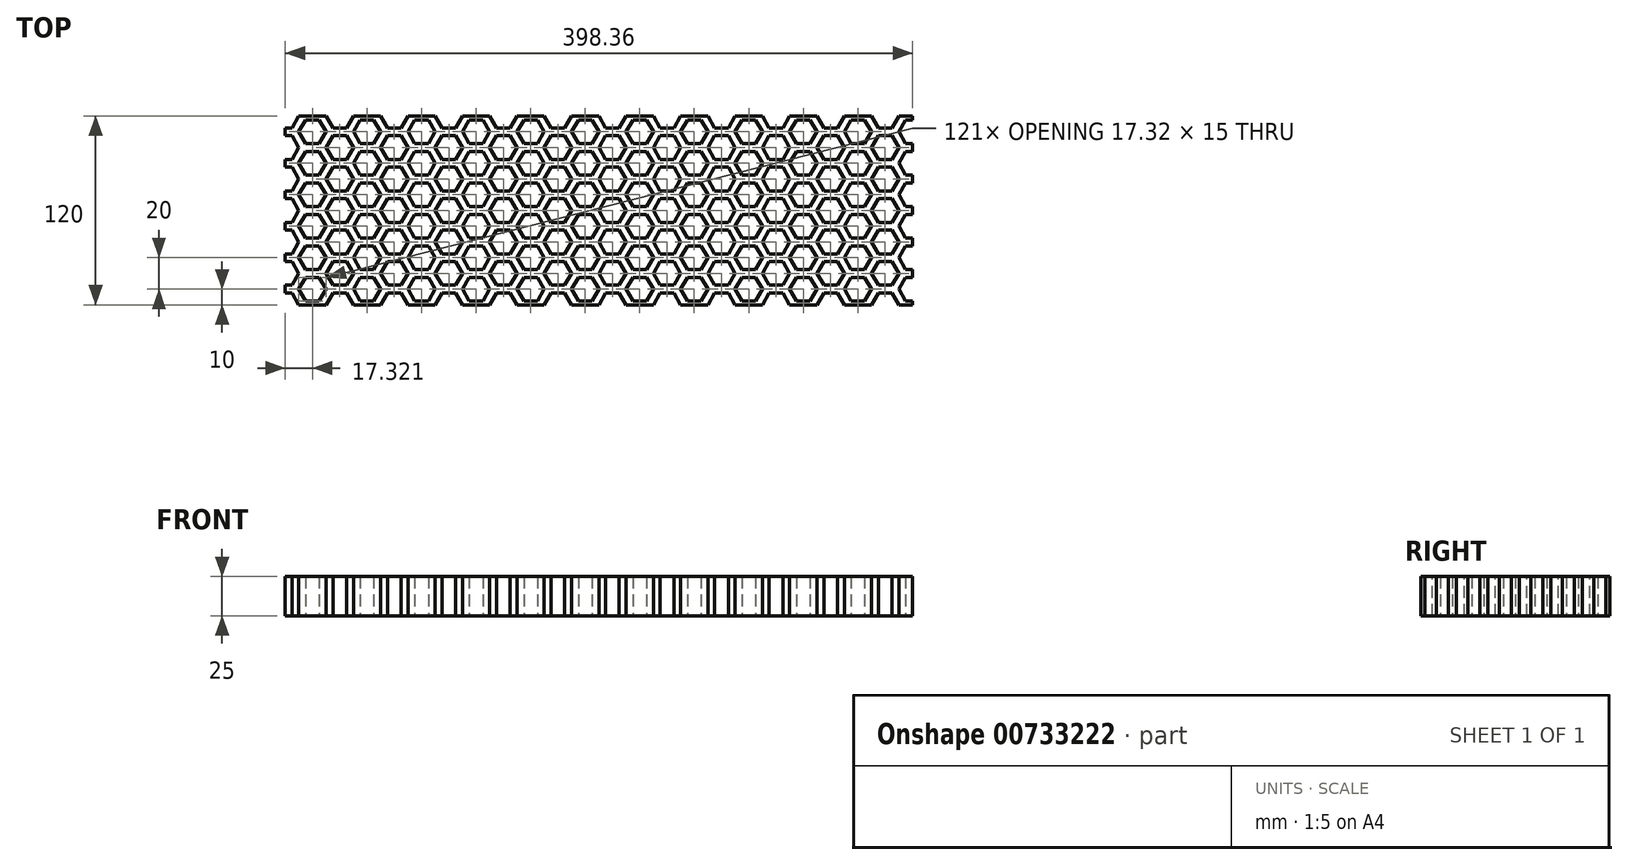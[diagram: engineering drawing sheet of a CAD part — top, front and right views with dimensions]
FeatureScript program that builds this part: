
annotation { "Feature Type Name" : "Feature", "Feature Type Description" : "" }
export const myFeature = defineFeature(function(context is Context, id is Id, definition is map)
    precondition{}
    {
        {
            var Q0;
            Q0=qCreatedBy(makeId("Top.planeOp"),FACE);
            var sketch = newSketch(context, id + "F0", { "sketchPlane" : qUnion([Q0])});
            skLineSegment(sketch, "E0.0", {"start": v(16.84, -2.5) * mm, "end": v(21.65, -2.5) * mm});
            skLineSegment(sketch, "E0.1", {"start": v(21.65, -2.5) * mm, "end": v(25.98, -10) * mm});
            skLineSegment(sketch, "E1.0", {"start": v(16.84, 17.5) * mm, "end": v(21.65, 17.5) * mm});
            skLineSegment(sketch, "E1.1", {"start": v(21.65, 17.5) * mm, "end": v(25.98, 10) * mm});
            skLineSegment(sketch, "E1.2", {"start": v(25.98, 10) * mm, "end": v(21.65, 2.5) * mm});
            skLineSegment(sketch, "E1.3", {"start": v(21.65, 2.5) * mm, "end": v(16.84, 2.5) * mm});
            skLineSegment(sketch, "E2.0.1.1", {"start": v(21.65, 57.5) * mm, "end": v(25.98, 50) * mm});
            skLineSegment(sketch, "E2.0.1.11", {"start": v(21.65, 22.5) * mm, "end": v(16.84, 22.5) * mm});
            skLineSegment(sketch, "E2.0.1.12", {"start": v(25.98, 30) * mm, "end": v(21.65, 22.5) * mm});
            skLineSegment(sketch, "E2.0.1.14", {"start": v(25.98, 50) * mm, "end": v(21.65, 42.5) * mm});
            skLineSegment(sketch, "E2.0.1.20", {"start": v(21.65, 37.5) * mm, "end": v(25.98, 30) * mm});
            skLineSegment(sketch, "E2.0.1.23", {"start": v(16.84, 57.5) * mm, "end": v(21.65, 57.5) * mm});
            skLineSegment(sketch, "E2.0.1.24", {"start": v(16.84, 37.5) * mm, "end": v(21.65, 37.5) * mm});
            skLineSegment(sketch, "E2.0.2.1", {"start": v(21.65, 97.5) * mm, "end": v(25.98, 90) * mm});
            skLineSegment(sketch, "E2.0.2.6", {"start": v(21.65, 82.5) * mm, "end": v(16.84, 82.5) * mm});
            skLineSegment(sketch, "E2.0.2.11", {"start": v(21.65, 62.5) * mm, "end": v(16.84, 62.5) * mm});
            skLineSegment(sketch, "E2.0.2.12", {"start": v(25.98, 70) * mm, "end": v(21.65, 62.5) * mm});
            skLineSegment(sketch, "E2.0.2.14", {"start": v(25.98, 90) * mm, "end": v(21.65, 82.5) * mm});
            skLineSegment(sketch, "E2.0.2.20", {"start": v(21.65, 77.5) * mm, "end": v(25.98, 70) * mm});
            skLineSegment(sketch, "E2.0.2.23", {"start": v(16.84, 97.5) * mm, "end": v(21.65, 97.5) * mm});
            skLineSegment(sketch, "E2.0.2.24", {"start": v(16.84, 77.5) * mm, "end": v(21.65, 77.5) * mm});
            skLineSegment(sketch, "E2.0.3.6", {"start": v(21.65, 122.5) * mm, "end": v(16.84, 122.5) * mm});
            skLineSegment(sketch, "E2.0.3.11", {"start": v(21.65, 102.5) * mm, "end": v(16.84, 102.5) * mm});
            skLineSegment(sketch, "E2.0.3.12", {"start": v(25.98, 110) * mm, "end": v(21.65, 102.5) * mm});
            skLineSegment(sketch, "E2.0.3.14", {"start": v(25.98, 130) * mm, "end": v(21.65, 122.5) * mm});
            skLineSegment(sketch, "E2.0.3.20", {"start": v(21.65, 117.5) * mm, "end": v(25.98, 110) * mm});
            skLineSegment(sketch, "E2.0.3.24", {"start": v(16.84, 117.5) * mm, "end": v(21.65, 117.5) * mm});
            skLineSegment(sketch, "E2.1.0.0", {"start": v(43.3, -10) * mm, "end": v(47.63, -2.5) * mm});
            skLineSegment(sketch, "E2.1.0.1", {"start": v(56.3, 17.5) * mm, "end": v(60.62, 10) * mm});
            skLineSegment(sketch, "E2.1.0.2", {"start": v(25.98, 0) * mm, "end": v(30.3, 7.5) * mm});
            skPoint(sketch, "E2.1.0.3", {"position": v(51.96, 17.5) * mm});
            skLineSegment(sketch, "E2.1.0.4", {"start": v(30.3, -7.5) * mm, "end": v(25.98, 0) * mm});
            skLineSegment(sketch, "E2.1.0.5", {"start": v(38.97, -7.5) * mm, "end": v(30.3, -7.5) * mm});
            skLineSegment(sketch, "E2.1.0.6", {"start": v(56.3, 2.5) * mm, "end": v(47.63, 2.5) * mm});
            skLineSegment(sketch, "E2.1.0.7", {"start": v(43.3, 0) * mm, "end": v(38.97, -7.5) * mm});
            skLineSegment(sketch, "E2.1.0.8", {"start": v(47.63, 2.5) * mm, "end": v(43.3, 10) * mm});
            skLineSegment(sketch, "E2.1.0.13", {"start": v(25.98, 0) * mm, "end": v(43.3, 0) * mm, "construction": true});
            skLineSegment(sketch, "E2.1.0.14", {"start": v(60.62, 10) * mm, "end": v(56.3, 2.5) * mm});
            skPoint(sketch, "E2.1.0.15", {"position": v(51.96, -2.5) * mm});
            skCircle(sketch, "E2.1.0.16", {"center": v(51.96, 10) * mm, "radius": 7.5 * mm, "construction": true});
            skCircle(sketch, "E2.1.0.17", {"center": v(34.64, 0) * mm, "radius": 7.5 * mm, "construction": true});
            skLineSegment(sketch, "E2.1.0.18", {"start": v(38.97, 7.5) * mm, "end": v(43.3, 0) * mm});
            skPoint(sketch, "E2.1.0.19", {"position": v(34.64, 7.5) * mm});
            skLineSegment(sketch, "E2.1.0.20", {"start": v(56.3, -2.5) * mm, "end": v(60.62, -10) * mm});
            skLineSegment(sketch, "E2.1.0.21", {"start": v(43.3, 10) * mm, "end": v(47.63, 17.5) * mm});
            skLineSegment(sketch, "E2.1.0.22", {"start": v(30.3, 7.5) * mm, "end": v(38.97, 7.5) * mm});
            skLineSegment(sketch, "E2.1.0.23", {"start": v(47.63, 17.5) * mm, "end": v(56.3, 17.5) * mm});
            skLineSegment(sketch, "E2.1.0.24", {"start": v(47.63, -2.5) * mm, "end": v(56.3, -2.5) * mm});
            skLineSegment(sketch, "E2.1.1.0", {"start": v(43.3, 30) * mm, "end": v(47.63, 37.5) * mm});
            skLineSegment(sketch, "E2.1.1.1", {"start": v(56.3, 57.5) * mm, "end": v(60.62, 50) * mm});
            skLineSegment(sketch, "E2.1.1.2", {"start": v(25.98, 40) * mm, "end": v(30.3, 47.5) * mm});
            skPoint(sketch, "E2.1.1.3", {"position": v(51.96, 57.5) * mm});
            skLineSegment(sketch, "E2.1.1.4", {"start": v(30.3, 32.5) * mm, "end": v(25.98, 40) * mm});
            skLineSegment(sketch, "E2.1.1.5", {"start": v(38.97, 32.5) * mm, "end": v(30.3, 32.5) * mm});
            skLineSegment(sketch, "E2.1.1.6", {"start": v(56.3, 42.5) * mm, "end": v(47.63, 42.5) * mm});
            skLineSegment(sketch, "E2.1.1.7", {"start": v(43.3, 40) * mm, "end": v(38.97, 32.5) * mm});
            skLineSegment(sketch, "E2.1.1.8", {"start": v(47.63, 42.5) * mm, "end": v(43.3, 50) * mm});
            skCircle(sketch, "E2.1.1.9", {"center": v(51.96, 30) * mm, "radius": 7.5 * mm, "construction": true});
            skLineSegment(sketch, "E2.1.1.10", {"start": v(47.63, 22.5) * mm, "end": v(43.3, 30) * mm});
            skLineSegment(sketch, "E2.1.1.11", {"start": v(56.3, 22.5) * mm, "end": v(47.63, 22.5) * mm});
            skLineSegment(sketch, "E2.1.1.12", {"start": v(60.62, 30) * mm, "end": v(56.3, 22.5) * mm});
            skLineSegment(sketch, "E2.1.1.13", {"start": v(25.98, 40) * mm, "end": v(43.3, 40) * mm, "construction": true});
            skLineSegment(sketch, "E2.1.1.14", {"start": v(60.62, 50) * mm, "end": v(56.3, 42.5) * mm});
            skPoint(sketch, "E2.1.1.15", {"position": v(51.96, 37.5) * mm});
            skCircle(sketch, "E2.1.1.16", {"center": v(51.96, 50) * mm, "radius": 7.5 * mm, "construction": true});
            skCircle(sketch, "E2.1.1.17", {"center": v(34.64, 40) * mm, "radius": 7.5 * mm, "construction": true});
            skLineSegment(sketch, "E2.1.1.18", {"start": v(38.97, 47.5) * mm, "end": v(43.3, 40) * mm});
            skPoint(sketch, "E2.1.1.19", {"position": v(34.64, 47.5) * mm});
            skLineSegment(sketch, "E2.1.1.20", {"start": v(56.3, 37.5) * mm, "end": v(60.62, 30) * mm});
            skLineSegment(sketch, "E2.1.1.21", {"start": v(43.3, 50) * mm, "end": v(47.63, 57.5) * mm});
            skLineSegment(sketch, "E2.1.1.22", {"start": v(30.3, 47.5) * mm, "end": v(38.97, 47.5) * mm});
            skLineSegment(sketch, "E2.1.1.23", {"start": v(47.63, 57.5) * mm, "end": v(56.3, 57.5) * mm});
            skLineSegment(sketch, "E2.1.1.24", {"start": v(47.63, 37.5) * mm, "end": v(56.3, 37.5) * mm});
            skLineSegment(sketch, "E2.1.2.0", {"start": v(43.3, 70) * mm, "end": v(47.63, 77.5) * mm});
            skLineSegment(sketch, "E2.1.2.1", {"start": v(56.3, 97.5) * mm, "end": v(60.62, 90) * mm});
            skLineSegment(sketch, "E2.1.2.2", {"start": v(25.98, 80) * mm, "end": v(30.3, 87.5) * mm});
            skPoint(sketch, "E2.1.2.3", {"position": v(51.96, 97.5) * mm});
            skLineSegment(sketch, "E2.1.2.4", {"start": v(30.3, 72.5) * mm, "end": v(25.98, 80) * mm});
            skLineSegment(sketch, "E2.1.2.5", {"start": v(38.97, 72.5) * mm, "end": v(30.3, 72.5) * mm});
            skLineSegment(sketch, "E2.1.2.6", {"start": v(56.3, 82.5) * mm, "end": v(47.63, 82.5) * mm});
            skLineSegment(sketch, "E2.1.2.7", {"start": v(43.3, 80) * mm, "end": v(38.97, 72.5) * mm});
            skLineSegment(sketch, "E2.1.2.8", {"start": v(47.63, 82.5) * mm, "end": v(43.3, 90) * mm});
            skCircle(sketch, "E2.1.2.9", {"center": v(51.96, 70) * mm, "radius": 7.5 * mm, "construction": true});
            skLineSegment(sketch, "E2.1.2.10", {"start": v(47.63, 62.5) * mm, "end": v(43.3, 70) * mm});
            skLineSegment(sketch, "E2.1.2.11", {"start": v(56.3, 62.5) * mm, "end": v(47.63, 62.5) * mm});
            skLineSegment(sketch, "E2.1.2.12", {"start": v(60.62, 70) * mm, "end": v(56.3, 62.5) * mm});
            skLineSegment(sketch, "E2.1.2.13", {"start": v(25.98, 80) * mm, "end": v(43.3, 80) * mm, "construction": true});
            skLineSegment(sketch, "E2.1.2.14", {"start": v(60.62, 90) * mm, "end": v(56.3, 82.5) * mm});
            skPoint(sketch, "E2.1.2.15", {"position": v(51.96, 77.5) * mm});
            skCircle(sketch, "E2.1.2.16", {"center": v(51.96, 90) * mm, "radius": 7.5 * mm, "construction": true});
            skCircle(sketch, "E2.1.2.17", {"center": v(34.64, 80) * mm, "radius": 7.5 * mm, "construction": true});
            skLineSegment(sketch, "E2.1.2.18", {"start": v(38.97, 87.5) * mm, "end": v(43.3, 80) * mm});
            skPoint(sketch, "E2.1.2.19", {"position": v(34.64, 87.5) * mm});
            skLineSegment(sketch, "E2.1.2.20", {"start": v(56.3, 77.5) * mm, "end": v(60.62, 70) * mm});
            skLineSegment(sketch, "E2.1.2.21", {"start": v(43.3, 90) * mm, "end": v(47.63, 97.5) * mm});
            skLineSegment(sketch, "E2.1.2.22", {"start": v(30.3, 87.5) * mm, "end": v(38.97, 87.5) * mm});
            skLineSegment(sketch, "E2.1.2.23", {"start": v(47.63, 97.5) * mm, "end": v(56.3, 97.5) * mm});
            skLineSegment(sketch, "E2.1.2.24", {"start": v(47.63, 77.5) * mm, "end": v(56.3, 77.5) * mm});
            skLineSegment(sketch, "E2.1.3.0", {"start": v(43.3, 110) * mm, "end": v(47.63, 117.5) * mm});
            skLineSegment(sketch, "E2.1.3.2", {"start": v(25.98, 120) * mm, "end": v(30.3, 127.5) * mm});
            skLineSegment(sketch, "E2.1.3.4", {"start": v(30.3, 112.5) * mm, "end": v(25.98, 120) * mm});
            skLineSegment(sketch, "E2.1.3.5", {"start": v(38.97, 112.5) * mm, "end": v(30.3, 112.5) * mm});
            skLineSegment(sketch, "E2.1.3.6", {"start": v(56.3, 122.5) * mm, "end": v(47.63, 122.5) * mm});
            skLineSegment(sketch, "E2.1.3.7", {"start": v(43.3, 120) * mm, "end": v(38.97, 112.5) * mm});
            skLineSegment(sketch, "E2.1.3.8", {"start": v(47.63, 122.5) * mm, "end": v(43.3, 130) * mm});
            skCircle(sketch, "E2.1.3.9", {"center": v(51.96, 110) * mm, "radius": 7.5 * mm, "construction": true});
            skLineSegment(sketch, "E2.1.3.10", {"start": v(47.63, 102.5) * mm, "end": v(43.3, 110) * mm});
            skLineSegment(sketch, "E2.1.3.11", {"start": v(56.3, 102.5) * mm, "end": v(47.63, 102.5) * mm});
            skLineSegment(sketch, "E2.1.3.12", {"start": v(60.62, 110) * mm, "end": v(56.3, 102.5) * mm});
            skLineSegment(sketch, "E2.1.3.13", {"start": v(25.98, 120) * mm, "end": v(43.3, 120) * mm, "construction": true});
            skLineSegment(sketch, "E2.1.3.14", {"start": v(60.62, 130) * mm, "end": v(56.3, 122.5) * mm});
            skPoint(sketch, "E2.1.3.15", {"position": v(51.96, 117.5) * mm});
            skCircle(sketch, "E2.1.3.17", {"center": v(34.64, 120) * mm, "radius": 7.5 * mm, "construction": true});
            skLineSegment(sketch, "E2.1.3.18", {"start": v(38.97, 127.5) * mm, "end": v(43.3, 120) * mm});
            skLineSegment(sketch, "E2.1.3.20", {"start": v(56.3, 117.5) * mm, "end": v(60.62, 110) * mm});
            skLineSegment(sketch, "E2.1.3.22", {"start": v(30.3, 127.5) * mm, "end": v(38.97, 127.5) * mm});
            skLineSegment(sketch, "E2.1.3.24", {"start": v(47.63, 117.5) * mm, "end": v(56.3, 117.5) * mm});
            skLineSegment(sketch, "E2.2.0.0", {"start": v(77.94, -10) * mm, "end": v(82.27, -2.5) * mm});
            skLineSegment(sketch, "E2.2.0.1", {"start": v(90.93, 17.5) * mm, "end": v(95.26, 10) * mm});
            skLineSegment(sketch, "E2.2.0.2", {"start": v(60.62, 0) * mm, "end": v(64.95, 7.5) * mm});
            skPoint(sketch, "E2.2.0.3", {"position": v(86.6, 17.5) * mm});
            skLineSegment(sketch, "E2.2.0.4", {"start": v(64.95, -7.5) * mm, "end": v(60.62, 0) * mm});
            skLineSegment(sketch, "E2.2.0.5", {"start": v(73.61, -7.5) * mm, "end": v(64.95, -7.5) * mm});
            skLineSegment(sketch, "E2.2.0.6", {"start": v(90.93, 2.5) * mm, "end": v(82.27, 2.5) * mm});
            skLineSegment(sketch, "E2.2.0.7", {"start": v(77.94, 0) * mm, "end": v(73.61, -7.5) * mm});
            skLineSegment(sketch, "E2.2.0.8", {"start": v(82.27, 2.5) * mm, "end": v(77.94, 10) * mm});
            skLineSegment(sketch, "E2.2.0.13", {"start": v(60.62, 0) * mm, "end": v(77.94, 0) * mm, "construction": true});
            skLineSegment(sketch, "E2.2.0.14", {"start": v(95.26, 10) * mm, "end": v(90.93, 2.5) * mm});
            skPoint(sketch, "E2.2.0.15", {"position": v(86.6, -2.5) * mm});
            skCircle(sketch, "E2.2.0.16", {"center": v(86.6, 10) * mm, "radius": 7.5 * mm, "construction": true});
            skCircle(sketch, "E2.2.0.17", {"center": v(69.28, 0) * mm, "radius": 7.5 * mm, "construction": true});
            skLineSegment(sketch, "E2.2.0.18", {"start": v(73.61, 7.5) * mm, "end": v(77.94, 0) * mm});
            skPoint(sketch, "E2.2.0.19", {"position": v(69.28, 7.5) * mm});
            skLineSegment(sketch, "E2.2.0.20", {"start": v(90.93, -2.5) * mm, "end": v(95.26, -10) * mm});
            skLineSegment(sketch, "E2.2.0.21", {"start": v(77.94, 10) * mm, "end": v(82.27, 17.5) * mm});
            skLineSegment(sketch, "E2.2.0.22", {"start": v(64.95, 7.5) * mm, "end": v(73.61, 7.5) * mm});
            skLineSegment(sketch, "E2.2.0.23", {"start": v(82.27, 17.5) * mm, "end": v(90.93, 17.5) * mm});
            skLineSegment(sketch, "E2.2.0.24", {"start": v(82.27, -2.5) * mm, "end": v(90.93, -2.5) * mm});
            skLineSegment(sketch, "E2.2.1.0", {"start": v(77.94, 30) * mm, "end": v(82.27, 37.5) * mm});
            skLineSegment(sketch, "E2.2.1.1", {"start": v(90.93, 57.5) * mm, "end": v(95.26, 50) * mm});
            skLineSegment(sketch, "E2.2.1.2", {"start": v(60.62, 40) * mm, "end": v(64.95, 47.5) * mm});
            skPoint(sketch, "E2.2.1.3", {"position": v(86.6, 57.5) * mm});
            skLineSegment(sketch, "E2.2.1.4", {"start": v(64.95, 32.5) * mm, "end": v(60.62, 40) * mm});
            skLineSegment(sketch, "E2.2.1.5", {"start": v(73.61, 32.5) * mm, "end": v(64.95, 32.5) * mm});
            skLineSegment(sketch, "E2.2.1.6", {"start": v(90.93, 42.5) * mm, "end": v(82.27, 42.5) * mm});
            skLineSegment(sketch, "E2.2.1.7", {"start": v(77.94, 40) * mm, "end": v(73.61, 32.5) * mm});
            skLineSegment(sketch, "E2.2.1.8", {"start": v(82.27, 42.5) * mm, "end": v(77.94, 50) * mm});
            skCircle(sketch, "E2.2.1.9", {"center": v(86.6, 30) * mm, "radius": 7.5 * mm, "construction": true});
            skLineSegment(sketch, "E2.2.1.10", {"start": v(82.27, 22.5) * mm, "end": v(77.94, 30) * mm});
            skLineSegment(sketch, "E2.2.1.11", {"start": v(90.93, 22.5) * mm, "end": v(82.27, 22.5) * mm});
            skLineSegment(sketch, "E2.2.1.12", {"start": v(95.26, 30) * mm, "end": v(90.93, 22.5) * mm});
            skLineSegment(sketch, "E2.2.1.13", {"start": v(60.62, 40) * mm, "end": v(77.94, 40) * mm, "construction": true});
            skLineSegment(sketch, "E2.2.1.14", {"start": v(95.26, 50) * mm, "end": v(90.93, 42.5) * mm});
            skPoint(sketch, "E2.2.1.15", {"position": v(86.6, 37.5) * mm});
            skCircle(sketch, "E2.2.1.16", {"center": v(86.6, 50) * mm, "radius": 7.5 * mm, "construction": true});
            skCircle(sketch, "E2.2.1.17", {"center": v(69.28, 40) * mm, "radius": 7.5 * mm, "construction": true});
            skLineSegment(sketch, "E2.2.1.18", {"start": v(73.61, 47.5) * mm, "end": v(77.94, 40) * mm});
            skPoint(sketch, "E2.2.1.19", {"position": v(69.28, 47.5) * mm});
            skLineSegment(sketch, "E2.2.1.20", {"start": v(90.93, 37.5) * mm, "end": v(95.26, 30) * mm});
            skLineSegment(sketch, "E2.2.1.21", {"start": v(77.94, 50) * mm, "end": v(82.27, 57.5) * mm});
            skLineSegment(sketch, "E2.2.1.22", {"start": v(64.95, 47.5) * mm, "end": v(73.61, 47.5) * mm});
            skLineSegment(sketch, "E2.2.1.23", {"start": v(82.27, 57.5) * mm, "end": v(90.93, 57.5) * mm});
            skLineSegment(sketch, "E2.2.1.24", {"start": v(82.27, 37.5) * mm, "end": v(90.93, 37.5) * mm});
            skLineSegment(sketch, "E2.2.2.0", {"start": v(77.94, 70) * mm, "end": v(82.27, 77.5) * mm});
            skLineSegment(sketch, "E2.2.2.1", {"start": v(90.93, 97.5) * mm, "end": v(95.26, 90) * mm});
            skLineSegment(sketch, "E2.2.2.2", {"start": v(60.62, 80) * mm, "end": v(64.95, 87.5) * mm});
            skPoint(sketch, "E2.2.2.3", {"position": v(86.6, 97.5) * mm});
            skLineSegment(sketch, "E2.2.2.4", {"start": v(64.95, 72.5) * mm, "end": v(60.62, 80) * mm});
            skLineSegment(sketch, "E2.2.2.5", {"start": v(73.61, 72.5) * mm, "end": v(64.95, 72.5) * mm});
            skLineSegment(sketch, "E2.2.2.6", {"start": v(90.93, 82.5) * mm, "end": v(82.27, 82.5) * mm});
            skLineSegment(sketch, "E2.2.2.7", {"start": v(77.94, 80) * mm, "end": v(73.61, 72.5) * mm});
            skLineSegment(sketch, "E2.2.2.8", {"start": v(82.27, 82.5) * mm, "end": v(77.94, 90) * mm});
            skCircle(sketch, "E2.2.2.9", {"center": v(86.6, 70) * mm, "radius": 7.5 * mm, "construction": true});
            skLineSegment(sketch, "E2.2.2.10", {"start": v(82.27, 62.5) * mm, "end": v(77.94, 70) * mm});
            skLineSegment(sketch, "E2.2.2.11", {"start": v(90.93, 62.5) * mm, "end": v(82.27, 62.5) * mm});
            skLineSegment(sketch, "E2.2.2.12", {"start": v(95.26, 70) * mm, "end": v(90.93, 62.5) * mm});
            skLineSegment(sketch, "E2.2.2.13", {"start": v(60.62, 80) * mm, "end": v(77.94, 80) * mm, "construction": true});
            skLineSegment(sketch, "E2.2.2.14", {"start": v(95.26, 90) * mm, "end": v(90.93, 82.5) * mm});
            skPoint(sketch, "E2.2.2.15", {"position": v(86.6, 77.5) * mm});
            skCircle(sketch, "E2.2.2.16", {"center": v(86.6, 90) * mm, "radius": 7.5 * mm, "construction": true});
            skCircle(sketch, "E2.2.2.17", {"center": v(69.28, 80) * mm, "radius": 7.5 * mm, "construction": true});
            skLineSegment(sketch, "E2.2.2.18", {"start": v(73.61, 87.5) * mm, "end": v(77.94, 80) * mm});
            skPoint(sketch, "E2.2.2.19", {"position": v(69.28, 87.5) * mm});
            skLineSegment(sketch, "E2.2.2.20", {"start": v(90.93, 77.5) * mm, "end": v(95.26, 70) * mm});
            skLineSegment(sketch, "E2.2.2.21", {"start": v(77.94, 90) * mm, "end": v(82.27, 97.5) * mm});
            skLineSegment(sketch, "E2.2.2.22", {"start": v(64.95, 87.5) * mm, "end": v(73.61, 87.5) * mm});
            skLineSegment(sketch, "E2.2.2.23", {"start": v(82.27, 97.5) * mm, "end": v(90.93, 97.5) * mm});
            skLineSegment(sketch, "E2.2.2.24", {"start": v(82.27, 77.5) * mm, "end": v(90.93, 77.5) * mm});
            skLineSegment(sketch, "E2.2.3.0", {"start": v(77.94, 110) * mm, "end": v(82.27, 117.5) * mm});
            skLineSegment(sketch, "E2.2.3.2", {"start": v(60.62, 120) * mm, "end": v(64.95, 127.5) * mm});
            skLineSegment(sketch, "E2.2.3.4", {"start": v(64.95, 112.5) * mm, "end": v(60.62, 120) * mm});
            skLineSegment(sketch, "E2.2.3.5", {"start": v(73.61, 112.5) * mm, "end": v(64.95, 112.5) * mm});
            skLineSegment(sketch, "E2.2.3.6", {"start": v(90.93, 122.5) * mm, "end": v(82.27, 122.5) * mm});
            skLineSegment(sketch, "E2.2.3.7", {"start": v(77.94, 120) * mm, "end": v(73.61, 112.5) * mm});
            skLineSegment(sketch, "E2.2.3.8", {"start": v(82.27, 122.5) * mm, "end": v(77.94, 130) * mm});
            skCircle(sketch, "E2.2.3.9", {"center": v(86.6, 110) * mm, "radius": 7.5 * mm, "construction": true});
            skLineSegment(sketch, "E2.2.3.10", {"start": v(82.27, 102.5) * mm, "end": v(77.94, 110) * mm});
            skLineSegment(sketch, "E2.2.3.11", {"start": v(90.93, 102.5) * mm, "end": v(82.27, 102.5) * mm});
            skLineSegment(sketch, "E2.2.3.12", {"start": v(95.26, 110) * mm, "end": v(90.93, 102.5) * mm});
            skLineSegment(sketch, "E2.2.3.13", {"start": v(60.62, 120) * mm, "end": v(77.94, 120) * mm, "construction": true});
            skLineSegment(sketch, "E2.2.3.14", {"start": v(95.26, 130) * mm, "end": v(90.93, 122.5) * mm});
            skPoint(sketch, "E2.2.3.15", {"position": v(86.6, 117.5) * mm});
            skCircle(sketch, "E2.2.3.17", {"center": v(69.28, 120) * mm, "radius": 7.5 * mm, "construction": true});
            skLineSegment(sketch, "E2.2.3.18", {"start": v(73.61, 127.5) * mm, "end": v(77.94, 120) * mm});
            skLineSegment(sketch, "E2.2.3.20", {"start": v(90.93, 117.5) * mm, "end": v(95.26, 110) * mm});
            skLineSegment(sketch, "E2.2.3.22", {"start": v(64.95, 127.5) * mm, "end": v(73.61, 127.5) * mm});
            skLineSegment(sketch, "E2.2.3.24", {"start": v(82.27, 117.5) * mm, "end": v(90.93, 117.5) * mm});
            skLineSegment(sketch, "E2.3.0.0", {"start": v(112.58, -10) * mm, "end": v(116.91, -2.5) * mm});
            skLineSegment(sketch, "E2.3.0.1", {"start": v(125.57, 17.5) * mm, "end": v(129.9, 10) * mm});
            skLineSegment(sketch, "E2.3.0.2", {"start": v(95.26, 0) * mm, "end": v(99.59, 7.5) * mm});
            skPoint(sketch, "E2.3.0.3", {"position": v(121.24, 17.5) * mm});
            skLineSegment(sketch, "E2.3.0.4", {"start": v(99.59, -7.5) * mm, "end": v(95.26, 0) * mm});
            skLineSegment(sketch, "E2.3.0.5", {"start": v(108.25, -7.5) * mm, "end": v(99.59, -7.5) * mm});
            skLineSegment(sketch, "E2.3.0.6", {"start": v(125.57, 2.5) * mm, "end": v(116.91, 2.5) * mm});
            skLineSegment(sketch, "E2.3.0.7", {"start": v(112.58, 0) * mm, "end": v(108.25, -7.5) * mm});
            skLineSegment(sketch, "E2.3.0.8", {"start": v(116.91, 2.5) * mm, "end": v(112.58, 10) * mm});
            skLineSegment(sketch, "E2.3.0.13", {"start": v(95.26, 0) * mm, "end": v(112.58, 0) * mm, "construction": true});
            skLineSegment(sketch, "E2.3.0.14", {"start": v(129.9, 10) * mm, "end": v(125.57, 2.5) * mm});
            skPoint(sketch, "E2.3.0.15", {"position": v(121.24, -2.5) * mm});
            skCircle(sketch, "E2.3.0.16", {"center": v(121.24, 10) * mm, "radius": 7.5 * mm, "construction": true});
            skCircle(sketch, "E2.3.0.17", {"center": v(103.92, 0) * mm, "radius": 7.5 * mm, "construction": true});
            skLineSegment(sketch, "E2.3.0.18", {"start": v(108.25, 7.5) * mm, "end": v(112.58, 0) * mm});
            skPoint(sketch, "E2.3.0.19", {"position": v(103.92, 7.5) * mm});
            skLineSegment(sketch, "E2.3.0.20", {"start": v(125.57, -2.5) * mm, "end": v(129.9, -10) * mm});
            skLineSegment(sketch, "E2.3.0.21", {"start": v(112.58, 10) * mm, "end": v(116.91, 17.5) * mm});
            skLineSegment(sketch, "E2.3.0.22", {"start": v(99.59, 7.5) * mm, "end": v(108.25, 7.5) * mm});
            skLineSegment(sketch, "E2.3.0.23", {"start": v(116.91, 17.5) * mm, "end": v(125.57, 17.5) * mm});
            skLineSegment(sketch, "E2.3.0.24", {"start": v(116.91, -2.5) * mm, "end": v(125.57, -2.5) * mm});
            skLineSegment(sketch, "E2.3.1.0", {"start": v(112.58, 30) * mm, "end": v(116.91, 37.5) * mm});
            skLineSegment(sketch, "E2.3.1.1", {"start": v(125.57, 57.5) * mm, "end": v(129.9, 50) * mm});
            skLineSegment(sketch, "E2.3.1.2", {"start": v(95.26, 40) * mm, "end": v(99.59, 47.5) * mm});
            skPoint(sketch, "E2.3.1.3", {"position": v(121.24, 57.5) * mm});
            skLineSegment(sketch, "E2.3.1.4", {"start": v(99.59, 32.5) * mm, "end": v(95.26, 40) * mm});
            skLineSegment(sketch, "E2.3.1.5", {"start": v(108.25, 32.5) * mm, "end": v(99.59, 32.5) * mm});
            skLineSegment(sketch, "E2.3.1.6", {"start": v(125.57, 42.5) * mm, "end": v(116.91, 42.5) * mm});
            skLineSegment(sketch, "E2.3.1.7", {"start": v(112.58, 40) * mm, "end": v(108.25, 32.5) * mm});
            skLineSegment(sketch, "E2.3.1.8", {"start": v(116.91, 42.5) * mm, "end": v(112.58, 50) * mm});
            skCircle(sketch, "E2.3.1.9", {"center": v(121.24, 30) * mm, "radius": 7.5 * mm, "construction": true});
            skLineSegment(sketch, "E2.3.1.10", {"start": v(116.91, 22.5) * mm, "end": v(112.58, 30) * mm});
            skLineSegment(sketch, "E2.3.1.11", {"start": v(125.57, 22.5) * mm, "end": v(116.91, 22.5) * mm});
            skLineSegment(sketch, "E2.3.1.12", {"start": v(129.9, 30) * mm, "end": v(125.57, 22.5) * mm});
            skLineSegment(sketch, "E2.3.1.13", {"start": v(95.26, 40) * mm, "end": v(112.58, 40) * mm, "construction": true});
            skLineSegment(sketch, "E2.3.1.14", {"start": v(129.9, 50) * mm, "end": v(125.57, 42.5) * mm});
            skPoint(sketch, "E2.3.1.15", {"position": v(121.24, 37.5) * mm});
            skCircle(sketch, "E2.3.1.16", {"center": v(121.24, 50) * mm, "radius": 7.5 * mm, "construction": true});
            skCircle(sketch, "E2.3.1.17", {"center": v(103.92, 40) * mm, "radius": 7.5 * mm, "construction": true});
            skLineSegment(sketch, "E2.3.1.18", {"start": v(108.25, 47.5) * mm, "end": v(112.58, 40) * mm});
            skPoint(sketch, "E2.3.1.19", {"position": v(103.92, 47.5) * mm});
            skLineSegment(sketch, "E2.3.1.20", {"start": v(125.57, 37.5) * mm, "end": v(129.9, 30) * mm});
            skLineSegment(sketch, "E2.3.1.21", {"start": v(112.58, 50) * mm, "end": v(116.91, 57.5) * mm});
            skLineSegment(sketch, "E2.3.1.22", {"start": v(99.59, 47.5) * mm, "end": v(108.25, 47.5) * mm});
            skLineSegment(sketch, "E2.3.1.23", {"start": v(116.91, 57.5) * mm, "end": v(125.57, 57.5) * mm});
            skLineSegment(sketch, "E2.3.1.24", {"start": v(116.91, 37.5) * mm, "end": v(125.57, 37.5) * mm});
            skLineSegment(sketch, "E2.3.2.0", {"start": v(112.58, 70) * mm, "end": v(116.91, 77.5) * mm});
            skLineSegment(sketch, "E2.3.2.1", {"start": v(125.57, 97.5) * mm, "end": v(129.9, 90) * mm});
            skLineSegment(sketch, "E2.3.2.2", {"start": v(95.26, 80) * mm, "end": v(99.59, 87.5) * mm});
            skPoint(sketch, "E2.3.2.3", {"position": v(121.24, 97.5) * mm});
            skLineSegment(sketch, "E2.3.2.4", {"start": v(99.59, 72.5) * mm, "end": v(95.26, 80) * mm});
            skLineSegment(sketch, "E2.3.2.5", {"start": v(108.25, 72.5) * mm, "end": v(99.59, 72.5) * mm});
            skLineSegment(sketch, "E2.3.2.6", {"start": v(125.57, 82.5) * mm, "end": v(116.91, 82.5) * mm});
            skLineSegment(sketch, "E2.3.2.7", {"start": v(112.58, 80) * mm, "end": v(108.25, 72.5) * mm});
            skLineSegment(sketch, "E2.3.2.8", {"start": v(116.91, 82.5) * mm, "end": v(112.58, 90) * mm});
            skCircle(sketch, "E2.3.2.9", {"center": v(121.24, 70) * mm, "radius": 7.5 * mm, "construction": true});
            skLineSegment(sketch, "E2.3.2.10", {"start": v(116.91, 62.5) * mm, "end": v(112.58, 70) * mm});
            skLineSegment(sketch, "E2.3.2.11", {"start": v(125.57, 62.5) * mm, "end": v(116.91, 62.5) * mm});
            skLineSegment(sketch, "E2.3.2.12", {"start": v(129.9, 70) * mm, "end": v(125.57, 62.5) * mm});
            skLineSegment(sketch, "E2.3.2.13", {"start": v(95.26, 80) * mm, "end": v(112.58, 80) * mm, "construction": true});
            skLineSegment(sketch, "E2.3.2.14", {"start": v(129.9, 90) * mm, "end": v(125.57, 82.5) * mm});
            skPoint(sketch, "E2.3.2.15", {"position": v(121.24, 77.5) * mm});
            skCircle(sketch, "E2.3.2.16", {"center": v(121.24, 90) * mm, "radius": 7.5 * mm, "construction": true});
            skCircle(sketch, "E2.3.2.17", {"center": v(103.92, 80) * mm, "radius": 7.5 * mm, "construction": true});
            skLineSegment(sketch, "E2.3.2.18", {"start": v(108.25, 87.5) * mm, "end": v(112.58, 80) * mm});
            skPoint(sketch, "E2.3.2.19", {"position": v(103.92, 87.5) * mm});
            skLineSegment(sketch, "E2.3.2.20", {"start": v(125.57, 77.5) * mm, "end": v(129.9, 70) * mm});
            skLineSegment(sketch, "E2.3.2.21", {"start": v(112.58, 90) * mm, "end": v(116.91, 97.5) * mm});
            skLineSegment(sketch, "E2.3.2.22", {"start": v(99.59, 87.5) * mm, "end": v(108.25, 87.5) * mm});
            skLineSegment(sketch, "E2.3.2.23", {"start": v(116.91, 97.5) * mm, "end": v(125.57, 97.5) * mm});
            skLineSegment(sketch, "E2.3.2.24", {"start": v(116.91, 77.5) * mm, "end": v(125.57, 77.5) * mm});
            skLineSegment(sketch, "E2.3.3.0", {"start": v(112.58, 110) * mm, "end": v(116.91, 117.5) * mm});
            skLineSegment(sketch, "E2.3.3.2", {"start": v(95.26, 120) * mm, "end": v(99.59, 127.5) * mm});
            skLineSegment(sketch, "E2.3.3.4", {"start": v(99.59, 112.5) * mm, "end": v(95.26, 120) * mm});
            skLineSegment(sketch, "E2.3.3.5", {"start": v(108.25, 112.5) * mm, "end": v(99.59, 112.5) * mm});
            skLineSegment(sketch, "E2.3.3.6", {"start": v(125.57, 122.5) * mm, "end": v(116.91, 122.5) * mm});
            skLineSegment(sketch, "E2.3.3.7", {"start": v(112.58, 120) * mm, "end": v(108.25, 112.5) * mm});
            skLineSegment(sketch, "E2.3.3.8", {"start": v(116.91, 122.5) * mm, "end": v(112.58, 130) * mm});
            skCircle(sketch, "E2.3.3.9", {"center": v(121.24, 110) * mm, "radius": 7.5 * mm, "construction": true});
            skLineSegment(sketch, "E2.3.3.10", {"start": v(116.91, 102.5) * mm, "end": v(112.58, 110) * mm});
            skLineSegment(sketch, "E2.3.3.11", {"start": v(125.57, 102.5) * mm, "end": v(116.91, 102.5) * mm});
            skLineSegment(sketch, "E2.3.3.12", {"start": v(129.9, 110) * mm, "end": v(125.57, 102.5) * mm});
            skLineSegment(sketch, "E2.3.3.13", {"start": v(95.26, 120) * mm, "end": v(112.58, 120) * mm, "construction": true});
            skLineSegment(sketch, "E2.3.3.14", {"start": v(129.9, 130) * mm, "end": v(125.57, 122.5) * mm});
            skPoint(sketch, "E2.3.3.15", {"position": v(121.24, 117.5) * mm});
            skCircle(sketch, "E2.3.3.17", {"center": v(103.92, 120) * mm, "radius": 7.5 * mm, "construction": true});
            skLineSegment(sketch, "E2.3.3.18", {"start": v(108.25, 127.5) * mm, "end": v(112.58, 120) * mm});
            skLineSegment(sketch, "E2.3.3.20", {"start": v(125.57, 117.5) * mm, "end": v(129.9, 110) * mm});
            skLineSegment(sketch, "E2.3.3.22", {"start": v(99.59, 127.5) * mm, "end": v(108.25, 127.5) * mm});
            skLineSegment(sketch, "E2.3.3.24", {"start": v(116.91, 117.5) * mm, "end": v(125.57, 117.5) * mm});
            skLineSegment(sketch, "E2.4.0.0", {"start": v(147.22, -10) * mm, "end": v(151.55, -2.5) * mm});
            skLineSegment(sketch, "E2.4.0.1", {"start": v(160.21, 17.5) * mm, "end": v(164.54, 10) * mm});
            skLineSegment(sketch, "E2.4.0.2", {"start": v(129.9, 0) * mm, "end": v(134.23, 7.5) * mm});
            skPoint(sketch, "E2.4.0.3", {"position": v(155.88, 17.5) * mm});
            skLineSegment(sketch, "E2.4.0.4", {"start": v(134.23, -7.5) * mm, "end": v(129.9, 0) * mm});
            skLineSegment(sketch, "E2.4.0.5", {"start": v(142.9, -7.5) * mm, "end": v(134.23, -7.5) * mm});
            skLineSegment(sketch, "E2.4.0.6", {"start": v(160.21, 2.5) * mm, "end": v(151.55, 2.5) * mm});
            skLineSegment(sketch, "E2.4.0.7", {"start": v(147.22, 0) * mm, "end": v(142.9, -7.5) * mm});
            skLineSegment(sketch, "E2.4.0.8", {"start": v(151.55, 2.5) * mm, "end": v(147.22, 10) * mm});
            skLineSegment(sketch, "E2.4.0.13", {"start": v(129.9, 0) * mm, "end": v(147.22, 0) * mm, "construction": true});
            skLineSegment(sketch, "E2.4.0.14", {"start": v(164.54, 10) * mm, "end": v(160.21, 2.5) * mm});
            skPoint(sketch, "E2.4.0.15", {"position": v(155.88, -2.5) * mm});
            skCircle(sketch, "E2.4.0.16", {"center": v(155.88, 10) * mm, "radius": 7.5 * mm, "construction": true});
            skCircle(sketch, "E2.4.0.17", {"center": v(138.56, 0) * mm, "radius": 7.5 * mm, "construction": true});
            skLineSegment(sketch, "E2.4.0.18", {"start": v(142.9, 7.5) * mm, "end": v(147.22, 0) * mm});
            skPoint(sketch, "E2.4.0.19", {"position": v(138.56, 7.5) * mm});
            skLineSegment(sketch, "E2.4.0.20", {"start": v(160.21, -2.5) * mm, "end": v(164.54, -10) * mm});
            skLineSegment(sketch, "E2.4.0.21", {"start": v(147.22, 10) * mm, "end": v(151.55, 17.5) * mm});
            skLineSegment(sketch, "E2.4.0.22", {"start": v(134.23, 7.5) * mm, "end": v(142.9, 7.5) * mm});
            skLineSegment(sketch, "E2.4.0.23", {"start": v(151.55, 17.5) * mm, "end": v(160.21, 17.5) * mm});
            skLineSegment(sketch, "E2.4.0.24", {"start": v(151.55, -2.5) * mm, "end": v(160.21, -2.5) * mm});
            skLineSegment(sketch, "E2.4.1.0", {"start": v(147.22, 30) * mm, "end": v(151.55, 37.5) * mm});
            skLineSegment(sketch, "E2.4.1.1", {"start": v(160.21, 57.5) * mm, "end": v(164.54, 50) * mm});
            skLineSegment(sketch, "E2.4.1.2", {"start": v(129.9, 40) * mm, "end": v(134.23, 47.5) * mm});
            skPoint(sketch, "E2.4.1.3", {"position": v(155.88, 57.5) * mm});
            skLineSegment(sketch, "E2.4.1.4", {"start": v(134.23, 32.5) * mm, "end": v(129.9, 40) * mm});
            skLineSegment(sketch, "E2.4.1.5", {"start": v(142.9, 32.5) * mm, "end": v(134.23, 32.5) * mm});
            skLineSegment(sketch, "E2.4.1.6", {"start": v(160.21, 42.5) * mm, "end": v(151.55, 42.5) * mm});
            skLineSegment(sketch, "E2.4.1.7", {"start": v(147.22, 40) * mm, "end": v(142.9, 32.5) * mm});
            skLineSegment(sketch, "E2.4.1.8", {"start": v(151.55, 42.5) * mm, "end": v(147.22, 50) * mm});
            skCircle(sketch, "E2.4.1.9", {"center": v(155.88, 30) * mm, "radius": 7.5 * mm, "construction": true});
            skLineSegment(sketch, "E2.4.1.10", {"start": v(151.55, 22.5) * mm, "end": v(147.22, 30) * mm});
            skLineSegment(sketch, "E2.4.1.11", {"start": v(160.21, 22.5) * mm, "end": v(151.55, 22.5) * mm});
            skLineSegment(sketch, "E2.4.1.12", {"start": v(164.54, 30) * mm, "end": v(160.21, 22.5) * mm});
            skLineSegment(sketch, "E2.4.1.13", {"start": v(129.9, 40) * mm, "end": v(147.22, 40) * mm, "construction": true});
            skLineSegment(sketch, "E2.4.1.14", {"start": v(164.54, 50) * mm, "end": v(160.21, 42.5) * mm});
            skPoint(sketch, "E2.4.1.15", {"position": v(155.88, 37.5) * mm});
            skCircle(sketch, "E2.4.1.16", {"center": v(155.88, 50) * mm, "radius": 7.5 * mm, "construction": true});
            skCircle(sketch, "E2.4.1.17", {"center": v(138.56, 40) * mm, "radius": 7.5 * mm, "construction": true});
            skLineSegment(sketch, "E2.4.1.18", {"start": v(142.9, 47.5) * mm, "end": v(147.22, 40) * mm});
            skPoint(sketch, "E2.4.1.19", {"position": v(138.56, 47.5) * mm});
            skLineSegment(sketch, "E2.4.1.20", {"start": v(160.21, 37.5) * mm, "end": v(164.54, 30) * mm});
            skLineSegment(sketch, "E2.4.1.21", {"start": v(147.22, 50) * mm, "end": v(151.55, 57.5) * mm});
            skLineSegment(sketch, "E2.4.1.22", {"start": v(134.23, 47.5) * mm, "end": v(142.9, 47.5) * mm});
            skLineSegment(sketch, "E2.4.1.23", {"start": v(151.55, 57.5) * mm, "end": v(160.21, 57.5) * mm});
            skLineSegment(sketch, "E2.4.1.24", {"start": v(151.55, 37.5) * mm, "end": v(160.21, 37.5) * mm});
            skLineSegment(sketch, "E2.4.2.0", {"start": v(147.22, 70) * mm, "end": v(151.55, 77.5) * mm});
            skLineSegment(sketch, "E2.4.2.1", {"start": v(160.21, 97.5) * mm, "end": v(164.54, 90) * mm});
            skLineSegment(sketch, "E2.4.2.2", {"start": v(129.9, 80) * mm, "end": v(134.23, 87.5) * mm});
            skPoint(sketch, "E2.4.2.3", {"position": v(155.88, 97.5) * mm});
            skLineSegment(sketch, "E2.4.2.4", {"start": v(134.23, 72.5) * mm, "end": v(129.9, 80) * mm});
            skLineSegment(sketch, "E2.4.2.5", {"start": v(142.9, 72.5) * mm, "end": v(134.23, 72.5) * mm});
            skLineSegment(sketch, "E2.4.2.6", {"start": v(160.21, 82.5) * mm, "end": v(151.55, 82.5) * mm});
            skLineSegment(sketch, "E2.4.2.7", {"start": v(147.22, 80) * mm, "end": v(142.9, 72.5) * mm});
            skLineSegment(sketch, "E2.4.2.8", {"start": v(151.55, 82.5) * mm, "end": v(147.22, 90) * mm});
            skCircle(sketch, "E2.4.2.9", {"center": v(155.88, 70) * mm, "radius": 7.5 * mm, "construction": true});
            skLineSegment(sketch, "E2.4.2.10", {"start": v(151.55, 62.5) * mm, "end": v(147.22, 70) * mm});
            skLineSegment(sketch, "E2.4.2.11", {"start": v(160.21, 62.5) * mm, "end": v(151.55, 62.5) * mm});
            skLineSegment(sketch, "E2.4.2.12", {"start": v(164.54, 70) * mm, "end": v(160.21, 62.5) * mm});
            skLineSegment(sketch, "E2.4.2.13", {"start": v(129.9, 80) * mm, "end": v(147.22, 80) * mm, "construction": true});
            skLineSegment(sketch, "E2.4.2.14", {"start": v(164.54, 90) * mm, "end": v(160.21, 82.5) * mm});
            skPoint(sketch, "E2.4.2.15", {"position": v(155.88, 77.5) * mm});
            skCircle(sketch, "E2.4.2.16", {"center": v(155.88, 90) * mm, "radius": 7.5 * mm, "construction": true});
            skCircle(sketch, "E2.4.2.17", {"center": v(138.56, 80) * mm, "radius": 7.5 * mm, "construction": true});
            skLineSegment(sketch, "E2.4.2.18", {"start": v(142.9, 87.5) * mm, "end": v(147.22, 80) * mm});
            skPoint(sketch, "E2.4.2.19", {"position": v(138.56, 87.5) * mm});
            skLineSegment(sketch, "E2.4.2.20", {"start": v(160.21, 77.5) * mm, "end": v(164.54, 70) * mm});
            skLineSegment(sketch, "E2.4.2.21", {"start": v(147.22, 90) * mm, "end": v(151.55, 97.5) * mm});
            skLineSegment(sketch, "E2.4.2.22", {"start": v(134.23, 87.5) * mm, "end": v(142.9, 87.5) * mm});
            skLineSegment(sketch, "E2.4.2.23", {"start": v(151.55, 97.5) * mm, "end": v(160.21, 97.5) * mm});
            skLineSegment(sketch, "E2.4.2.24", {"start": v(151.55, 77.5) * mm, "end": v(160.21, 77.5) * mm});
            skLineSegment(sketch, "E2.4.3.0", {"start": v(147.22, 110) * mm, "end": v(151.55, 117.5) * mm});
            skLineSegment(sketch, "E2.4.3.2", {"start": v(129.9, 120) * mm, "end": v(134.23, 127.5) * mm});
            skLineSegment(sketch, "E2.4.3.4", {"start": v(134.23, 112.5) * mm, "end": v(129.9, 120) * mm});
            skLineSegment(sketch, "E2.4.3.5", {"start": v(142.9, 112.5) * mm, "end": v(134.23, 112.5) * mm});
            skLineSegment(sketch, "E2.4.3.6", {"start": v(160.21, 122.5) * mm, "end": v(151.55, 122.5) * mm});
            skLineSegment(sketch, "E2.4.3.7", {"start": v(147.22, 120) * mm, "end": v(142.9, 112.5) * mm});
            skLineSegment(sketch, "E2.4.3.8", {"start": v(151.55, 122.5) * mm, "end": v(147.22, 130) * mm});
            skCircle(sketch, "E2.4.3.9", {"center": v(155.88, 110) * mm, "radius": 7.5 * mm, "construction": true});
            skLineSegment(sketch, "E2.4.3.10", {"start": v(151.55, 102.5) * mm, "end": v(147.22, 110) * mm});
            skLineSegment(sketch, "E2.4.3.11", {"start": v(160.21, 102.5) * mm, "end": v(151.55, 102.5) * mm});
            skLineSegment(sketch, "E2.4.3.12", {"start": v(164.54, 110) * mm, "end": v(160.21, 102.5) * mm});
            skLineSegment(sketch, "E2.4.3.13", {"start": v(129.9, 120) * mm, "end": v(147.22, 120) * mm, "construction": true});
            skPoint(sketch, "E2.4.3.15", {"position": v(155.88, 117.5) * mm});
            skCircle(sketch, "E2.4.3.17", {"center": v(138.56, 120) * mm, "radius": 7.5 * mm, "construction": true});
            skLineSegment(sketch, "E2.4.3.18", {"start": v(142.9, 127.5) * mm, "end": v(147.22, 120) * mm});
            skLineSegment(sketch, "E2.4.3.20", {"start": v(160.21, 117.5) * mm, "end": v(164.54, 110) * mm});
            skLineSegment(sketch, "E2.4.3.22", {"start": v(134.23, 127.5) * mm, "end": v(142.9, 127.5) * mm});
            skLineSegment(sketch, "E2.4.3.24", {"start": v(151.55, 117.5) * mm, "end": v(160.21, 117.5) * mm});
            skLineSegment(sketch, "E2.5.0.0", {"start": v(181.86, -10) * mm, "end": v(186.2, -2.5) * mm});
            skLineSegment(sketch, "E2.5.0.1", {"start": v(194.85, 17.5) * mm, "end": v(199.18, 10) * mm});
            skLineSegment(sketch, "E2.5.0.2", {"start": v(164.54, 0) * mm, "end": v(168.87, 7.5) * mm});
            skPoint(sketch, "E2.5.0.3", {"position": v(190.52, 17.5) * mm});
            skLineSegment(sketch, "E2.5.0.4", {"start": v(168.87, -7.5) * mm, "end": v(164.54, 0) * mm});
            skLineSegment(sketch, "E2.5.0.5", {"start": v(177.53, -7.5) * mm, "end": v(168.87, -7.5) * mm});
            skLineSegment(sketch, "E2.5.0.6", {"start": v(194.85, 2.5) * mm, "end": v(186.2, 2.5) * mm});
            skLineSegment(sketch, "E2.5.0.7", {"start": v(181.86, 0) * mm, "end": v(177.53, -7.5) * mm});
            skLineSegment(sketch, "E2.5.0.8", {"start": v(186.2, 2.5) * mm, "end": v(181.86, 10) * mm});
            skLineSegment(sketch, "E2.5.0.13", {"start": v(164.54, 0) * mm, "end": v(181.86, 0) * mm, "construction": true});
            skLineSegment(sketch, "E2.5.0.14", {"start": v(199.18, 10) * mm, "end": v(194.85, 2.5) * mm});
            skPoint(sketch, "E2.5.0.15", {"position": v(190.52, -2.5) * mm});
            skCircle(sketch, "E2.5.0.16", {"center": v(190.52, 10) * mm, "radius": 7.5 * mm, "construction": true});
            skCircle(sketch, "E2.5.0.17", {"center": v(173.2, 0) * mm, "radius": 7.5 * mm, "construction": true});
            skLineSegment(sketch, "E2.5.0.18", {"start": v(177.53, 7.5) * mm, "end": v(181.86, 0) * mm});
            skPoint(sketch, "E2.5.0.19", {"position": v(173.2, 7.5) * mm});
            skLineSegment(sketch, "E2.5.0.20", {"start": v(194.85, -2.5) * mm, "end": v(199.18, -10) * mm});
            skLineSegment(sketch, "E2.5.0.21", {"start": v(181.86, 10) * mm, "end": v(186.2, 17.5) * mm});
            skLineSegment(sketch, "E2.5.0.22", {"start": v(168.87, 7.5) * mm, "end": v(177.53, 7.5) * mm});
            skLineSegment(sketch, "E2.5.0.23", {"start": v(186.2, 17.5) * mm, "end": v(194.85, 17.5) * mm});
            skLineSegment(sketch, "E2.5.0.24", {"start": v(186.2, -2.5) * mm, "end": v(194.85, -2.5) * mm});
            skLineSegment(sketch, "E2.5.1.0", {"start": v(181.86, 30) * mm, "end": v(186.2, 37.5) * mm});
            skLineSegment(sketch, "E2.5.1.1", {"start": v(194.85, 57.5) * mm, "end": v(199.18, 50) * mm});
            skLineSegment(sketch, "E2.5.1.2", {"start": v(164.54, 40) * mm, "end": v(168.87, 47.5) * mm});
            skPoint(sketch, "E2.5.1.3", {"position": v(190.52, 57.5) * mm});
            skLineSegment(sketch, "E2.5.1.4", {"start": v(168.87, 32.5) * mm, "end": v(164.54, 40) * mm});
            skLineSegment(sketch, "E2.5.1.5", {"start": v(177.53, 32.5) * mm, "end": v(168.87, 32.5) * mm});
            skLineSegment(sketch, "E2.5.1.6", {"start": v(194.85, 42.5) * mm, "end": v(186.2, 42.5) * mm});
            skLineSegment(sketch, "E2.5.1.7", {"start": v(181.86, 40) * mm, "end": v(177.53, 32.5) * mm});
            skLineSegment(sketch, "E2.5.1.8", {"start": v(186.2, 42.5) * mm, "end": v(181.86, 50) * mm});
            skCircle(sketch, "E2.5.1.9", {"center": v(190.52, 30) * mm, "radius": 7.5 * mm, "construction": true});
            skLineSegment(sketch, "E2.5.1.10", {"start": v(186.2, 22.5) * mm, "end": v(181.86, 30) * mm});
            skLineSegment(sketch, "E2.5.1.11", {"start": v(194.85, 22.5) * mm, "end": v(186.2, 22.5) * mm});
            skLineSegment(sketch, "E2.5.1.12", {"start": v(199.18, 30) * mm, "end": v(194.85, 22.5) * mm});
            skLineSegment(sketch, "E2.5.1.13", {"start": v(164.54, 40) * mm, "end": v(181.86, 40) * mm, "construction": true});
            skLineSegment(sketch, "E2.5.1.14", {"start": v(199.18, 50) * mm, "end": v(194.85, 42.5) * mm});
            skPoint(sketch, "E2.5.1.15", {"position": v(190.52, 37.5) * mm});
            skCircle(sketch, "E2.5.1.16", {"center": v(190.52, 50) * mm, "radius": 7.5 * mm, "construction": true});
            skCircle(sketch, "E2.5.1.17", {"center": v(173.2, 40) * mm, "radius": 7.5 * mm, "construction": true});
            skLineSegment(sketch, "E2.5.1.18", {"start": v(177.53, 47.5) * mm, "end": v(181.86, 40) * mm});
            skPoint(sketch, "E2.5.1.19", {"position": v(173.2, 47.5) * mm});
            skLineSegment(sketch, "E2.5.1.20", {"start": v(194.85, 37.5) * mm, "end": v(199.18, 30) * mm});
            skLineSegment(sketch, "E2.5.1.21", {"start": v(181.86, 50) * mm, "end": v(186.2, 57.5) * mm});
            skLineSegment(sketch, "E2.5.1.22", {"start": v(168.87, 47.5) * mm, "end": v(177.53, 47.5) * mm});
            skLineSegment(sketch, "E2.5.1.23", {"start": v(186.2, 57.5) * mm, "end": v(194.85, 57.5) * mm});
            skLineSegment(sketch, "E2.5.1.24", {"start": v(186.2, 37.5) * mm, "end": v(194.85, 37.5) * mm});
            skLineSegment(sketch, "E2.5.2.0", {"start": v(181.86, 70) * mm, "end": v(186.2, 77.5) * mm});
            skLineSegment(sketch, "E2.5.2.1", {"start": v(194.85, 97.5) * mm, "end": v(199.18, 90) * mm});
            skLineSegment(sketch, "E2.5.2.2", {"start": v(164.54, 80) * mm, "end": v(168.87, 87.5) * mm});
            skPoint(sketch, "E2.5.2.3", {"position": v(190.52, 97.5) * mm});
            skLineSegment(sketch, "E2.5.2.4", {"start": v(168.87, 72.5) * mm, "end": v(164.54, 80) * mm});
            skLineSegment(sketch, "E2.5.2.5", {"start": v(177.53, 72.5) * mm, "end": v(168.87, 72.5) * mm});
            skLineSegment(sketch, "E2.5.2.6", {"start": v(194.85, 82.5) * mm, "end": v(186.2, 82.5) * mm});
            skLineSegment(sketch, "E2.5.2.7", {"start": v(181.86, 80) * mm, "end": v(177.53, 72.5) * mm});
            skLineSegment(sketch, "E2.5.2.8", {"start": v(186.2, 82.5) * mm, "end": v(181.86, 90) * mm});
            skCircle(sketch, "E2.5.2.9", {"center": v(190.52, 70) * mm, "radius": 7.5 * mm, "construction": true});
            skLineSegment(sketch, "E2.5.2.10", {"start": v(186.2, 62.5) * mm, "end": v(181.86, 70) * mm});
            skLineSegment(sketch, "E2.5.2.11", {"start": v(194.85, 62.5) * mm, "end": v(186.2, 62.5) * mm});
            skLineSegment(sketch, "E2.5.2.12", {"start": v(199.18, 70) * mm, "end": v(194.85, 62.5) * mm});
            skLineSegment(sketch, "E2.5.2.13", {"start": v(164.54, 80) * mm, "end": v(181.86, 80) * mm, "construction": true});
            skLineSegment(sketch, "E2.5.2.14", {"start": v(199.18, 90) * mm, "end": v(194.85, 82.5) * mm});
            skPoint(sketch, "E2.5.2.15", {"position": v(190.52, 77.5) * mm});
            skCircle(sketch, "E2.5.2.16", {"center": v(190.52, 90) * mm, "radius": 7.5 * mm, "construction": true});
            skCircle(sketch, "E2.5.2.17", {"center": v(173.2, 80) * mm, "radius": 7.5 * mm, "construction": true});
            skLineSegment(sketch, "E2.5.2.18", {"start": v(177.53, 87.5) * mm, "end": v(181.86, 80) * mm});
            skPoint(sketch, "E2.5.2.19", {"position": v(173.2, 87.5) * mm});
            skLineSegment(sketch, "E2.5.2.20", {"start": v(194.85, 77.5) * mm, "end": v(199.18, 70) * mm});
            skLineSegment(sketch, "E2.5.2.21", {"start": v(181.86, 90) * mm, "end": v(186.2, 97.5) * mm});
            skLineSegment(sketch, "E2.5.2.22", {"start": v(168.87, 87.5) * mm, "end": v(177.53, 87.5) * mm});
            skLineSegment(sketch, "E2.5.2.23", {"start": v(186.2, 97.5) * mm, "end": v(194.85, 97.5) * mm});
            skLineSegment(sketch, "E2.5.2.24", {"start": v(186.2, 77.5) * mm, "end": v(194.85, 77.5) * mm});
            skLineSegment(sketch, "E2.5.3.0", {"start": v(181.86, 110) * mm, "end": v(186.2, 117.5) * mm});
            skLineSegment(sketch, "E2.5.3.2", {"start": v(164.54, 120) * mm, "end": v(168.87, 127.5) * mm});
            skLineSegment(sketch, "E2.5.3.4", {"start": v(168.87, 112.5) * mm, "end": v(164.54, 120) * mm});
            skLineSegment(sketch, "E2.5.3.5", {"start": v(177.53, 112.5) * mm, "end": v(168.87, 112.5) * mm});
            skLineSegment(sketch, "E2.5.3.6", {"start": v(194.85, 122.5) * mm, "end": v(186.2, 122.5) * mm});
            skLineSegment(sketch, "E2.5.3.7", {"start": v(181.86, 120) * mm, "end": v(177.53, 112.5) * mm});
            skLineSegment(sketch, "E2.5.3.8", {"start": v(186.2, 122.5) * mm, "end": v(181.86, 130) * mm});
            skCircle(sketch, "E2.5.3.9", {"center": v(190.52, 110) * mm, "radius": 7.5 * mm, "construction": true});
            skLineSegment(sketch, "E2.5.3.10", {"start": v(186.2, 102.5) * mm, "end": v(181.86, 110) * mm});
            skLineSegment(sketch, "E2.5.3.11", {"start": v(194.85, 102.5) * mm, "end": v(186.2, 102.5) * mm});
            skLineSegment(sketch, "E2.5.3.12", {"start": v(199.18, 110) * mm, "end": v(194.85, 102.5) * mm});
            skLineSegment(sketch, "E2.5.3.13", {"start": v(164.54, 120) * mm, "end": v(181.86, 120) * mm, "construction": true});
            skLineSegment(sketch, "E2.5.3.14", {"start": v(199.18, 130) * mm, "end": v(194.85, 122.5) * mm});
            skPoint(sketch, "E2.5.3.15", {"position": v(190.52, 117.5) * mm});
            skCircle(sketch, "E2.5.3.17", {"center": v(173.2, 120) * mm, "radius": 7.5 * mm, "construction": true});
            skLineSegment(sketch, "E2.5.3.18", {"start": v(177.53, 127.5) * mm, "end": v(181.86, 120) * mm});
            skLineSegment(sketch, "E2.5.3.20", {"start": v(194.85, 117.5) * mm, "end": v(199.18, 110) * mm});
            skLineSegment(sketch, "E2.5.3.22", {"start": v(168.87, 127.5) * mm, "end": v(177.53, 127.5) * mm});
            skLineSegment(sketch, "E2.5.3.24", {"start": v(186.2, 117.5) * mm, "end": v(194.85, 117.5) * mm});
            skLineSegment(sketch, "E2.6.0.0", {"start": v(216.5, -10) * mm, "end": v(220.83, -2.5) * mm});
            skLineSegment(sketch, "E2.6.0.1", {"start": v(229.5, 17.5) * mm, "end": v(233.82, 10) * mm});
            skLineSegment(sketch, "E2.6.0.2", {"start": v(199.18, 0) * mm, "end": v(203.5, 7.5) * mm});
            skPoint(sketch, "E2.6.0.3", {"position": v(225.16, 17.5) * mm});
            skLineSegment(sketch, "E2.6.0.4", {"start": v(203.5, -7.5) * mm, "end": v(199.18, 0) * mm});
            skLineSegment(sketch, "E2.6.0.5", {"start": v(212.17, -7.5) * mm, "end": v(203.5, -7.5) * mm});
            skLineSegment(sketch, "E2.6.0.6", {"start": v(229.5, 2.5) * mm, "end": v(220.83, 2.5) * mm});
            skLineSegment(sketch, "E2.6.0.7", {"start": v(216.5, 0) * mm, "end": v(212.17, -7.5) * mm});
            skLineSegment(sketch, "E2.6.0.8", {"start": v(220.83, 2.5) * mm, "end": v(216.5, 10) * mm});
            skLineSegment(sketch, "E2.6.0.13", {"start": v(199.18, 0) * mm, "end": v(216.5, 0) * mm, "construction": true});
            skLineSegment(sketch, "E2.6.0.14", {"start": v(233.82, 10) * mm, "end": v(229.5, 2.5) * mm});
            skPoint(sketch, "E2.6.0.15", {"position": v(225.16, -2.5) * mm});
            skCircle(sketch, "E2.6.0.16", {"center": v(225.16, 10) * mm, "radius": 7.5 * mm, "construction": true});
            skCircle(sketch, "E2.6.0.17", {"center": v(207.84, 0) * mm, "radius": 7.5 * mm, "construction": true});
            skLineSegment(sketch, "E2.6.0.18", {"start": v(212.17, 7.5) * mm, "end": v(216.5, 0) * mm});
            skPoint(sketch, "E2.6.0.19", {"position": v(207.84, 7.5) * mm});
            skLineSegment(sketch, "E2.6.0.20", {"start": v(229.5, -2.5) * mm, "end": v(233.82, -10) * mm});
            skLineSegment(sketch, "E2.6.0.21", {"start": v(216.5, 10) * mm, "end": v(220.83, 17.5) * mm});
            skLineSegment(sketch, "E2.6.0.22", {"start": v(203.5, 7.5) * mm, "end": v(212.17, 7.5) * mm});
            skLineSegment(sketch, "E2.6.0.23", {"start": v(220.83, 17.5) * mm, "end": v(229.5, 17.5) * mm});
            skLineSegment(sketch, "E2.6.0.24", {"start": v(220.83, -2.5) * mm, "end": v(229.5, -2.5) * mm});
            skLineSegment(sketch, "E2.6.1.0", {"start": v(216.5, 30) * mm, "end": v(220.83, 37.5) * mm});
            skLineSegment(sketch, "E2.6.1.1", {"start": v(229.5, 57.5) * mm, "end": v(233.82, 50) * mm});
            skLineSegment(sketch, "E2.6.1.2", {"start": v(199.18, 40) * mm, "end": v(203.5, 47.5) * mm});
            skPoint(sketch, "E2.6.1.3", {"position": v(225.16, 57.5) * mm});
            skLineSegment(sketch, "E2.6.1.4", {"start": v(203.5, 32.5) * mm, "end": v(199.18, 40) * mm});
            skLineSegment(sketch, "E2.6.1.5", {"start": v(212.17, 32.5) * mm, "end": v(203.5, 32.5) * mm});
            skLineSegment(sketch, "E2.6.1.6", {"start": v(229.5, 42.5) * mm, "end": v(220.83, 42.5) * mm});
            skLineSegment(sketch, "E2.6.1.7", {"start": v(216.5, 40) * mm, "end": v(212.17, 32.5) * mm});
            skLineSegment(sketch, "E2.6.1.8", {"start": v(220.83, 42.5) * mm, "end": v(216.5, 50) * mm});
            skCircle(sketch, "E2.6.1.9", {"center": v(225.16, 30) * mm, "radius": 7.5 * mm, "construction": true});
            skLineSegment(sketch, "E2.6.1.10", {"start": v(220.83, 22.5) * mm, "end": v(216.5, 30) * mm});
            skLineSegment(sketch, "E2.6.1.11", {"start": v(229.5, 22.5) * mm, "end": v(220.83, 22.5) * mm});
            skLineSegment(sketch, "E2.6.1.12", {"start": v(233.82, 30) * mm, "end": v(229.5, 22.5) * mm});
            skLineSegment(sketch, "E2.6.1.13", {"start": v(199.18, 40) * mm, "end": v(216.5, 40) * mm, "construction": true});
            skLineSegment(sketch, "E2.6.1.14", {"start": v(233.82, 50) * mm, "end": v(229.5, 42.5) * mm});
            skPoint(sketch, "E2.6.1.15", {"position": v(225.16, 37.5) * mm});
            skCircle(sketch, "E2.6.1.16", {"center": v(225.16, 50) * mm, "radius": 7.5 * mm, "construction": true});
            skCircle(sketch, "E2.6.1.17", {"center": v(207.84, 40) * mm, "radius": 7.5 * mm, "construction": true});
            skLineSegment(sketch, "E2.6.1.18", {"start": v(212.17, 47.5) * mm, "end": v(216.5, 40) * mm});
            skPoint(sketch, "E2.6.1.19", {"position": v(207.84, 47.5) * mm});
            skLineSegment(sketch, "E2.6.1.20", {"start": v(229.5, 37.5) * mm, "end": v(233.82, 30) * mm});
            skLineSegment(sketch, "E2.6.1.21", {"start": v(216.5, 50) * mm, "end": v(220.83, 57.5) * mm});
            skLineSegment(sketch, "E2.6.1.22", {"start": v(203.5, 47.5) * mm, "end": v(212.17, 47.5) * mm});
            skLineSegment(sketch, "E2.6.1.23", {"start": v(220.83, 57.5) * mm, "end": v(229.5, 57.5) * mm});
            skLineSegment(sketch, "E2.6.1.24", {"start": v(220.83, 37.5) * mm, "end": v(229.5, 37.5) * mm});
            skLineSegment(sketch, "E2.6.2.0", {"start": v(216.5, 70) * mm, "end": v(220.83, 77.5) * mm});
            skLineSegment(sketch, "E2.6.2.1", {"start": v(229.5, 97.5) * mm, "end": v(233.82, 90) * mm});
            skLineSegment(sketch, "E2.6.2.2", {"start": v(199.18, 80) * mm, "end": v(203.5, 87.5) * mm});
            skPoint(sketch, "E2.6.2.3", {"position": v(225.16, 97.5) * mm});
            skLineSegment(sketch, "E2.6.2.4", {"start": v(203.5, 72.5) * mm, "end": v(199.18, 80) * mm});
            skLineSegment(sketch, "E2.6.2.5", {"start": v(212.17, 72.5) * mm, "end": v(203.5, 72.5) * mm});
            skLineSegment(sketch, "E2.6.2.6", {"start": v(229.5, 82.5) * mm, "end": v(220.83, 82.5) * mm});
            skLineSegment(sketch, "E2.6.2.7", {"start": v(216.5, 80) * mm, "end": v(212.17, 72.5) * mm});
            skLineSegment(sketch, "E2.6.2.8", {"start": v(220.83, 82.5) * mm, "end": v(216.5, 90) * mm});
            skCircle(sketch, "E2.6.2.9", {"center": v(225.16, 70) * mm, "radius": 7.5 * mm, "construction": true});
            skLineSegment(sketch, "E2.6.2.10", {"start": v(220.83, 62.5) * mm, "end": v(216.5, 70) * mm});
            skLineSegment(sketch, "E2.6.2.11", {"start": v(229.5, 62.5) * mm, "end": v(220.83, 62.5) * mm});
            skLineSegment(sketch, "E2.6.2.12", {"start": v(233.82, 70) * mm, "end": v(229.5, 62.5) * mm});
            skLineSegment(sketch, "E2.6.2.13", {"start": v(199.18, 80) * mm, "end": v(216.5, 80) * mm, "construction": true});
            skLineSegment(sketch, "E2.6.2.14", {"start": v(233.82, 90) * mm, "end": v(229.5, 82.5) * mm});
            skPoint(sketch, "E2.6.2.15", {"position": v(225.16, 77.5) * mm});
            skCircle(sketch, "E2.6.2.16", {"center": v(225.16, 90) * mm, "radius": 7.5 * mm, "construction": true});
            skCircle(sketch, "E2.6.2.17", {"center": v(207.84, 80) * mm, "radius": 7.5 * mm, "construction": true});
            skLineSegment(sketch, "E2.6.2.18", {"start": v(212.17, 87.5) * mm, "end": v(216.5, 80) * mm});
            skPoint(sketch, "E2.6.2.19", {"position": v(207.84, 87.5) * mm});
            skLineSegment(sketch, "E2.6.2.20", {"start": v(229.5, 77.5) * mm, "end": v(233.82, 70) * mm});
            skLineSegment(sketch, "E2.6.2.21", {"start": v(216.5, 90) * mm, "end": v(220.83, 97.5) * mm});
            skLineSegment(sketch, "E2.6.2.22", {"start": v(203.5, 87.5) * mm, "end": v(212.17, 87.5) * mm});
            skLineSegment(sketch, "E2.6.2.23", {"start": v(220.83, 97.5) * mm, "end": v(229.5, 97.5) * mm});
            skLineSegment(sketch, "E2.6.2.24", {"start": v(220.83, 77.5) * mm, "end": v(229.5, 77.5) * mm});
            skLineSegment(sketch, "E2.6.3.0", {"start": v(216.5, 110) * mm, "end": v(220.83, 117.5) * mm});
            skLineSegment(sketch, "E2.6.3.2", {"start": v(199.18, 120) * mm, "end": v(203.5, 127.5) * mm});
            skLineSegment(sketch, "E2.6.3.4", {"start": v(203.5, 112.5) * mm, "end": v(199.18, 120) * mm});
            skLineSegment(sketch, "E2.6.3.5", {"start": v(212.17, 112.5) * mm, "end": v(203.5, 112.5) * mm});
            skLineSegment(sketch, "E2.6.3.6", {"start": v(229.5, 122.5) * mm, "end": v(220.83, 122.5) * mm});
            skLineSegment(sketch, "E2.6.3.7", {"start": v(216.5, 120) * mm, "end": v(212.17, 112.5) * mm});
            skLineSegment(sketch, "E2.6.3.8", {"start": v(220.83, 122.5) * mm, "end": v(216.5, 130) * mm});
            skCircle(sketch, "E2.6.3.9", {"center": v(225.16, 110) * mm, "radius": 7.5 * mm, "construction": true});
            skLineSegment(sketch, "E2.6.3.10", {"start": v(220.83, 102.5) * mm, "end": v(216.5, 110) * mm});
            skLineSegment(sketch, "E2.6.3.11", {"start": v(229.5, 102.5) * mm, "end": v(220.83, 102.5) * mm});
            skLineSegment(sketch, "E2.6.3.12", {"start": v(233.82, 110) * mm, "end": v(229.5, 102.5) * mm});
            skLineSegment(sketch, "E2.6.3.13", {"start": v(199.18, 120) * mm, "end": v(216.5, 120) * mm, "construction": true});
            skLineSegment(sketch, "E2.6.3.14", {"start": v(233.82, 130) * mm, "end": v(229.5, 122.5) * mm});
            skPoint(sketch, "E2.6.3.15", {"position": v(225.16, 117.5) * mm});
            skCircle(sketch, "E2.6.3.17", {"center": v(207.84, 120) * mm, "radius": 7.5 * mm, "construction": true});
            skLineSegment(sketch, "E2.6.3.18", {"start": v(212.17, 127.5) * mm, "end": v(216.5, 120) * mm});
            skLineSegment(sketch, "E2.6.3.20", {"start": v(229.5, 117.5) * mm, "end": v(233.82, 110) * mm});
            skLineSegment(sketch, "E2.6.3.22", {"start": v(203.5, 127.5) * mm, "end": v(212.17, 127.5) * mm});
            skLineSegment(sketch, "E2.6.3.24", {"start": v(220.83, 117.5) * mm, "end": v(229.5, 117.5) * mm});
            skLineSegment(sketch, "E2.7.0.0", {"start": v(251.14, -10) * mm, "end": v(255.47, -2.5) * mm});
            skLineSegment(sketch, "E2.7.0.1", {"start": v(264.13, 17.5) * mm, "end": v(268.46, 10) * mm});
            skLineSegment(sketch, "E2.7.0.2", {"start": v(233.82, 0) * mm, "end": v(238.15, 7.5) * mm});
            skPoint(sketch, "E2.7.0.3", {"position": v(259.8, 17.5) * mm});
            skLineSegment(sketch, "E2.7.0.4", {"start": v(238.15, -7.5) * mm, "end": v(233.82, 0) * mm});
            skLineSegment(sketch, "E2.7.0.5", {"start": v(246.81, -7.5) * mm, "end": v(238.15, -7.5) * mm});
            skLineSegment(sketch, "E2.7.0.6", {"start": v(264.13, 2.5) * mm, "end": v(255.47, 2.5) * mm});
            skLineSegment(sketch, "E2.7.0.7", {"start": v(251.14, 0) * mm, "end": v(246.81, -7.5) * mm});
            skLineSegment(sketch, "E2.7.0.8", {"start": v(255.47, 2.5) * mm, "end": v(251.14, 10) * mm});
            skLineSegment(sketch, "E2.7.0.13", {"start": v(233.82, 0) * mm, "end": v(251.14, 0) * mm, "construction": true});
            skLineSegment(sketch, "E2.7.0.14", {"start": v(268.46, 10) * mm, "end": v(264.13, 2.5) * mm});
            skPoint(sketch, "E2.7.0.15", {"position": v(259.8, -2.5) * mm});
            skCircle(sketch, "E2.7.0.16", {"center": v(259.8, 10) * mm, "radius": 7.5 * mm, "construction": true});
            skCircle(sketch, "E2.7.0.17", {"center": v(242.48, 0) * mm, "radius": 7.5 * mm, "construction": true});
            skLineSegment(sketch, "E2.7.0.18", {"start": v(246.81, 7.5) * mm, "end": v(251.14, 0) * mm});
            skPoint(sketch, "E2.7.0.19", {"position": v(242.48, 7.5) * mm});
            skLineSegment(sketch, "E2.7.0.20", {"start": v(264.13, -2.5) * mm, "end": v(268.46, -10) * mm});
            skLineSegment(sketch, "E2.7.0.21", {"start": v(251.14, 10) * mm, "end": v(255.47, 17.5) * mm});
            skLineSegment(sketch, "E2.7.0.22", {"start": v(238.15, 7.5) * mm, "end": v(246.81, 7.5) * mm});
            skLineSegment(sketch, "E2.7.0.23", {"start": v(255.47, 17.5) * mm, "end": v(264.13, 17.5) * mm});
            skLineSegment(sketch, "E2.7.0.24", {"start": v(255.47, -2.5) * mm, "end": v(264.13, -2.5) * mm});
            skLineSegment(sketch, "E2.7.1.0", {"start": v(251.14, 30) * mm, "end": v(255.47, 37.5) * mm});
            skLineSegment(sketch, "E2.7.1.1", {"start": v(264.13, 57.5) * mm, "end": v(268.46, 50) * mm});
            skLineSegment(sketch, "E2.7.1.2", {"start": v(233.82, 40) * mm, "end": v(238.15, 47.5) * mm});
            skPoint(sketch, "E2.7.1.3", {"position": v(259.8, 57.5) * mm});
            skLineSegment(sketch, "E2.7.1.4", {"start": v(238.15, 32.5) * mm, "end": v(233.82, 40) * mm});
            skLineSegment(sketch, "E2.7.1.5", {"start": v(246.81, 32.5) * mm, "end": v(238.15, 32.5) * mm});
            skLineSegment(sketch, "E2.7.1.6", {"start": v(264.13, 42.5) * mm, "end": v(255.47, 42.5) * mm});
            skLineSegment(sketch, "E2.7.1.7", {"start": v(251.14, 40) * mm, "end": v(246.81, 32.5) * mm});
            skLineSegment(sketch, "E2.7.1.8", {"start": v(255.47, 42.5) * mm, "end": v(251.14, 50) * mm});
            skCircle(sketch, "E2.7.1.9", {"center": v(259.8, 30) * mm, "radius": 7.5 * mm, "construction": true});
            skLineSegment(sketch, "E2.7.1.10", {"start": v(255.47, 22.5) * mm, "end": v(251.14, 30) * mm});
            skLineSegment(sketch, "E2.7.1.11", {"start": v(264.13, 22.5) * mm, "end": v(255.47, 22.5) * mm});
            skLineSegment(sketch, "E2.7.1.12", {"start": v(268.46, 30) * mm, "end": v(264.13, 22.5) * mm});
            skLineSegment(sketch, "E2.7.1.13", {"start": v(233.82, 40) * mm, "end": v(251.14, 40) * mm, "construction": true});
            skLineSegment(sketch, "E2.7.1.14", {"start": v(268.46, 50) * mm, "end": v(264.13, 42.5) * mm});
            skPoint(sketch, "E2.7.1.15", {"position": v(259.8, 37.5) * mm});
            skCircle(sketch, "E2.7.1.16", {"center": v(259.8, 50) * mm, "radius": 7.5 * mm, "construction": true});
            skCircle(sketch, "E2.7.1.17", {"center": v(242.48, 40) * mm, "radius": 7.5 * mm, "construction": true});
            skLineSegment(sketch, "E2.7.1.18", {"start": v(246.81, 47.5) * mm, "end": v(251.14, 40) * mm});
            skPoint(sketch, "E2.7.1.19", {"position": v(242.48, 47.5) * mm});
            skLineSegment(sketch, "E2.7.1.20", {"start": v(264.13, 37.5) * mm, "end": v(268.46, 30) * mm});
            skLineSegment(sketch, "E2.7.1.21", {"start": v(251.14, 50) * mm, "end": v(255.47, 57.5) * mm});
            skLineSegment(sketch, "E2.7.1.22", {"start": v(238.15, 47.5) * mm, "end": v(246.81, 47.5) * mm});
            skLineSegment(sketch, "E2.7.1.23", {"start": v(255.47, 57.5) * mm, "end": v(264.13, 57.5) * mm});
            skLineSegment(sketch, "E2.7.1.24", {"start": v(255.47, 37.5) * mm, "end": v(264.13, 37.5) * mm});
            skLineSegment(sketch, "E2.7.2.0", {"start": v(251.14, 70) * mm, "end": v(255.47, 77.5) * mm});
            skLineSegment(sketch, "E2.7.2.1", {"start": v(264.13, 97.5) * mm, "end": v(268.46, 90) * mm});
            skLineSegment(sketch, "E2.7.2.2", {"start": v(233.82, 80) * mm, "end": v(238.15, 87.5) * mm});
            skPoint(sketch, "E2.7.2.3", {"position": v(259.8, 97.5) * mm});
            skLineSegment(sketch, "E2.7.2.4", {"start": v(238.15, 72.5) * mm, "end": v(233.82, 80) * mm});
            skLineSegment(sketch, "E2.7.2.5", {"start": v(246.81, 72.5) * mm, "end": v(238.15, 72.5) * mm});
            skLineSegment(sketch, "E2.7.2.6", {"start": v(264.13, 82.5) * mm, "end": v(255.47, 82.5) * mm});
            skLineSegment(sketch, "E2.7.2.7", {"start": v(251.14, 80) * mm, "end": v(246.81, 72.5) * mm});
            skLineSegment(sketch, "E2.7.2.8", {"start": v(255.47, 82.5) * mm, "end": v(251.14, 90) * mm});
            skCircle(sketch, "E2.7.2.9", {"center": v(259.8, 70) * mm, "radius": 7.5 * mm, "construction": true});
            skLineSegment(sketch, "E2.7.2.10", {"start": v(255.47, 62.5) * mm, "end": v(251.14, 70) * mm});
            skLineSegment(sketch, "E2.7.2.11", {"start": v(264.13, 62.5) * mm, "end": v(255.47, 62.5) * mm});
            skLineSegment(sketch, "E2.7.2.12", {"start": v(268.46, 70) * mm, "end": v(264.13, 62.5) * mm});
            skLineSegment(sketch, "E2.7.2.13", {"start": v(233.82, 80) * mm, "end": v(251.14, 80) * mm, "construction": true});
            skLineSegment(sketch, "E2.7.2.14", {"start": v(268.46, 90) * mm, "end": v(264.13, 82.5) * mm});
            skPoint(sketch, "E2.7.2.15", {"position": v(259.8, 77.5) * mm});
            skCircle(sketch, "E2.7.2.16", {"center": v(259.8, 90) * mm, "radius": 7.5 * mm, "construction": true});
            skCircle(sketch, "E2.7.2.17", {"center": v(242.48, 80) * mm, "radius": 7.5 * mm, "construction": true});
            skLineSegment(sketch, "E2.7.2.18", {"start": v(246.81, 87.5) * mm, "end": v(251.14, 80) * mm});
            skPoint(sketch, "E2.7.2.19", {"position": v(242.48, 87.5) * mm});
            skLineSegment(sketch, "E2.7.2.20", {"start": v(264.13, 77.5) * mm, "end": v(268.46, 70) * mm});
            skLineSegment(sketch, "E2.7.2.21", {"start": v(251.14, 90) * mm, "end": v(255.47, 97.5) * mm});
            skLineSegment(sketch, "E2.7.2.22", {"start": v(238.15, 87.5) * mm, "end": v(246.81, 87.5) * mm});
            skLineSegment(sketch, "E2.7.2.23", {"start": v(255.47, 97.5) * mm, "end": v(264.13, 97.5) * mm});
            skLineSegment(sketch, "E2.7.2.24", {"start": v(255.47, 77.5) * mm, "end": v(264.13, 77.5) * mm});
            skLineSegment(sketch, "E2.7.3.0", {"start": v(251.14, 110) * mm, "end": v(255.47, 117.5) * mm});
            skLineSegment(sketch, "E2.7.3.2", {"start": v(233.82, 120) * mm, "end": v(238.15, 127.5) * mm});
            skLineSegment(sketch, "E2.7.3.4", {"start": v(238.15, 112.5) * mm, "end": v(233.82, 120) * mm});
            skLineSegment(sketch, "E2.7.3.5", {"start": v(246.81, 112.5) * mm, "end": v(238.15, 112.5) * mm});
            skLineSegment(sketch, "E2.7.3.6", {"start": v(264.13, 122.5) * mm, "end": v(255.47, 122.5) * mm});
            skLineSegment(sketch, "E2.7.3.7", {"start": v(251.14, 120) * mm, "end": v(246.81, 112.5) * mm});
            skLineSegment(sketch, "E2.7.3.8", {"start": v(255.47, 122.5) * mm, "end": v(251.14, 130) * mm});
            skCircle(sketch, "E2.7.3.9", {"center": v(259.8, 110) * mm, "radius": 7.5 * mm, "construction": true});
            skLineSegment(sketch, "E2.7.3.10", {"start": v(255.47, 102.5) * mm, "end": v(251.14, 110) * mm});
            skLineSegment(sketch, "E2.7.3.11", {"start": v(264.13, 102.5) * mm, "end": v(255.47, 102.5) * mm});
            skLineSegment(sketch, "E2.7.3.12", {"start": v(268.46, 110) * mm, "end": v(264.13, 102.5) * mm});
            skLineSegment(sketch, "E2.7.3.13", {"start": v(233.82, 120) * mm, "end": v(251.14, 120) * mm, "construction": true});
            skLineSegment(sketch, "E2.7.3.14", {"start": v(268.46, 130) * mm, "end": v(264.13, 122.5) * mm});
            skPoint(sketch, "E2.7.3.15", {"position": v(259.8, 117.5) * mm});
            skCircle(sketch, "E2.7.3.17", {"center": v(242.48, 120) * mm, "radius": 7.5 * mm, "construction": true});
            skLineSegment(sketch, "E2.7.3.18", {"start": v(246.81, 127.5) * mm, "end": v(251.14, 120) * mm});
            skLineSegment(sketch, "E2.7.3.20", {"start": v(264.13, 117.5) * mm, "end": v(268.46, 110) * mm});
            skLineSegment(sketch, "E2.7.3.22", {"start": v(238.15, 127.5) * mm, "end": v(246.81, 127.5) * mm});
            skLineSegment(sketch, "E2.7.3.24", {"start": v(255.47, 117.5) * mm, "end": v(264.13, 117.5) * mm});
            skLineSegment(sketch, "E2.8.0.0", {"start": v(285.78, -10) * mm, "end": v(290.11, -2.5) * mm});
            skLineSegment(sketch, "E2.8.0.1", {"start": v(298.77, 17.5) * mm, "end": v(303.1, 10) * mm});
            skLineSegment(sketch, "E2.8.0.2", {"start": v(268.46, 0) * mm, "end": v(272.79, 7.5) * mm});
            skPoint(sketch, "E2.8.0.3", {"position": v(294.44, 17.5) * mm});
            skLineSegment(sketch, "E2.8.0.4", {"start": v(272.79, -7.5) * mm, "end": v(268.46, 0) * mm});
            skLineSegment(sketch, "E2.8.0.5", {"start": v(281.45, -7.5) * mm, "end": v(272.79, -7.5) * mm});
            skLineSegment(sketch, "E2.8.0.6", {"start": v(298.77, 2.5) * mm, "end": v(290.11, 2.5) * mm});
            skLineSegment(sketch, "E2.8.0.7", {"start": v(285.78, 0) * mm, "end": v(281.45, -7.5) * mm});
            skLineSegment(sketch, "E2.8.0.8", {"start": v(290.11, 2.5) * mm, "end": v(285.78, 10) * mm});
            skLineSegment(sketch, "E2.8.0.13", {"start": v(268.46, 0) * mm, "end": v(285.78, 0) * mm, "construction": true});
            skLineSegment(sketch, "E2.8.0.14", {"start": v(303.1, 10) * mm, "end": v(298.77, 2.5) * mm});
            skPoint(sketch, "E2.8.0.15", {"position": v(294.44, -2.5) * mm});
            skCircle(sketch, "E2.8.0.16", {"center": v(294.44, 10) * mm, "radius": 7.5 * mm, "construction": true});
            skCircle(sketch, "E2.8.0.17", {"center": v(277.12, 0) * mm, "radius": 7.5 * mm, "construction": true});
            skLineSegment(sketch, "E2.8.0.18", {"start": v(281.45, 7.5) * mm, "end": v(285.78, 0) * mm});
            skPoint(sketch, "E2.8.0.19", {"position": v(277.12, 7.5) * mm});
            skLineSegment(sketch, "E2.8.0.20", {"start": v(298.77, -2.5) * mm, "end": v(303.1, -10) * mm});
            skLineSegment(sketch, "E2.8.0.21", {"start": v(285.78, 10) * mm, "end": v(290.11, 17.5) * mm});
            skLineSegment(sketch, "E2.8.0.22", {"start": v(272.79, 7.5) * mm, "end": v(281.45, 7.5) * mm});
            skLineSegment(sketch, "E2.8.0.23", {"start": v(290.11, 17.5) * mm, "end": v(298.77, 17.5) * mm});
            skLineSegment(sketch, "E2.8.0.24", {"start": v(290.11, -2.5) * mm, "end": v(298.77, -2.5) * mm});
            skLineSegment(sketch, "E2.8.1.0", {"start": v(285.78, 30) * mm, "end": v(290.11, 37.5) * mm});
            skLineSegment(sketch, "E2.8.1.1", {"start": v(298.77, 57.5) * mm, "end": v(303.1, 50) * mm});
            skLineSegment(sketch, "E2.8.1.2", {"start": v(268.46, 40) * mm, "end": v(272.79, 47.5) * mm});
            skPoint(sketch, "E2.8.1.3", {"position": v(294.44, 57.5) * mm});
            skLineSegment(sketch, "E2.8.1.4", {"start": v(272.79, 32.5) * mm, "end": v(268.46, 40) * mm});
            skLineSegment(sketch, "E2.8.1.5", {"start": v(281.45, 32.5) * mm, "end": v(272.79, 32.5) * mm});
            skLineSegment(sketch, "E2.8.1.6", {"start": v(298.77, 42.5) * mm, "end": v(290.11, 42.5) * mm});
            skLineSegment(sketch, "E2.8.1.7", {"start": v(285.78, 40) * mm, "end": v(281.45, 32.5) * mm});
            skLineSegment(sketch, "E2.8.1.8", {"start": v(290.11, 42.5) * mm, "end": v(285.78, 50) * mm});
            skCircle(sketch, "E2.8.1.9", {"center": v(294.44, 30) * mm, "radius": 7.5 * mm, "construction": true});
            skLineSegment(sketch, "E2.8.1.10", {"start": v(290.11, 22.5) * mm, "end": v(285.78, 30) * mm});
            skLineSegment(sketch, "E2.8.1.11", {"start": v(298.77, 22.5) * mm, "end": v(290.11, 22.5) * mm});
            skLineSegment(sketch, "E2.8.1.12", {"start": v(303.1, 30) * mm, "end": v(298.77, 22.5) * mm});
            skLineSegment(sketch, "E2.8.1.13", {"start": v(268.46, 40) * mm, "end": v(285.78, 40) * mm, "construction": true});
            skLineSegment(sketch, "E2.8.1.14", {"start": v(303.1, 50) * mm, "end": v(298.77, 42.5) * mm});
            skPoint(sketch, "E2.8.1.15", {"position": v(294.44, 37.5) * mm});
            skCircle(sketch, "E2.8.1.16", {"center": v(294.44, 50) * mm, "radius": 7.5 * mm, "construction": true});
            skCircle(sketch, "E2.8.1.17", {"center": v(277.12, 40) * mm, "radius": 7.5 * mm, "construction": true});
            skLineSegment(sketch, "E2.8.1.18", {"start": v(281.45, 47.5) * mm, "end": v(285.78, 40) * mm});
            skPoint(sketch, "E2.8.1.19", {"position": v(277.12, 47.5) * mm});
            skLineSegment(sketch, "E2.8.1.20", {"start": v(298.77, 37.5) * mm, "end": v(303.1, 30) * mm});
            skLineSegment(sketch, "E2.8.1.21", {"start": v(285.78, 50) * mm, "end": v(290.11, 57.5) * mm});
            skLineSegment(sketch, "E2.8.1.22", {"start": v(272.79, 47.5) * mm, "end": v(281.45, 47.5) * mm});
            skLineSegment(sketch, "E2.8.1.23", {"start": v(290.11, 57.5) * mm, "end": v(298.77, 57.5) * mm});
            skLineSegment(sketch, "E2.8.1.24", {"start": v(290.11, 37.5) * mm, "end": v(298.77, 37.5) * mm});
            skLineSegment(sketch, "E2.8.2.0", {"start": v(285.78, 70) * mm, "end": v(290.11, 77.5) * mm});
            skLineSegment(sketch, "E2.8.2.1", {"start": v(298.77, 97.5) * mm, "end": v(303.1, 90) * mm});
            skLineSegment(sketch, "E2.8.2.2", {"start": v(268.46, 80) * mm, "end": v(272.79, 87.5) * mm});
            skPoint(sketch, "E2.8.2.3", {"position": v(294.44, 97.5) * mm});
            skLineSegment(sketch, "E2.8.2.4", {"start": v(272.79, 72.5) * mm, "end": v(268.46, 80) * mm});
            skLineSegment(sketch, "E2.8.2.5", {"start": v(281.45, 72.5) * mm, "end": v(272.79, 72.5) * mm});
            skLineSegment(sketch, "E2.8.2.6", {"start": v(298.77, 82.5) * mm, "end": v(290.11, 82.5) * mm});
            skLineSegment(sketch, "E2.8.2.7", {"start": v(285.78, 80) * mm, "end": v(281.45, 72.5) * mm});
            skLineSegment(sketch, "E2.8.2.8", {"start": v(290.11, 82.5) * mm, "end": v(285.78, 90) * mm});
            skCircle(sketch, "E2.8.2.9", {"center": v(294.44, 70) * mm, "radius": 7.5 * mm, "construction": true});
            skLineSegment(sketch, "E2.8.2.10", {"start": v(290.11, 62.5) * mm, "end": v(285.78, 70) * mm});
            skLineSegment(sketch, "E2.8.2.11", {"start": v(298.77, 62.5) * mm, "end": v(290.11, 62.5) * mm});
            skLineSegment(sketch, "E2.8.2.12", {"start": v(303.1, 70) * mm, "end": v(298.77, 62.5) * mm});
            skLineSegment(sketch, "E2.8.2.13", {"start": v(268.46, 80) * mm, "end": v(285.78, 80) * mm, "construction": true});
            skLineSegment(sketch, "E2.8.2.14", {"start": v(303.1, 90) * mm, "end": v(298.77, 82.5) * mm});
            skPoint(sketch, "E2.8.2.15", {"position": v(294.44, 77.5) * mm});
            skCircle(sketch, "E2.8.2.16", {"center": v(294.44, 90) * mm, "radius": 7.5 * mm, "construction": true});
            skCircle(sketch, "E2.8.2.17", {"center": v(277.12, 80) * mm, "radius": 7.5 * mm, "construction": true});
            skLineSegment(sketch, "E2.8.2.18", {"start": v(281.45, 87.5) * mm, "end": v(285.78, 80) * mm});
            skPoint(sketch, "E2.8.2.19", {"position": v(277.12, 87.5) * mm});
            skLineSegment(sketch, "E2.8.2.20", {"start": v(298.77, 77.5) * mm, "end": v(303.1, 70) * mm});
            skLineSegment(sketch, "E2.8.2.21", {"start": v(285.78, 90) * mm, "end": v(290.11, 97.5) * mm});
            skLineSegment(sketch, "E2.8.2.22", {"start": v(272.79, 87.5) * mm, "end": v(281.45, 87.5) * mm});
            skLineSegment(sketch, "E2.8.2.23", {"start": v(290.11, 97.5) * mm, "end": v(298.77, 97.5) * mm});
            skLineSegment(sketch, "E2.8.2.24", {"start": v(290.11, 77.5) * mm, "end": v(298.77, 77.5) * mm});
            skLineSegment(sketch, "E2.8.3.0", {"start": v(285.78, 110) * mm, "end": v(290.11, 117.5) * mm});
            skLineSegment(sketch, "E2.8.3.2", {"start": v(268.46, 120) * mm, "end": v(272.79, 127.5) * mm});
            skLineSegment(sketch, "E2.8.3.4", {"start": v(272.79, 112.5) * mm, "end": v(268.46, 120) * mm});
            skLineSegment(sketch, "E2.8.3.5", {"start": v(281.45, 112.5) * mm, "end": v(272.79, 112.5) * mm});
            skLineSegment(sketch, "E2.8.3.6", {"start": v(298.77, 122.5) * mm, "end": v(290.11, 122.5) * mm});
            skLineSegment(sketch, "E2.8.3.7", {"start": v(285.78, 120) * mm, "end": v(281.45, 112.5) * mm});
            skLineSegment(sketch, "E2.8.3.8", {"start": v(290.11, 122.5) * mm, "end": v(285.78, 130) * mm});
            skCircle(sketch, "E2.8.3.9", {"center": v(294.44, 110) * mm, "radius": 7.5 * mm, "construction": true});
            skLineSegment(sketch, "E2.8.3.10", {"start": v(290.11, 102.5) * mm, "end": v(285.78, 110) * mm});
            skLineSegment(sketch, "E2.8.3.11", {"start": v(298.77, 102.5) * mm, "end": v(290.11, 102.5) * mm});
            skLineSegment(sketch, "E2.8.3.12", {"start": v(303.1, 110) * mm, "end": v(298.77, 102.5) * mm});
            skLineSegment(sketch, "E2.8.3.13", {"start": v(268.46, 120) * mm, "end": v(285.78, 120) * mm, "construction": true});
            skLineSegment(sketch, "E2.8.3.14", {"start": v(303.1, 130) * mm, "end": v(298.77, 122.5) * mm});
            skPoint(sketch, "E2.8.3.15", {"position": v(294.44, 117.5) * mm});
            skCircle(sketch, "E2.8.3.17", {"center": v(277.12, 120) * mm, "radius": 7.5 * mm, "construction": true});
            skLineSegment(sketch, "E2.8.3.18", {"start": v(281.45, 127.5) * mm, "end": v(285.78, 120) * mm});
            skLineSegment(sketch, "E2.8.3.20", {"start": v(298.77, 117.5) * mm, "end": v(303.1, 110) * mm});
            skLineSegment(sketch, "E2.8.3.22", {"start": v(272.79, 127.5) * mm, "end": v(281.45, 127.5) * mm});
            skLineSegment(sketch, "E2.8.3.24", {"start": v(290.11, 117.5) * mm, "end": v(298.77, 117.5) * mm});
            skLineSegment(sketch, "E2.9.0.0", {"start": v(320.42, -10) * mm, "end": v(324.75, -2.5) * mm});
            skLineSegment(sketch, "E2.9.0.1", {"start": v(333.41, 17.5) * mm, "end": v(337.74, 10) * mm});
            skLineSegment(sketch, "E2.9.0.2", {"start": v(303.1, 0) * mm, "end": v(307.43, 7.5) * mm});
            skPoint(sketch, "E2.9.0.3", {"position": v(329.08, 17.5) * mm});
            skLineSegment(sketch, "E2.9.0.4", {"start": v(307.43, -7.5) * mm, "end": v(303.1, 0) * mm});
            skLineSegment(sketch, "E2.9.0.5", {"start": v(316.1, -7.5) * mm, "end": v(307.43, -7.5) * mm});
            skLineSegment(sketch, "E2.9.0.6", {"start": v(333.41, 2.5) * mm, "end": v(324.75, 2.5) * mm});
            skLineSegment(sketch, "E2.9.0.7", {"start": v(320.42, 0) * mm, "end": v(316.1, -7.5) * mm});
            skLineSegment(sketch, "E2.9.0.8", {"start": v(324.75, 2.5) * mm, "end": v(320.42, 10) * mm});
            skLineSegment(sketch, "E2.9.0.13", {"start": v(303.1, 0) * mm, "end": v(320.42, 0) * mm, "construction": true});
            skLineSegment(sketch, "E2.9.0.14", {"start": v(337.74, 10) * mm, "end": v(333.41, 2.5) * mm});
            skPoint(sketch, "E2.9.0.15", {"position": v(329.08, -2.5) * mm});
            skCircle(sketch, "E2.9.0.16", {"center": v(329.08, 10) * mm, "radius": 7.5 * mm, "construction": true});
            skCircle(sketch, "E2.9.0.17", {"center": v(311.76, 0) * mm, "radius": 7.5 * mm, "construction": true});
            skLineSegment(sketch, "E2.9.0.18", {"start": v(316.1, 7.5) * mm, "end": v(320.42, 0) * mm});
            skPoint(sketch, "E2.9.0.19", {"position": v(311.76, 7.5) * mm});
            skLineSegment(sketch, "E2.9.0.20", {"start": v(333.41, -2.5) * mm, "end": v(337.74, -10) * mm});
            skLineSegment(sketch, "E2.9.0.21", {"start": v(320.42, 10) * mm, "end": v(324.75, 17.5) * mm});
            skLineSegment(sketch, "E2.9.0.22", {"start": v(307.43, 7.5) * mm, "end": v(316.1, 7.5) * mm});
            skLineSegment(sketch, "E2.9.0.23", {"start": v(324.75, 17.5) * mm, "end": v(333.41, 17.5) * mm});
            skLineSegment(sketch, "E2.9.0.24", {"start": v(324.75, -2.5) * mm, "end": v(333.41, -2.5) * mm});
            skLineSegment(sketch, "E2.9.1.0", {"start": v(320.42, 30) * mm, "end": v(324.75, 37.5) * mm});
            skLineSegment(sketch, "E2.9.1.1", {"start": v(333.41, 57.5) * mm, "end": v(337.74, 50) * mm});
            skLineSegment(sketch, "E2.9.1.2", {"start": v(303.1, 40) * mm, "end": v(307.43, 47.5) * mm});
            skPoint(sketch, "E2.9.1.3", {"position": v(329.08, 57.5) * mm});
            skLineSegment(sketch, "E2.9.1.4", {"start": v(307.43, 32.5) * mm, "end": v(303.1, 40) * mm});
            skLineSegment(sketch, "E2.9.1.5", {"start": v(316.1, 32.5) * mm, "end": v(307.43, 32.5) * mm});
            skLineSegment(sketch, "E2.9.1.6", {"start": v(333.41, 42.5) * mm, "end": v(324.75, 42.5) * mm});
            skLineSegment(sketch, "E2.9.1.7", {"start": v(320.42, 40) * mm, "end": v(316.1, 32.5) * mm});
            skLineSegment(sketch, "E2.9.1.8", {"start": v(324.75, 42.5) * mm, "end": v(320.42, 50) * mm});
            skCircle(sketch, "E2.9.1.9", {"center": v(329.08, 30) * mm, "radius": 7.5 * mm, "construction": true});
            skLineSegment(sketch, "E2.9.1.10", {"start": v(324.75, 22.5) * mm, "end": v(320.42, 30) * mm});
            skLineSegment(sketch, "E2.9.1.11", {"start": v(333.41, 22.5) * mm, "end": v(324.75, 22.5) * mm});
            skLineSegment(sketch, "E2.9.1.12", {"start": v(337.74, 30) * mm, "end": v(333.41, 22.5) * mm});
            skLineSegment(sketch, "E2.9.1.13", {"start": v(303.1, 40) * mm, "end": v(320.42, 40) * mm, "construction": true});
            skLineSegment(sketch, "E2.9.1.14", {"start": v(337.74, 50) * mm, "end": v(333.41, 42.5) * mm});
            skPoint(sketch, "E2.9.1.15", {"position": v(329.08, 37.5) * mm});
            skCircle(sketch, "E2.9.1.16", {"center": v(329.08, 50) * mm, "radius": 7.5 * mm, "construction": true});
            skCircle(sketch, "E2.9.1.17", {"center": v(311.76, 40) * mm, "radius": 7.5 * mm, "construction": true});
            skLineSegment(sketch, "E2.9.1.18", {"start": v(316.1, 47.5) * mm, "end": v(320.42, 40) * mm});
            skPoint(sketch, "E2.9.1.19", {"position": v(311.76, 47.5) * mm});
            skLineSegment(sketch, "E2.9.1.20", {"start": v(333.41, 37.5) * mm, "end": v(337.74, 30) * mm});
            skLineSegment(sketch, "E2.9.1.21", {"start": v(320.42, 50) * mm, "end": v(324.75, 57.5) * mm});
            skLineSegment(sketch, "E2.9.1.22", {"start": v(307.43, 47.5) * mm, "end": v(316.1, 47.5) * mm});
            skLineSegment(sketch, "E2.9.1.23", {"start": v(324.75, 57.5) * mm, "end": v(333.41, 57.5) * mm});
            skLineSegment(sketch, "E2.9.1.24", {"start": v(324.75, 37.5) * mm, "end": v(333.41, 37.5) * mm});
            skLineSegment(sketch, "E2.9.2.0", {"start": v(320.42, 70) * mm, "end": v(324.75, 77.5) * mm});
            skLineSegment(sketch, "E2.9.2.1", {"start": v(333.41, 97.5) * mm, "end": v(337.74, 90) * mm});
            skLineSegment(sketch, "E2.9.2.2", {"start": v(303.1, 80) * mm, "end": v(307.43, 87.5) * mm});
            skPoint(sketch, "E2.9.2.3", {"position": v(329.08, 97.5) * mm});
            skLineSegment(sketch, "E2.9.2.4", {"start": v(307.43, 72.5) * mm, "end": v(303.1, 80) * mm});
            skLineSegment(sketch, "E2.9.2.5", {"start": v(316.1, 72.5) * mm, "end": v(307.43, 72.5) * mm});
            skLineSegment(sketch, "E2.9.2.6", {"start": v(333.41, 82.5) * mm, "end": v(324.75, 82.5) * mm});
            skLineSegment(sketch, "E2.9.2.7", {"start": v(320.42, 80) * mm, "end": v(316.1, 72.5) * mm});
            skLineSegment(sketch, "E2.9.2.8", {"start": v(324.75, 82.5) * mm, "end": v(320.42, 90) * mm});
            skCircle(sketch, "E2.9.2.9", {"center": v(329.08, 70) * mm, "radius": 7.5 * mm, "construction": true});
            skLineSegment(sketch, "E2.9.2.10", {"start": v(324.75, 62.5) * mm, "end": v(320.42, 70) * mm});
            skLineSegment(sketch, "E2.9.2.11", {"start": v(333.41, 62.5) * mm, "end": v(324.75, 62.5) * mm});
            skLineSegment(sketch, "E2.9.2.12", {"start": v(337.74, 70) * mm, "end": v(333.41, 62.5) * mm});
            skLineSegment(sketch, "E2.9.2.13", {"start": v(303.1, 80) * mm, "end": v(320.42, 80) * mm, "construction": true});
            skLineSegment(sketch, "E2.9.2.14", {"start": v(337.74, 90) * mm, "end": v(333.41, 82.5) * mm});
            skPoint(sketch, "E2.9.2.15", {"position": v(329.08, 77.5) * mm});
            skCircle(sketch, "E2.9.2.16", {"center": v(329.08, 90) * mm, "radius": 7.5 * mm, "construction": true});
            skCircle(sketch, "E2.9.2.17", {"center": v(311.76, 80) * mm, "radius": 7.5 * mm, "construction": true});
            skLineSegment(sketch, "E2.9.2.18", {"start": v(316.1, 87.5) * mm, "end": v(320.42, 80) * mm});
            skPoint(sketch, "E2.9.2.19", {"position": v(311.76, 87.5) * mm});
            skLineSegment(sketch, "E2.9.2.20", {"start": v(333.41, 77.5) * mm, "end": v(337.74, 70) * mm});
            skLineSegment(sketch, "E2.9.2.21", {"start": v(320.42, 90) * mm, "end": v(324.75, 97.5) * mm});
            skLineSegment(sketch, "E2.9.2.22", {"start": v(307.43, 87.5) * mm, "end": v(316.1, 87.5) * mm});
            skLineSegment(sketch, "E2.9.2.23", {"start": v(324.75, 97.5) * mm, "end": v(333.41, 97.5) * mm});
            skLineSegment(sketch, "E2.9.2.24", {"start": v(324.75, 77.5) * mm, "end": v(333.41, 77.5) * mm});
            skLineSegment(sketch, "E2.9.3.0", {"start": v(320.42, 110) * mm, "end": v(324.75, 117.5) * mm});
            skLineSegment(sketch, "E2.9.3.2", {"start": v(303.1, 120) * mm, "end": v(307.43, 127.5) * mm});
            skLineSegment(sketch, "E2.9.3.4", {"start": v(307.43, 112.5) * mm, "end": v(303.1, 120) * mm});
            skLineSegment(sketch, "E2.9.3.5", {"start": v(316.1, 112.5) * mm, "end": v(307.43, 112.5) * mm});
            skLineSegment(sketch, "E2.9.3.6", {"start": v(333.41, 122.5) * mm, "end": v(324.75, 122.5) * mm});
            skLineSegment(sketch, "E2.9.3.7", {"start": v(320.42, 120) * mm, "end": v(316.1, 112.5) * mm});
            skLineSegment(sketch, "E2.9.3.8", {"start": v(324.75, 122.5) * mm, "end": v(320.42, 130) * mm});
            skCircle(sketch, "E2.9.3.9", {"center": v(329.08, 110) * mm, "radius": 7.5 * mm, "construction": true});
            skLineSegment(sketch, "E2.9.3.10", {"start": v(324.75, 102.5) * mm, "end": v(320.42, 110) * mm});
            skLineSegment(sketch, "E2.9.3.11", {"start": v(333.41, 102.5) * mm, "end": v(324.75, 102.5) * mm});
            skLineSegment(sketch, "E2.9.3.12", {"start": v(337.74, 110) * mm, "end": v(333.41, 102.5) * mm});
            skLineSegment(sketch, "E2.9.3.13", {"start": v(303.1, 120) * mm, "end": v(320.42, 120) * mm, "construction": true});
            skLineSegment(sketch, "E2.9.3.14", {"start": v(337.74, 130) * mm, "end": v(333.41, 122.5) * mm});
            skPoint(sketch, "E2.9.3.15", {"position": v(329.08, 117.5) * mm});
            skCircle(sketch, "E2.9.3.17", {"center": v(311.76, 120) * mm, "radius": 7.5 * mm, "construction": true});
            skLineSegment(sketch, "E2.9.3.18", {"start": v(316.1, 127.5) * mm, "end": v(320.42, 120) * mm});
            skLineSegment(sketch, "E2.9.3.20", {"start": v(333.41, 117.5) * mm, "end": v(337.74, 110) * mm});
            skLineSegment(sketch, "E2.9.3.22", {"start": v(307.43, 127.5) * mm, "end": v(316.1, 127.5) * mm});
            skLineSegment(sketch, "E2.9.3.24", {"start": v(324.75, 117.5) * mm, "end": v(333.41, 117.5) * mm});
            skLineSegment(sketch, "E2.10.0.0", {"start": v(355.06, -10) * mm, "end": v(359.4, -2.5) * mm});
            skLineSegment(sketch, "E2.10.0.1", {"start": v(368.05, 17.5) * mm, "end": v(372.38, 10) * mm});
            skLineSegment(sketch, "E2.10.0.2", {"start": v(337.74, 0) * mm, "end": v(342.07, 7.5) * mm});
            skPoint(sketch, "E2.10.0.3", {"position": v(363.72, 17.5) * mm});
            skLineSegment(sketch, "E2.10.0.4", {"start": v(342.07, -7.5) * mm, "end": v(337.74, 0) * mm});
            skLineSegment(sketch, "E2.10.0.5", {"start": v(350.73, -7.5) * mm, "end": v(342.07, -7.5) * mm});
            skLineSegment(sketch, "E2.10.0.6", {"start": v(368.05, 2.5) * mm, "end": v(359.4, 2.5) * mm});
            skLineSegment(sketch, "E2.10.0.7", {"start": v(355.06, 0) * mm, "end": v(350.73, -7.5) * mm});
            skLineSegment(sketch, "E2.10.0.8", {"start": v(359.4, 2.5) * mm, "end": v(355.06, 10) * mm});
            skLineSegment(sketch, "E2.10.0.13", {"start": v(337.74, 0) * mm, "end": v(355.06, 0) * mm, "construction": true});
            skLineSegment(sketch, "E2.10.0.14", {"start": v(372.38, 10) * mm, "end": v(368.05, 2.5) * mm});
            skPoint(sketch, "E2.10.0.15", {"position": v(363.72, -2.5) * mm});
            skCircle(sketch, "E2.10.0.16", {"center": v(363.72, 10) * mm, "radius": 7.5 * mm, "construction": true});
            skCircle(sketch, "E2.10.0.17", {"center": v(346.4, 0) * mm, "radius": 7.5 * mm, "construction": true});
            skLineSegment(sketch, "E2.10.0.18", {"start": v(350.73, 7.5) * mm, "end": v(355.06, 0) * mm});
            skPoint(sketch, "E2.10.0.19", {"position": v(346.4, 7.5) * mm});
            skLineSegment(sketch, "E2.10.0.20", {"start": v(368.05, -2.5) * mm, "end": v(372.38, -10) * mm});
            skLineSegment(sketch, "E2.10.0.21", {"start": v(355.06, 10) * mm, "end": v(359.4, 17.5) * mm});
            skLineSegment(sketch, "E2.10.0.22", {"start": v(342.07, 7.5) * mm, "end": v(350.73, 7.5) * mm});
            skLineSegment(sketch, "E2.10.0.23", {"start": v(359.4, 17.5) * mm, "end": v(368.05, 17.5) * mm});
            skLineSegment(sketch, "E2.10.0.24", {"start": v(359.4, -2.5) * mm, "end": v(368.05, -2.5) * mm});
            skLineSegment(sketch, "E2.10.1.0", {"start": v(355.06, 30) * mm, "end": v(359.4, 37.5) * mm});
            skLineSegment(sketch, "E2.10.1.1", {"start": v(368.05, 57.5) * mm, "end": v(372.38, 50) * mm});
            skLineSegment(sketch, "E2.10.1.2", {"start": v(337.74, 40) * mm, "end": v(342.07, 47.5) * mm});
            skPoint(sketch, "E2.10.1.3", {"position": v(363.72, 57.5) * mm});
            skLineSegment(sketch, "E2.10.1.4", {"start": v(342.07, 32.5) * mm, "end": v(337.74, 40) * mm});
            skLineSegment(sketch, "E2.10.1.5", {"start": v(350.73, 32.5) * mm, "end": v(342.07, 32.5) * mm});
            skLineSegment(sketch, "E2.10.1.6", {"start": v(368.05, 42.5) * mm, "end": v(359.4, 42.5) * mm});
            skLineSegment(sketch, "E2.10.1.7", {"start": v(355.06, 40) * mm, "end": v(350.73, 32.5) * mm});
            skLineSegment(sketch, "E2.10.1.8", {"start": v(359.4, 42.5) * mm, "end": v(355.06, 50) * mm});
            skCircle(sketch, "E2.10.1.9", {"center": v(363.72, 30) * mm, "radius": 7.5 * mm, "construction": true});
            skLineSegment(sketch, "E2.10.1.10", {"start": v(359.4, 22.5) * mm, "end": v(355.06, 30) * mm});
            skLineSegment(sketch, "E2.10.1.11", {"start": v(368.05, 22.5) * mm, "end": v(359.4, 22.5) * mm});
            skLineSegment(sketch, "E2.10.1.12", {"start": v(372.38, 30) * mm, "end": v(368.05, 22.5) * mm});
            skLineSegment(sketch, "E2.10.1.13", {"start": v(337.74, 40) * mm, "end": v(355.06, 40) * mm, "construction": true});
            skLineSegment(sketch, "E2.10.1.14", {"start": v(372.38, 50) * mm, "end": v(368.05, 42.5) * mm});
            skPoint(sketch, "E2.10.1.15", {"position": v(363.72, 37.5) * mm});
            skCircle(sketch, "E2.10.1.16", {"center": v(363.72, 50) * mm, "radius": 7.5 * mm, "construction": true});
            skCircle(sketch, "E2.10.1.17", {"center": v(346.4, 40) * mm, "radius": 7.5 * mm, "construction": true});
            skLineSegment(sketch, "E2.10.1.18", {"start": v(350.73, 47.5) * mm, "end": v(355.06, 40) * mm});
            skPoint(sketch, "E2.10.1.19", {"position": v(346.4, 47.5) * mm});
            skLineSegment(sketch, "E2.10.1.20", {"start": v(368.05, 37.5) * mm, "end": v(372.38, 30) * mm});
            skLineSegment(sketch, "E2.10.1.21", {"start": v(355.06, 50) * mm, "end": v(359.4, 57.5) * mm});
            skLineSegment(sketch, "E2.10.1.22", {"start": v(342.07, 47.5) * mm, "end": v(350.73, 47.5) * mm});
            skLineSegment(sketch, "E2.10.1.23", {"start": v(359.4, 57.5) * mm, "end": v(368.05, 57.5) * mm});
            skLineSegment(sketch, "E2.10.1.24", {"start": v(359.4, 37.5) * mm, "end": v(368.05, 37.5) * mm});
            skLineSegment(sketch, "E2.10.2.0", {"start": v(355.06, 70) * mm, "end": v(359.4, 77.5) * mm});
            skLineSegment(sketch, "E2.10.2.1", {"start": v(368.05, 97.5) * mm, "end": v(372.38, 90) * mm});
            skLineSegment(sketch, "E2.10.2.2", {"start": v(337.74, 80) * mm, "end": v(342.07, 87.5) * mm});
            skPoint(sketch, "E2.10.2.3", {"position": v(363.72, 97.5) * mm});
            skLineSegment(sketch, "E2.10.2.4", {"start": v(342.07, 72.5) * mm, "end": v(337.74, 80) * mm});
            skLineSegment(sketch, "E2.10.2.5", {"start": v(350.73, 72.5) * mm, "end": v(342.07, 72.5) * mm});
            skLineSegment(sketch, "E2.10.2.6", {"start": v(368.05, 82.5) * mm, "end": v(359.4, 82.5) * mm});
            skLineSegment(sketch, "E2.10.2.7", {"start": v(355.06, 80) * mm, "end": v(350.73, 72.5) * mm});
            skLineSegment(sketch, "E2.10.2.8", {"start": v(359.4, 82.5) * mm, "end": v(355.06, 90) * mm});
            skCircle(sketch, "E2.10.2.9", {"center": v(363.72, 70) * mm, "radius": 7.5 * mm, "construction": true});
            skLineSegment(sketch, "E2.10.2.10", {"start": v(359.4, 62.5) * mm, "end": v(355.06, 70) * mm});
            skLineSegment(sketch, "E2.10.2.11", {"start": v(368.05, 62.5) * mm, "end": v(359.4, 62.5) * mm});
            skLineSegment(sketch, "E2.10.2.12", {"start": v(372.38, 70) * mm, "end": v(368.05, 62.5) * mm});
            skLineSegment(sketch, "E2.10.2.13", {"start": v(337.74, 80) * mm, "end": v(355.06, 80) * mm, "construction": true});
            skLineSegment(sketch, "E2.10.2.14", {"start": v(372.38, 90) * mm, "end": v(368.05, 82.5) * mm});
            skPoint(sketch, "E2.10.2.15", {"position": v(363.72, 77.5) * mm});
            skCircle(sketch, "E2.10.2.16", {"center": v(363.72, 90) * mm, "radius": 7.5 * mm, "construction": true});
            skCircle(sketch, "E2.10.2.17", {"center": v(346.4, 80) * mm, "radius": 7.5 * mm, "construction": true});
            skLineSegment(sketch, "E2.10.2.18", {"start": v(350.73, 87.5) * mm, "end": v(355.06, 80) * mm});
            skPoint(sketch, "E2.10.2.19", {"position": v(346.4, 87.5) * mm});
            skLineSegment(sketch, "E2.10.2.20", {"start": v(368.05, 77.5) * mm, "end": v(372.38, 70) * mm});
            skLineSegment(sketch, "E2.10.2.21", {"start": v(355.06, 90) * mm, "end": v(359.4, 97.5) * mm});
            skLineSegment(sketch, "E2.10.2.22", {"start": v(342.07, 87.5) * mm, "end": v(350.73, 87.5) * mm});
            skLineSegment(sketch, "E2.10.2.23", {"start": v(359.4, 97.5) * mm, "end": v(368.05, 97.5) * mm});
            skLineSegment(sketch, "E2.10.2.24", {"start": v(359.4, 77.5) * mm, "end": v(368.05, 77.5) * mm});
            skLineSegment(sketch, "E2.10.3.0", {"start": v(355.06, 110) * mm, "end": v(359.4, 117.5) * mm});
            skLineSegment(sketch, "E2.10.3.2", {"start": v(337.74, 120) * mm, "end": v(342.07, 127.5) * mm});
            skLineSegment(sketch, "E2.10.3.4", {"start": v(342.07, 112.5) * mm, "end": v(337.74, 120) * mm});
            skLineSegment(sketch, "E2.10.3.5", {"start": v(350.73, 112.5) * mm, "end": v(342.07, 112.5) * mm});
            skLineSegment(sketch, "E2.10.3.6", {"start": v(368.05, 122.5) * mm, "end": v(359.4, 122.5) * mm});
            skLineSegment(sketch, "E2.10.3.7", {"start": v(355.06, 120) * mm, "end": v(350.73, 112.5) * mm});
            skLineSegment(sketch, "E2.10.3.8", {"start": v(359.4, 122.5) * mm, "end": v(355.06, 130) * mm});
            skCircle(sketch, "E2.10.3.9", {"center": v(363.72, 110) * mm, "radius": 7.5 * mm, "construction": true});
            skLineSegment(sketch, "E2.10.3.10", {"start": v(359.4, 102.5) * mm, "end": v(355.06, 110) * mm});
            skLineSegment(sketch, "E2.10.3.11", {"start": v(368.05, 102.5) * mm, "end": v(359.4, 102.5) * mm});
            skLineSegment(sketch, "E2.10.3.12", {"start": v(372.38, 110) * mm, "end": v(368.05, 102.5) * mm});
            skLineSegment(sketch, "E2.10.3.13", {"start": v(337.74, 120) * mm, "end": v(355.06, 120) * mm, "construction": true});
            skLineSegment(sketch, "E2.10.3.14", {"start": v(372.38, 130) * mm, "end": v(368.05, 122.5) * mm});
            skPoint(sketch, "E2.10.3.15", {"position": v(363.72, 117.5) * mm});
            skCircle(sketch, "E2.10.3.17", {"center": v(346.4, 120) * mm, "radius": 7.5 * mm, "construction": true});
            skLineSegment(sketch, "E2.10.3.18", {"start": v(350.73, 127.5) * mm, "end": v(355.06, 120) * mm});
            skLineSegment(sketch, "E2.10.3.20", {"start": v(368.05, 117.5) * mm, "end": v(372.38, 110) * mm});
            skLineSegment(sketch, "E2.10.3.22", {"start": v(342.07, 127.5) * mm, "end": v(350.73, 127.5) * mm});
            skLineSegment(sketch, "E2.10.3.24", {"start": v(359.4, 117.5) * mm, "end": v(368.05, 117.5) * mm});
            skLineSegment(sketch, "E2.11.0.0", {"start": v(389.7, -10) * mm, "end": v(394.03, -2.5) * mm});
            skLineSegment(sketch, "E2.11.0.1", {"start": v(402.7, 17.5) * mm, "end": v(407.02, 10) * mm});
            skLineSegment(sketch, "E2.11.0.2", {"start": v(372.38, 0) * mm, "end": v(376.7, 7.5) * mm});
            skPoint(sketch, "E2.11.0.3", {"position": v(398.36, 17.5) * mm});
            skLineSegment(sketch, "E2.11.0.4", {"start": v(376.7, -7.5) * mm, "end": v(372.38, 0) * mm});
            skLineSegment(sketch, "E2.11.0.5", {"start": v(385.37, -7.5) * mm, "end": v(376.7, -7.5) * mm});
            skLineSegment(sketch, "E2.11.0.6", {"start": v(402.7, 2.5) * mm, "end": v(394.03, 2.5) * mm});
            skLineSegment(sketch, "E2.11.0.7", {"start": v(389.7, 0) * mm, "end": v(385.37, -7.5) * mm});
            skLineSegment(sketch, "E2.11.0.8", {"start": v(394.03, 2.5) * mm, "end": v(389.7, 10) * mm});
            skLineSegment(sketch, "E2.11.0.13", {"start": v(372.38, 0) * mm, "end": v(389.7, 0) * mm, "construction": true});
            skLineSegment(sketch, "E2.11.0.14", {"start": v(407.02, 10) * mm, "end": v(402.7, 2.5) * mm});
            skPoint(sketch, "E2.11.0.15", {"position": v(398.36, -2.5) * mm});
            skCircle(sketch, "E2.11.0.16", {"center": v(398.36, 10) * mm, "radius": 7.5 * mm, "construction": true});
            skCircle(sketch, "E2.11.0.17", {"center": v(381.04, 0) * mm, "radius": 7.5 * mm, "construction": true});
            skLineSegment(sketch, "E2.11.0.18", {"start": v(385.37, 7.5) * mm, "end": v(389.7, 0) * mm});
            skPoint(sketch, "E2.11.0.19", {"position": v(381.04, 7.5) * mm});
            skLineSegment(sketch, "E2.11.0.20", {"start": v(402.7, -2.5) * mm, "end": v(407.02, -10) * mm});
            skLineSegment(sketch, "E2.11.0.21", {"start": v(389.7, 10) * mm, "end": v(394.03, 17.5) * mm});
            skLineSegment(sketch, "E2.11.0.22", {"start": v(376.7, 7.5) * mm, "end": v(385.37, 7.5) * mm});
            skLineSegment(sketch, "E2.11.0.23", {"start": v(394.03, 17.5) * mm, "end": v(402.7, 17.5) * mm});
            skLineSegment(sketch, "E2.11.0.24", {"start": v(394.03, -2.5) * mm, "end": v(402.7, -2.5) * mm});
            skLineSegment(sketch, "E2.11.1.0", {"start": v(389.7, 30) * mm, "end": v(394.03, 37.5) * mm});
            skLineSegment(sketch, "E2.11.1.1", {"start": v(402.7, 57.5) * mm, "end": v(407.02, 50) * mm});
            skLineSegment(sketch, "E2.11.1.2", {"start": v(372.38, 40) * mm, "end": v(376.7, 47.5) * mm});
            skPoint(sketch, "E2.11.1.3", {"position": v(398.36, 57.5) * mm});
            skLineSegment(sketch, "E2.11.1.4", {"start": v(376.7, 32.5) * mm, "end": v(372.38, 40) * mm});
            skLineSegment(sketch, "E2.11.1.5", {"start": v(385.37, 32.5) * mm, "end": v(376.7, 32.5) * mm});
            skLineSegment(sketch, "E2.11.1.6", {"start": v(402.7, 42.5) * mm, "end": v(394.03, 42.5) * mm});
            skLineSegment(sketch, "E2.11.1.7", {"start": v(389.7, 40) * mm, "end": v(385.37, 32.5) * mm});
            skLineSegment(sketch, "E2.11.1.8", {"start": v(394.03, 42.5) * mm, "end": v(389.7, 50) * mm});
            skCircle(sketch, "E2.11.1.9", {"center": v(398.36, 30) * mm, "radius": 7.5 * mm, "construction": true});
            skLineSegment(sketch, "E2.11.1.10", {"start": v(394.03, 22.5) * mm, "end": v(389.7, 30) * mm});
            skLineSegment(sketch, "E2.11.1.11", {"start": v(402.7, 22.5) * mm, "end": v(394.03, 22.5) * mm});
            skLineSegment(sketch, "E2.11.1.12", {"start": v(407.02, 30) * mm, "end": v(402.7, 22.5) * mm});
            skLineSegment(sketch, "E2.11.1.13", {"start": v(372.38, 40) * mm, "end": v(389.7, 40) * mm, "construction": true});
            skLineSegment(sketch, "E2.11.1.14", {"start": v(407.02, 50) * mm, "end": v(402.7, 42.5) * mm});
            skPoint(sketch, "E2.11.1.15", {"position": v(398.36, 37.5) * mm});
            skCircle(sketch, "E2.11.1.16", {"center": v(398.36, 50) * mm, "radius": 7.5 * mm, "construction": true});
            skCircle(sketch, "E2.11.1.17", {"center": v(381.04, 40) * mm, "radius": 7.5 * mm, "construction": true});
            skLineSegment(sketch, "E2.11.1.18", {"start": v(385.37, 47.5) * mm, "end": v(389.7, 40) * mm});
            skPoint(sketch, "E2.11.1.19", {"position": v(381.04, 47.5) * mm});
            skLineSegment(sketch, "E2.11.1.20", {"start": v(402.7, 37.5) * mm, "end": v(407.02, 30) * mm});
            skLineSegment(sketch, "E2.11.1.21", {"start": v(389.7, 50) * mm, "end": v(394.03, 57.5) * mm});
            skLineSegment(sketch, "E2.11.1.22", {"start": v(376.7, 47.5) * mm, "end": v(385.37, 47.5) * mm});
            skLineSegment(sketch, "E2.11.1.23", {"start": v(394.03, 57.5) * mm, "end": v(402.7, 57.5) * mm});
            skLineSegment(sketch, "E2.11.1.24", {"start": v(394.03, 37.5) * mm, "end": v(402.7, 37.5) * mm});
            skLineSegment(sketch, "E2.11.2.0", {"start": v(389.7, 70) * mm, "end": v(394.03, 77.5) * mm});
            skLineSegment(sketch, "E2.11.2.1", {"start": v(402.7, 97.5) * mm, "end": v(407.02, 90) * mm});
            skLineSegment(sketch, "E2.11.2.2", {"start": v(372.38, 80) * mm, "end": v(376.7, 87.5) * mm});
            skPoint(sketch, "E2.11.2.3", {"position": v(398.36, 97.5) * mm});
            skLineSegment(sketch, "E2.11.2.4", {"start": v(376.7, 72.5) * mm, "end": v(372.38, 80) * mm});
            skLineSegment(sketch, "E2.11.2.5", {"start": v(385.37, 72.5) * mm, "end": v(376.7, 72.5) * mm});
            skLineSegment(sketch, "E2.11.2.6", {"start": v(402.7, 82.5) * mm, "end": v(394.03, 82.5) * mm});
            skLineSegment(sketch, "E2.11.2.7", {"start": v(389.7, 80) * mm, "end": v(385.37, 72.5) * mm});
            skLineSegment(sketch, "E2.11.2.8", {"start": v(394.03, 82.5) * mm, "end": v(389.7, 90) * mm});
            skCircle(sketch, "E2.11.2.9", {"center": v(398.36, 70) * mm, "radius": 7.5 * mm, "construction": true});
            skLineSegment(sketch, "E2.11.2.10", {"start": v(394.03, 62.5) * mm, "end": v(389.7, 70) * mm});
            skLineSegment(sketch, "E2.11.2.11", {"start": v(402.7, 62.5) * mm, "end": v(394.03, 62.5) * mm});
            skLineSegment(sketch, "E2.11.2.12", {"start": v(407.02, 70) * mm, "end": v(402.7, 62.5) * mm});
            skLineSegment(sketch, "E2.11.2.13", {"start": v(372.38, 80) * mm, "end": v(389.7, 80) * mm, "construction": true});
            skLineSegment(sketch, "E2.11.2.14", {"start": v(407.02, 90) * mm, "end": v(402.7, 82.5) * mm});
            skPoint(sketch, "E2.11.2.15", {"position": v(398.36, 77.5) * mm});
            skCircle(sketch, "E2.11.2.16", {"center": v(398.36, 90) * mm, "radius": 7.5 * mm, "construction": true});
            skCircle(sketch, "E2.11.2.17", {"center": v(381.04, 80) * mm, "radius": 7.5 * mm, "construction": true});
            skLineSegment(sketch, "E2.11.2.18", {"start": v(385.37, 87.5) * mm, "end": v(389.7, 80) * mm});
            skPoint(sketch, "E2.11.2.19", {"position": v(381.04, 87.5) * mm});
            skLineSegment(sketch, "E2.11.2.20", {"start": v(402.7, 77.5) * mm, "end": v(407.02, 70) * mm});
            skLineSegment(sketch, "E2.11.2.21", {"start": v(389.7, 90) * mm, "end": v(394.03, 97.5) * mm});
            skLineSegment(sketch, "E2.11.2.22", {"start": v(376.7, 87.5) * mm, "end": v(385.37, 87.5) * mm});
            skLineSegment(sketch, "E2.11.2.23", {"start": v(394.03, 97.5) * mm, "end": v(402.7, 97.5) * mm});
            skLineSegment(sketch, "E2.11.2.24", {"start": v(394.03, 77.5) * mm, "end": v(402.7, 77.5) * mm});
            skLineSegment(sketch, "E2.11.3.0", {"start": v(389.7, 110) * mm, "end": v(394.03, 117.5) * mm});
            skLineSegment(sketch, "E2.11.3.2", {"start": v(372.38, 120) * mm, "end": v(376.7, 127.5) * mm});
            skLineSegment(sketch, "E2.11.3.4", {"start": v(376.7, 112.5) * mm, "end": v(372.38, 120) * mm});
            skLineSegment(sketch, "E2.11.3.5", {"start": v(385.37, 112.5) * mm, "end": v(376.7, 112.5) * mm});
            skLineSegment(sketch, "E2.11.3.6", {"start": v(402.7, 122.5) * mm, "end": v(394.03, 122.5) * mm});
            skLineSegment(sketch, "E2.11.3.7", {"start": v(389.7, 120) * mm, "end": v(385.37, 112.5) * mm});
            skLineSegment(sketch, "E2.11.3.8", {"start": v(394.03, 122.5) * mm, "end": v(389.7, 130) * mm});
            skCircle(sketch, "E2.11.3.9", {"center": v(398.36, 110) * mm, "radius": 7.5 * mm, "construction": true});
            skLineSegment(sketch, "E2.11.3.10", {"start": v(394.03, 102.5) * mm, "end": v(389.7, 110) * mm});
            skLineSegment(sketch, "E2.11.3.11", {"start": v(402.7, 102.5) * mm, "end": v(394.03, 102.5) * mm});
            skLineSegment(sketch, "E2.11.3.12", {"start": v(407.02, 110) * mm, "end": v(402.7, 102.5) * mm});
            skLineSegment(sketch, "E2.11.3.13", {"start": v(372.38, 120) * mm, "end": v(389.7, 120) * mm, "construction": true});
            skLineSegment(sketch, "E2.11.3.14", {"start": v(407.02, 130) * mm, "end": v(402.7, 122.5) * mm});
            skPoint(sketch, "E2.11.3.15", {"position": v(398.36, 117.5) * mm});
            skCircle(sketch, "E2.11.3.17", {"center": v(381.04, 120) * mm, "radius": 7.5 * mm, "construction": true});
            skLineSegment(sketch, "E2.11.3.18", {"start": v(385.37, 127.5) * mm, "end": v(389.7, 120) * mm});
            skLineSegment(sketch, "E2.11.3.20", {"start": v(402.7, 117.5) * mm, "end": v(407.02, 110) * mm});
            skLineSegment(sketch, "E2.11.3.22", {"start": v(376.7, 127.5) * mm, "end": v(385.37, 127.5) * mm});
            skLineSegment(sketch, "E2.11.3.24", {"start": v(394.03, 117.5) * mm, "end": v(402.7, 117.5) * mm});
            skLineSegment(sketch, "E2.direction1", {"start": v(-4.33, -7.5) * mm, "end": v(30.3, -7.5) * mm, "construction": true});
            skLineSegment(sketch, "E3", {"start": v(17.32, 30) * mm, "end": v(51.96, 10) * mm, "construction": true});
            skLineSegment(sketch, "E4", {"start": v(51.96, 30) * mm, "end": v(17.32, 10) * mm, "construction": true});
            skLineSegment(sketch, "E5", {"start": v(34.64, 20) * mm, "end": v(34.64, 14.86) * mm, "construction": true});
            skCircle(sketch, "E6.cCircle", {"center": v(34.64, 20) * mm, "radius": 7.5 * mm, "construction": true});
            skLineSegment(sketch, "E6.0", {"start": v(30.31, 27.5) * mm, "end": v(38.97, 27.5) * mm});
            skLineSegment(sketch, "E6.1", {"start": v(38.97, 27.5) * mm, "end": v(43.3, 20) * mm});
            skLineSegment(sketch, "E6.2", {"start": v(43.3, 20) * mm, "end": v(38.97, 12.5) * mm});
            skLineSegment(sketch, "E6.3", {"start": v(38.97, 12.5) * mm, "end": v(30.31, 12.5) * mm});
            skLineSegment(sketch, "E6.4", {"start": v(30.31, 12.5) * mm, "end": v(25.98, 20) * mm});
            skLineSegment(sketch, "E6.5", {"start": v(25.98, 20) * mm, "end": v(30.31, 27.5) * mm});
            skPoint(sketch, "E6.0.midPoint", {"position": v(34.64, 27.5) * mm});
            skLineSegment(sketch, "E7", {"start": v(60.62, 30) * mm, "end": v(77.94, 10) * mm, "construction": true});
            skLineSegment(sketch, "E8", {"start": v(77.94, 30) * mm, "end": v(60.62, 10) * mm, "construction": true});
            skLineSegment(sketch, "E9", {"start": v(69.28, 20) * mm, "end": v(34.64, 20) * mm, "construction": true});
            skLineSegment(sketch, "E10.0.1.0", {"start": v(43.3, 60) * mm, "end": v(38.97, 52.5) * mm});
            skLineSegment(sketch, "E10.0.1.1", {"start": v(38.97, 52.5) * mm, "end": v(30.31, 52.5) * mm});
            skLineSegment(sketch, "E10.0.1.2", {"start": v(30.31, 52.5) * mm, "end": v(25.98, 60) * mm});
            skLineSegment(sketch, "E10.0.1.3", {"start": v(25.98, 60) * mm, "end": v(30.31, 67.5) * mm});
            skLineSegment(sketch, "E10.0.1.4", {"start": v(30.31, 67.5) * mm, "end": v(38.97, 67.5) * mm});
            skLineSegment(sketch, "E10.0.1.5", {"start": v(38.97, 67.5) * mm, "end": v(43.3, 60) * mm});
            skLineSegment(sketch, "E10.0.2.0", {"start": v(43.3, 100) * mm, "end": v(38.97, 92.5) * mm});
            skLineSegment(sketch, "E10.0.2.1", {"start": v(38.97, 92.5) * mm, "end": v(30.31, 92.5) * mm});
            skLineSegment(sketch, "E10.0.2.2", {"start": v(30.31, 92.5) * mm, "end": v(25.98, 100) * mm});
            skLineSegment(sketch, "E10.0.2.3", {"start": v(25.98, 100) * mm, "end": v(30.31, 107.5) * mm});
            skLineSegment(sketch, "E10.0.2.4", {"start": v(30.31, 107.5) * mm, "end": v(38.97, 107.5) * mm});
            skLineSegment(sketch, "E10.0.2.5", {"start": v(38.97, 107.5) * mm, "end": v(43.3, 100) * mm});
            skLineSegment(sketch, "E10.1.0.0", {"start": v(77.94, 20) * mm, "end": v(73.61, 12.5) * mm});
            skLineSegment(sketch, "E10.1.0.1", {"start": v(73.61, 12.5) * mm, "end": v(64.95, 12.5) * mm});
            skLineSegment(sketch, "E10.1.0.2", {"start": v(64.95, 12.5) * mm, "end": v(60.62, 20) * mm});
            skLineSegment(sketch, "E10.1.0.3", {"start": v(60.62, 20) * mm, "end": v(64.95, 27.5) * mm});
            skLineSegment(sketch, "E10.1.0.4", {"start": v(64.95, 27.5) * mm, "end": v(73.61, 27.5) * mm});
            skLineSegment(sketch, "E10.1.0.5", {"start": v(73.61, 27.5) * mm, "end": v(77.94, 20) * mm});
            skLineSegment(sketch, "E10.1.1.0", {"start": v(77.94, 60) * mm, "end": v(73.61, 52.5) * mm});
            skLineSegment(sketch, "E10.1.1.1", {"start": v(73.61, 52.5) * mm, "end": v(64.95, 52.5) * mm});
            skLineSegment(sketch, "E10.1.1.2", {"start": v(64.95, 52.5) * mm, "end": v(60.62, 60) * mm});
            skLineSegment(sketch, "E10.1.1.3", {"start": v(60.62, 60) * mm, "end": v(64.95, 67.5) * mm});
            skLineSegment(sketch, "E10.1.1.4", {"start": v(64.95, 67.5) * mm, "end": v(73.61, 67.5) * mm});
            skLineSegment(sketch, "E10.1.1.5", {"start": v(73.61, 67.5) * mm, "end": v(77.94, 60) * mm});
            skLineSegment(sketch, "E10.1.2.0", {"start": v(77.94, 100) * mm, "end": v(73.61, 92.5) * mm});
            skLineSegment(sketch, "E10.1.2.1", {"start": v(73.61, 92.5) * mm, "end": v(64.95, 92.5) * mm});
            skLineSegment(sketch, "E10.1.2.2", {"start": v(64.95, 92.5) * mm, "end": v(60.62, 100) * mm});
            skLineSegment(sketch, "E10.1.2.3", {"start": v(60.62, 100) * mm, "end": v(64.95, 107.5) * mm});
            skLineSegment(sketch, "E10.1.2.4", {"start": v(64.95, 107.5) * mm, "end": v(73.61, 107.5) * mm});
            skLineSegment(sketch, "E10.1.2.5", {"start": v(73.61, 107.5) * mm, "end": v(77.94, 100) * mm});
            skLineSegment(sketch, "E10.2.0.0", {"start": v(112.58, 20) * mm, "end": v(108.25, 12.5) * mm});
            skLineSegment(sketch, "E10.2.0.1", {"start": v(108.25, 12.5) * mm, "end": v(99.6, 12.5) * mm});
            skLineSegment(sketch, "E10.2.0.2", {"start": v(99.6, 12.5) * mm, "end": v(95.26, 20) * mm});
            skLineSegment(sketch, "E10.2.0.3", {"start": v(95.26, 20) * mm, "end": v(99.6, 27.5) * mm});
            skLineSegment(sketch, "E10.2.0.4", {"start": v(99.6, 27.5) * mm, "end": v(108.25, 27.5) * mm});
            skLineSegment(sketch, "E10.2.0.5", {"start": v(108.25, 27.5) * mm, "end": v(112.58, 20) * mm});
            skLineSegment(sketch, "E10.2.1.0", {"start": v(112.58, 60) * mm, "end": v(108.25, 52.5) * mm});
            skLineSegment(sketch, "E10.2.1.1", {"start": v(108.25, 52.5) * mm, "end": v(99.6, 52.5) * mm});
            skLineSegment(sketch, "E10.2.1.2", {"start": v(99.6, 52.5) * mm, "end": v(95.26, 60) * mm});
            skLineSegment(sketch, "E10.2.1.3", {"start": v(95.26, 60) * mm, "end": v(99.6, 67.5) * mm});
            skLineSegment(sketch, "E10.2.1.4", {"start": v(99.6, 67.5) * mm, "end": v(108.25, 67.5) * mm});
            skLineSegment(sketch, "E10.2.1.5", {"start": v(108.25, 67.5) * mm, "end": v(112.58, 60) * mm});
            skLineSegment(sketch, "E10.2.2.0", {"start": v(112.58, 100) * mm, "end": v(108.25, 92.5) * mm});
            skLineSegment(sketch, "E10.2.2.1", {"start": v(108.25, 92.5) * mm, "end": v(99.6, 92.5) * mm});
            skLineSegment(sketch, "E10.2.2.2", {"start": v(99.6, 92.5) * mm, "end": v(95.26, 100) * mm});
            skLineSegment(sketch, "E10.2.2.3", {"start": v(95.26, 100) * mm, "end": v(99.6, 107.5) * mm});
            skLineSegment(sketch, "E10.2.2.4", {"start": v(99.6, 107.5) * mm, "end": v(108.25, 107.5) * mm});
            skLineSegment(sketch, "E10.2.2.5", {"start": v(108.25, 107.5) * mm, "end": v(112.58, 100) * mm});
            skLineSegment(sketch, "E10.3.0.0", {"start": v(147.22, 20) * mm, "end": v(142.9, 12.5) * mm});
            skLineSegment(sketch, "E10.3.0.1", {"start": v(142.9, 12.5) * mm, "end": v(134.23, 12.5) * mm});
            skLineSegment(sketch, "E10.3.0.2", {"start": v(134.23, 12.5) * mm, "end": v(129.9, 20) * mm});
            skLineSegment(sketch, "E10.3.0.3", {"start": v(129.9, 20) * mm, "end": v(134.23, 27.5) * mm});
            skLineSegment(sketch, "E10.3.0.4", {"start": v(134.23, 27.5) * mm, "end": v(142.9, 27.5) * mm});
            skLineSegment(sketch, "E10.3.0.5", {"start": v(142.9, 27.5) * mm, "end": v(147.22, 20) * mm});
            skLineSegment(sketch, "E10.3.1.0", {"start": v(147.22, 60) * mm, "end": v(142.9, 52.5) * mm});
            skLineSegment(sketch, "E10.3.1.1", {"start": v(142.9, 52.5) * mm, "end": v(134.23, 52.5) * mm});
            skLineSegment(sketch, "E10.3.1.2", {"start": v(134.23, 52.5) * mm, "end": v(129.9, 60) * mm});
            skLineSegment(sketch, "E10.3.1.3", {"start": v(129.9, 60) * mm, "end": v(134.23, 67.5) * mm});
            skLineSegment(sketch, "E10.3.1.4", {"start": v(134.23, 67.5) * mm, "end": v(142.9, 67.5) * mm});
            skLineSegment(sketch, "E10.3.1.5", {"start": v(142.9, 67.5) * mm, "end": v(147.22, 60) * mm});
            skLineSegment(sketch, "E10.3.2.0", {"start": v(147.22, 100) * mm, "end": v(142.9, 92.5) * mm});
            skLineSegment(sketch, "E10.3.2.1", {"start": v(142.9, 92.5) * mm, "end": v(134.23, 92.5) * mm});
            skLineSegment(sketch, "E10.3.2.2", {"start": v(134.23, 92.5) * mm, "end": v(129.9, 100) * mm});
            skLineSegment(sketch, "E10.3.2.3", {"start": v(129.9, 100) * mm, "end": v(134.23, 107.5) * mm});
            skLineSegment(sketch, "E10.3.2.4", {"start": v(134.23, 107.5) * mm, "end": v(142.9, 107.5) * mm});
            skLineSegment(sketch, "E10.3.2.5", {"start": v(142.9, 107.5) * mm, "end": v(147.22, 100) * mm});
            skLineSegment(sketch, "E10.4.0.0", {"start": v(181.86, 20) * mm, "end": v(177.53, 12.5) * mm});
            skLineSegment(sketch, "E10.4.0.1", {"start": v(177.53, 12.5) * mm, "end": v(168.87, 12.5) * mm});
            skLineSegment(sketch, "E10.4.0.2", {"start": v(168.87, 12.5) * mm, "end": v(164.54, 20) * mm});
            skLineSegment(sketch, "E10.4.0.3", {"start": v(164.54, 20) * mm, "end": v(168.87, 27.5) * mm});
            skLineSegment(sketch, "E10.4.0.4", {"start": v(168.87, 27.5) * mm, "end": v(177.53, 27.5) * mm});
            skLineSegment(sketch, "E10.4.0.5", {"start": v(177.53, 27.5) * mm, "end": v(181.86, 20) * mm});
            skLineSegment(sketch, "E10.4.1.0", {"start": v(181.86, 60) * mm, "end": v(177.53, 52.5) * mm});
            skLineSegment(sketch, "E10.4.1.1", {"start": v(177.53, 52.5) * mm, "end": v(168.87, 52.5) * mm});
            skLineSegment(sketch, "E10.4.1.2", {"start": v(168.87, 52.5) * mm, "end": v(164.54, 60) * mm});
            skLineSegment(sketch, "E10.4.1.3", {"start": v(164.54, 60) * mm, "end": v(168.87, 67.5) * mm});
            skLineSegment(sketch, "E10.4.1.4", {"start": v(168.87, 67.5) * mm, "end": v(177.53, 67.5) * mm});
            skLineSegment(sketch, "E10.4.1.5", {"start": v(177.53, 67.5) * mm, "end": v(181.86, 60) * mm});
            skLineSegment(sketch, "E10.4.2.0", {"start": v(181.86, 100) * mm, "end": v(177.53, 92.5) * mm});
            skLineSegment(sketch, "E10.4.2.1", {"start": v(177.53, 92.5) * mm, "end": v(168.87, 92.5) * mm});
            skLineSegment(sketch, "E10.4.2.2", {"start": v(168.87, 92.5) * mm, "end": v(164.54, 100) * mm});
            skLineSegment(sketch, "E10.4.2.3", {"start": v(164.54, 100) * mm, "end": v(168.87, 107.5) * mm});
            skLineSegment(sketch, "E10.4.2.4", {"start": v(168.87, 107.5) * mm, "end": v(177.53, 107.5) * mm});
            skLineSegment(sketch, "E10.4.2.5", {"start": v(177.53, 107.5) * mm, "end": v(181.86, 100) * mm});
            skLineSegment(sketch, "E10.5.0.0", {"start": v(216.5, 20) * mm, "end": v(212.17, 12.5) * mm});
            skLineSegment(sketch, "E10.5.0.1", {"start": v(212.17, 12.5) * mm, "end": v(203.51, 12.5) * mm});
            skLineSegment(sketch, "E10.5.0.2", {"start": v(203.51, 12.5) * mm, "end": v(199.18, 20) * mm});
            skLineSegment(sketch, "E10.5.0.3", {"start": v(199.18, 20) * mm, "end": v(203.51, 27.5) * mm});
            skLineSegment(sketch, "E10.5.0.4", {"start": v(203.51, 27.5) * mm, "end": v(212.17, 27.5) * mm});
            skLineSegment(sketch, "E10.5.0.5", {"start": v(212.17, 27.5) * mm, "end": v(216.5, 20) * mm});
            skLineSegment(sketch, "E10.5.1.0", {"start": v(216.5, 60) * mm, "end": v(212.17, 52.5) * mm});
            skLineSegment(sketch, "E10.5.1.1", {"start": v(212.17, 52.5) * mm, "end": v(203.51, 52.5) * mm});
            skLineSegment(sketch, "E10.5.1.2", {"start": v(203.51, 52.5) * mm, "end": v(199.18, 60) * mm});
            skLineSegment(sketch, "E10.5.1.3", {"start": v(199.18, 60) * mm, "end": v(203.51, 67.5) * mm});
            skLineSegment(sketch, "E10.5.1.4", {"start": v(203.51, 67.5) * mm, "end": v(212.17, 67.5) * mm});
            skLineSegment(sketch, "E10.5.1.5", {"start": v(212.17, 67.5) * mm, "end": v(216.5, 60) * mm});
            skLineSegment(sketch, "E10.5.2.0", {"start": v(216.5, 100) * mm, "end": v(212.17, 92.5) * mm});
            skLineSegment(sketch, "E10.5.2.1", {"start": v(212.17, 92.5) * mm, "end": v(203.51, 92.5) * mm});
            skLineSegment(sketch, "E10.5.2.2", {"start": v(203.51, 92.5) * mm, "end": v(199.18, 100) * mm});
            skLineSegment(sketch, "E10.5.2.3", {"start": v(199.18, 100) * mm, "end": v(203.51, 107.5) * mm});
            skLineSegment(sketch, "E10.5.2.4", {"start": v(203.51, 107.5) * mm, "end": v(212.17, 107.5) * mm});
            skLineSegment(sketch, "E10.5.2.5", {"start": v(212.17, 107.5) * mm, "end": v(216.5, 100) * mm});
            skLineSegment(sketch, "E10.6.0.0", {"start": v(251.14, 20) * mm, "end": v(246.81, 12.5) * mm});
            skLineSegment(sketch, "E10.6.0.1", {"start": v(246.81, 12.5) * mm, "end": v(238.15, 12.5) * mm});
            skLineSegment(sketch, "E10.6.0.2", {"start": v(238.15, 12.5) * mm, "end": v(233.82, 20) * mm});
            skLineSegment(sketch, "E10.6.0.3", {"start": v(233.82, 20) * mm, "end": v(238.15, 27.5) * mm});
            skLineSegment(sketch, "E10.6.0.4", {"start": v(238.15, 27.5) * mm, "end": v(246.81, 27.5) * mm});
            skLineSegment(sketch, "E10.6.0.5", {"start": v(246.81, 27.5) * mm, "end": v(251.14, 20) * mm});
            skLineSegment(sketch, "E10.6.1.0", {"start": v(251.14, 60) * mm, "end": v(246.81, 52.5) * mm});
            skLineSegment(sketch, "E10.6.1.1", {"start": v(246.81, 52.5) * mm, "end": v(238.15, 52.5) * mm});
            skLineSegment(sketch, "E10.6.1.2", {"start": v(238.15, 52.5) * mm, "end": v(233.82, 60) * mm});
            skLineSegment(sketch, "E10.6.1.3", {"start": v(233.82, 60) * mm, "end": v(238.15, 67.5) * mm});
            skLineSegment(sketch, "E10.6.1.4", {"start": v(238.15, 67.5) * mm, "end": v(246.81, 67.5) * mm});
            skLineSegment(sketch, "E10.6.1.5", {"start": v(246.81, 67.5) * mm, "end": v(251.14, 60) * mm});
            skLineSegment(sketch, "E10.6.2.0", {"start": v(251.14, 100) * mm, "end": v(246.81, 92.5) * mm});
            skLineSegment(sketch, "E10.6.2.1", {"start": v(246.81, 92.5) * mm, "end": v(238.15, 92.5) * mm});
            skLineSegment(sketch, "E10.6.2.2", {"start": v(238.15, 92.5) * mm, "end": v(233.82, 100) * mm});
            skLineSegment(sketch, "E10.6.2.3", {"start": v(233.82, 100) * mm, "end": v(238.15, 107.5) * mm});
            skLineSegment(sketch, "E10.6.2.4", {"start": v(238.15, 107.5) * mm, "end": v(246.81, 107.5) * mm});
            skLineSegment(sketch, "E10.6.2.5", {"start": v(246.81, 107.5) * mm, "end": v(251.14, 100) * mm});
            skLineSegment(sketch, "E10.7.0.0", {"start": v(285.78, 20) * mm, "end": v(281.45, 12.5) * mm});
            skLineSegment(sketch, "E10.7.0.1", {"start": v(281.45, 12.5) * mm, "end": v(272.8, 12.5) * mm});
            skLineSegment(sketch, "E10.7.0.2", {"start": v(272.8, 12.5) * mm, "end": v(268.46, 20) * mm});
            skLineSegment(sketch, "E10.7.0.3", {"start": v(268.46, 20) * mm, "end": v(272.8, 27.5) * mm});
            skLineSegment(sketch, "E10.7.0.4", {"start": v(272.8, 27.5) * mm, "end": v(281.45, 27.5) * mm});
            skLineSegment(sketch, "E10.7.0.5", {"start": v(281.45, 27.5) * mm, "end": v(285.78, 20) * mm});
            skLineSegment(sketch, "E10.7.1.0", {"start": v(285.78, 60) * mm, "end": v(281.45, 52.5) * mm});
            skLineSegment(sketch, "E10.7.1.1", {"start": v(281.45, 52.5) * mm, "end": v(272.8, 52.5) * mm});
            skLineSegment(sketch, "E10.7.1.2", {"start": v(272.8, 52.5) * mm, "end": v(268.46, 60) * mm});
            skLineSegment(sketch, "E10.7.1.3", {"start": v(268.46, 60) * mm, "end": v(272.8, 67.5) * mm});
            skLineSegment(sketch, "E10.7.1.4", {"start": v(272.8, 67.5) * mm, "end": v(281.45, 67.5) * mm});
            skLineSegment(sketch, "E10.7.1.5", {"start": v(281.45, 67.5) * mm, "end": v(285.78, 60) * mm});
            skLineSegment(sketch, "E10.7.2.0", {"start": v(285.78, 100) * mm, "end": v(281.45, 92.5) * mm});
            skLineSegment(sketch, "E10.7.2.1", {"start": v(281.45, 92.5) * mm, "end": v(272.8, 92.5) * mm});
            skLineSegment(sketch, "E10.7.2.2", {"start": v(272.8, 92.5) * mm, "end": v(268.46, 100) * mm});
            skLineSegment(sketch, "E10.7.2.3", {"start": v(268.46, 100) * mm, "end": v(272.8, 107.5) * mm});
            skLineSegment(sketch, "E10.7.2.4", {"start": v(272.8, 107.5) * mm, "end": v(281.45, 107.5) * mm});
            skLineSegment(sketch, "E10.7.2.5", {"start": v(281.45, 107.5) * mm, "end": v(285.78, 100) * mm});
            skLineSegment(sketch, "E10.8.0.0", {"start": v(320.42, 20) * mm, "end": v(316.1, 12.5) * mm});
            skLineSegment(sketch, "E10.8.0.1", {"start": v(316.1, 12.5) * mm, "end": v(307.43, 12.5) * mm});
            skLineSegment(sketch, "E10.8.0.2", {"start": v(307.43, 12.5) * mm, "end": v(303.1, 20) * mm});
            skLineSegment(sketch, "E10.8.0.3", {"start": v(303.1, 20) * mm, "end": v(307.43, 27.5) * mm});
            skLineSegment(sketch, "E10.8.0.4", {"start": v(307.43, 27.5) * mm, "end": v(316.1, 27.5) * mm});
            skLineSegment(sketch, "E10.8.0.5", {"start": v(316.1, 27.5) * mm, "end": v(320.42, 20) * mm});
            skLineSegment(sketch, "E10.8.1.0", {"start": v(320.42, 60) * mm, "end": v(316.1, 52.5) * mm});
            skLineSegment(sketch, "E10.8.1.1", {"start": v(316.1, 52.5) * mm, "end": v(307.43, 52.5) * mm});
            skLineSegment(sketch, "E10.8.1.2", {"start": v(307.43, 52.5) * mm, "end": v(303.1, 60) * mm});
            skLineSegment(sketch, "E10.8.1.3", {"start": v(303.1, 60) * mm, "end": v(307.43, 67.5) * mm});
            skLineSegment(sketch, "E10.8.1.4", {"start": v(307.43, 67.5) * mm, "end": v(316.1, 67.5) * mm});
            skLineSegment(sketch, "E10.8.1.5", {"start": v(316.1, 67.5) * mm, "end": v(320.42, 60) * mm});
            skLineSegment(sketch, "E10.8.2.0", {"start": v(320.42, 100) * mm, "end": v(316.1, 92.5) * mm});
            skLineSegment(sketch, "E10.8.2.1", {"start": v(316.1, 92.5) * mm, "end": v(307.43, 92.5) * mm});
            skLineSegment(sketch, "E10.8.2.2", {"start": v(307.43, 92.5) * mm, "end": v(303.1, 100) * mm});
            skLineSegment(sketch, "E10.8.2.3", {"start": v(303.1, 100) * mm, "end": v(307.43, 107.5) * mm});
            skLineSegment(sketch, "E10.8.2.4", {"start": v(307.43, 107.5) * mm, "end": v(316.1, 107.5) * mm});
            skLineSegment(sketch, "E10.8.2.5", {"start": v(316.1, 107.5) * mm, "end": v(320.42, 100) * mm});
            skLineSegment(sketch, "E10.9.0.0", {"start": v(355.06, 20) * mm, "end": v(350.73, 12.5) * mm});
            skLineSegment(sketch, "E10.9.0.1", {"start": v(350.73, 12.5) * mm, "end": v(342.07, 12.5) * mm});
            skLineSegment(sketch, "E10.9.0.2", {"start": v(342.07, 12.5) * mm, "end": v(337.74, 20) * mm});
            skLineSegment(sketch, "E10.9.0.3", {"start": v(337.74, 20) * mm, "end": v(342.07, 27.5) * mm});
            skLineSegment(sketch, "E10.9.0.4", {"start": v(342.07, 27.5) * mm, "end": v(350.73, 27.5) * mm});
            skLineSegment(sketch, "E10.9.0.5", {"start": v(350.73, 27.5) * mm, "end": v(355.06, 20) * mm});
            skLineSegment(sketch, "E10.9.1.0", {"start": v(355.06, 60) * mm, "end": v(350.73, 52.5) * mm});
            skLineSegment(sketch, "E10.9.1.1", {"start": v(350.73, 52.5) * mm, "end": v(342.07, 52.5) * mm});
            skLineSegment(sketch, "E10.9.1.2", {"start": v(342.07, 52.5) * mm, "end": v(337.74, 60) * mm});
            skLineSegment(sketch, "E10.9.1.3", {"start": v(337.74, 60) * mm, "end": v(342.07, 67.5) * mm});
            skLineSegment(sketch, "E10.9.1.4", {"start": v(342.07, 67.5) * mm, "end": v(350.73, 67.5) * mm});
            skLineSegment(sketch, "E10.9.1.5", {"start": v(350.73, 67.5) * mm, "end": v(355.06, 60) * mm});
            skLineSegment(sketch, "E10.9.2.0", {"start": v(355.06, 100) * mm, "end": v(350.73, 92.5) * mm});
            skLineSegment(sketch, "E10.9.2.1", {"start": v(350.73, 92.5) * mm, "end": v(342.07, 92.5) * mm});
            skLineSegment(sketch, "E10.9.2.2", {"start": v(342.07, 92.5) * mm, "end": v(337.74, 100) * mm});
            skLineSegment(sketch, "E10.9.2.3", {"start": v(337.74, 100) * mm, "end": v(342.07, 107.5) * mm});
            skLineSegment(sketch, "E10.9.2.4", {"start": v(342.07, 107.5) * mm, "end": v(350.73, 107.5) * mm});
            skLineSegment(sketch, "E10.9.2.5", {"start": v(350.73, 107.5) * mm, "end": v(355.06, 100) * mm});
            skLineSegment(sketch, "E10.10.0.0", {"start": v(389.7, 20) * mm, "end": v(385.37, 12.5) * mm});
            skLineSegment(sketch, "E10.10.0.1", {"start": v(385.37, 12.5) * mm, "end": v(376.71, 12.5) * mm});
            skLineSegment(sketch, "E10.10.0.2", {"start": v(376.71, 12.5) * mm, "end": v(372.38, 20) * mm});
            skLineSegment(sketch, "E10.10.0.3", {"start": v(372.38, 20) * mm, "end": v(376.71, 27.5) * mm});
            skLineSegment(sketch, "E10.10.0.4", {"start": v(376.71, 27.5) * mm, "end": v(385.37, 27.5) * mm});
            skLineSegment(sketch, "E10.10.0.5", {"start": v(385.37, 27.5) * mm, "end": v(389.7, 20) * mm});
            skLineSegment(sketch, "E10.10.1.0", {"start": v(389.7, 60) * mm, "end": v(385.37, 52.5) * mm});
            skLineSegment(sketch, "E10.10.1.1", {"start": v(385.37, 52.5) * mm, "end": v(376.71, 52.5) * mm});
            skLineSegment(sketch, "E10.10.1.2", {"start": v(376.71, 52.5) * mm, "end": v(372.38, 60) * mm});
            skLineSegment(sketch, "E10.10.1.3", {"start": v(372.38, 60) * mm, "end": v(376.71, 67.5) * mm});
            skLineSegment(sketch, "E10.10.1.4", {"start": v(376.71, 67.5) * mm, "end": v(385.37, 67.5) * mm});
            skLineSegment(sketch, "E10.10.1.5", {"start": v(385.37, 67.5) * mm, "end": v(389.7, 60) * mm});
            skLineSegment(sketch, "E10.10.2.0", {"start": v(389.7, 100) * mm, "end": v(385.37, 92.5) * mm});
            skLineSegment(sketch, "E10.10.2.1", {"start": v(385.37, 92.5) * mm, "end": v(376.71, 92.5) * mm});
            skLineSegment(sketch, "E10.10.2.2", {"start": v(376.71, 92.5) * mm, "end": v(372.38, 100) * mm});
            skLineSegment(sketch, "E10.10.2.3", {"start": v(372.38, 100) * mm, "end": v(376.71, 107.5) * mm});
            skLineSegment(sketch, "E10.10.2.4", {"start": v(376.71, 107.5) * mm, "end": v(385.37, 107.5) * mm});
            skLineSegment(sketch, "E10.10.2.5", {"start": v(385.37, 107.5) * mm, "end": v(389.7, 100) * mm});
            skLineSegment(sketch, "E10.direction2", {"start": v(30.31, 12.5) * mm, "end": v(30.31, 52.5) * mm, "construction": true});
            skLineSegment(sketch, "E11.left", {"start": v(16.84, 122.52) * mm, "end": v(16.84, 117.5) * mm});
            skLineSegment(sketch, "E12.1.0.1", {"start": v(437.33, 57.5) * mm, "end": v(441.66, 50) * mm});
            skLineSegment(sketch, "E12.1.0.2", {"start": v(437.33, 62.5) * mm, "end": v(428.67, 62.5) * mm});
            skCircle(sketch, "E12.1.0.3", {"center": v(415.68, 40) * mm, "radius": 7.5 * mm, "construction": true});
            skPoint(sketch, "E12.1.0.4", {"position": v(433, 117.5) * mm});
            skLineSegment(sketch, "E12.1.0.5", {"start": v(407.02, 120) * mm, "end": v(424.34, 120) * mm, "construction": true});
            skLineSegment(sketch, "E12.1.0.6", {"start": v(420.01, 112.5) * mm, "end": v(411.35, 112.5) * mm});
            skLineSegment(sketch, "E12.1.0.8", {"start": v(411.35, 52.5) * mm, "end": v(407.02, 60) * mm});
            skLineSegment(sketch, "E12.1.0.9", {"start": v(407.02, 100) * mm, "end": v(411.35, 107.5) * mm});
            skLineSegment(sketch, "E12.1.0.10", {"start": v(420.01, 32.5) * mm, "end": v(411.35, 32.5) * mm});
            skLineSegment(sketch, "E12.1.0.11", {"start": v(424.34, 60) * mm, "end": v(420.01, 52.5) * mm});
            skLineSegment(sketch, "E12.1.0.12", {"start": v(411.35, 107.5) * mm, "end": v(420.01, 107.5) * mm});
            skLineSegment(sketch, "E12.1.0.14", {"start": v(407.02, 0) * mm, "end": v(424.34, 0) * mm, "construction": true});
            skLineSegment(sketch, "E12.1.0.15", {"start": v(441.66, 10) * mm, "end": v(437.33, 2.5) * mm});
            skCircle(sketch, "E12.1.0.16", {"center": v(433, 10) * mm, "radius": 7.5 * mm, "construction": true});
            skCircle(sketch, "E12.1.0.17", {"center": v(415.68, 0) * mm, "radius": 7.5 * mm, "construction": true});
            skLineSegment(sketch, "E12.1.0.18", {"start": v(420.01, 72.5) * mm, "end": v(411.35, 72.5) * mm});
            skLineSegment(sketch, "E12.1.0.19", {"start": v(420.01, 7.5) * mm, "end": v(424.34, 0) * mm});
            skLineSegment(sketch, "E12.1.0.20", {"start": v(437.33, 22.5) * mm, "end": v(428.67, 22.5) * mm});
            skLineSegment(sketch, "E12.1.0.21", {"start": v(420.01, 92.5) * mm, "end": v(411.35, 92.5) * mm});
            skLineSegment(sketch, "E12.1.0.22", {"start": v(407.02, 40) * mm, "end": v(424.34, 40) * mm, "construction": true});
            skCircle(sketch, "E12.1.0.23", {"center": v(433, 50) * mm, "radius": 7.5 * mm, "construction": true});
            skLineSegment(sketch, "E12.1.0.24", {"start": v(420.01, -7.5) * mm, "end": v(411.35, -7.5) * mm});
            skCircle(sketch, "E12.1.0.25", {"center": v(415.68, 120) * mm, "radius": 7.5 * mm, "construction": true});
            skCircle(sketch, "E12.1.0.26", {"center": v(433, 110) * mm, "radius": 7.5 * mm, "construction": true});
            skLineSegment(sketch, "E12.1.0.27", {"start": v(437.33, 122.5) * mm, "end": v(428.67, 122.5) * mm});
            skCircle(sketch, "E12.1.0.28", {"center": v(433, 90) * mm, "radius": 7.5 * mm, "construction": true});
            skPoint(sketch, "E12.1.0.30", {"position": v(433, 17.5) * mm});
            skCircle(sketch, "E12.1.0.31", {"center": v(415.68, 80) * mm, "radius": 7.5 * mm, "construction": true});
            skPoint(sketch, "E12.1.0.32", {"position": v(433, 37.5) * mm});
            skPoint(sketch, "E12.1.0.33", {"position": v(433, 97.5) * mm});
            skPoint(sketch, "E12.1.0.34", {"position": v(415.68, 87.5) * mm});
            skLineSegment(sketch, "E12.1.0.35", {"start": v(420.01, 12.5) * mm, "end": v(411.35, 12.5) * mm});
            skPoint(sketch, "E12.1.0.36", {"position": v(433, 57.5) * mm});
            skLineSegment(sketch, "E12.1.0.37", {"start": v(441.66, 110) * mm, "end": v(437.33, 102.5) * mm});
            skPoint(sketch, "E12.1.0.38", {"position": v(433, -2.5) * mm});
            skLineSegment(sketch, "E12.1.0.40", {"start": v(411.35, 27.5) * mm, "end": v(420.01, 27.5) * mm});
            skLineSegment(sketch, "E12.1.0.41", {"start": v(420.01, 52.5) * mm, "end": v(411.35, 52.5) * mm});
            skPoint(sketch, "E12.1.0.42", {"position": v(433, 77.5) * mm});
            skPoint(sketch, "E12.1.0.43", {"position": v(415.68, 47.5) * mm});
            skPoint(sketch, "E12.1.0.44", {"position": v(415.68, 7.5) * mm});
            skLineSegment(sketch, "E12.1.0.45", {"start": v(407.02, 80) * mm, "end": v(424.34, 80) * mm, "construction": true});
            skLineSegment(sketch, "E12.1.0.46", {"start": v(411.35, 67.5) * mm, "end": v(420.01, 67.5) * mm});
            skLineSegment(sketch, "E12.1.0.47", {"start": v(420.01, 107.5) * mm, "end": v(424.34, 100) * mm});
            skLineSegment(sketch, "E12.1.0.48", {"start": v(424.34, 50) * mm, "end": v(428.67, 57.5) * mm});
            skLineSegment(sketch, "E12.1.0.49", {"start": v(428.67, 2.5) * mm, "end": v(424.34, 10) * mm});
            skLineSegment(sketch, "E12.1.0.50", {"start": v(437.33, 2.5) * mm, "end": v(428.67, 2.5) * mm});
            skLineSegment(sketch, "E12.1.0.51", {"start": v(428.67, -2.5) * mm, "end": v(437.33, -2.5) * mm});
            skLineSegment(sketch, "E12.1.0.54", {"start": v(428.67, 97.5) * mm, "end": v(437.33, 97.5) * mm});
            skLineSegment(sketch, "E12.1.0.55", {"start": v(411.35, 47.5) * mm, "end": v(420.01, 47.5) * mm});
            skLineSegment(sketch, "E12.1.0.56", {"start": v(428.67, 57.5) * mm, "end": v(437.33, 57.5) * mm});
            skLineSegment(sketch, "E12.1.0.58", {"start": v(437.33, 42.5) * mm, "end": v(428.67, 42.5) * mm});
            skLineSegment(sketch, "E12.1.0.59", {"start": v(428.67, 37.5) * mm, "end": v(437.33, 37.5) * mm});
            skCircle(sketch, "E12.1.0.60", {"center": v(433, 30) * mm, "radius": 7.5 * mm, "construction": true});
            skLineSegment(sketch, "E12.1.0.61", {"start": v(437.33, 82.5) * mm, "end": v(428.67, 82.5) * mm});
            skLineSegment(sketch, "E12.1.0.62", {"start": v(407.02, 0) * mm, "end": v(411.35, 7.5) * mm});
            skLineSegment(sketch, "E12.1.0.63", {"start": v(411.35, 7.5) * mm, "end": v(420.01, 7.5) * mm});
            skCircle(sketch, "E12.1.0.64", {"center": v(433, 70) * mm, "radius": 7.5 * mm, "construction": true});
            skLineSegment(sketch, "E12.1.0.65", {"start": v(428.67, 17.5) * mm, "end": v(437.33, 17.5) * mm});
            skLineSegment(sketch, "E12.1.0.66", {"start": v(428.67, 77.5) * mm, "end": v(437.33, 77.5) * mm});
            skLineSegment(sketch, "E12.1.0.67", {"start": v(428.67, 117.5) * mm, "end": v(437.33, 117.5) * mm});
            skLineSegment(sketch, "E12.1.0.68", {"start": v(428.67, 102.5) * mm, "end": v(424.34, 110) * mm});
            skLineSegment(sketch, "E12.1.0.69", {"start": v(411.35, 87.5) * mm, "end": v(420.01, 87.5) * mm});
            skLineSegment(sketch, "E12.1.0.70", {"start": v(437.33, 102.5) * mm, "end": v(428.67, 102.5) * mm});
            skLineSegment(sketch, "E12.1.0.71", {"start": v(411.35, 127.5) * mm, "end": v(420.01, 127.5) * mm});
            skLineSegment(sketch, "E12.1.0.72", {"start": v(407.02, 40) * mm, "end": v(411.35, 47.5) * mm});
            skLineSegment(sketch, "E12.1.0.73", {"start": v(441.66, 70) * mm, "end": v(437.33, 62.5) * mm});
            skLineSegment(sketch, "E12.1.0.74", {"start": v(437.33, 37.5) * mm, "end": v(441.66, 30) * mm});
            skLineSegment(sketch, "E12.1.0.75", {"start": v(424.34, 0) * mm, "end": v(420.01, -7.5) * mm});
            skLineSegment(sketch, "E12.1.0.76", {"start": v(424.34, 30) * mm, "end": v(428.67, 37.5) * mm});
            skLineSegment(sketch, "E12.1.0.77", {"start": v(420.01, 47.5) * mm, "end": v(424.34, 40) * mm});
            skLineSegment(sketch, "E12.1.0.78", {"start": v(428.67, 62.5) * mm, "end": v(424.34, 70) * mm});
            skLineSegment(sketch, "E12.1.0.79", {"start": v(424.34, 90) * mm, "end": v(428.67, 97.5) * mm});
            skLineSegment(sketch, "E12.1.0.80", {"start": v(441.66, 90) * mm, "end": v(437.33, 82.5) * mm});
            skLineSegment(sketch, "E12.1.0.81", {"start": v(428.67, 122.5) * mm, "end": v(424.34, 130) * mm});
            skLineSegment(sketch, "E12.1.0.82", {"start": v(424.34, 100) * mm, "end": v(420.01, 92.5) * mm});
            skLineSegment(sketch, "E12.1.0.83", {"start": v(407.02, 20) * mm, "end": v(411.35, 27.5) * mm});
            skLineSegment(sketch, "E12.1.0.84", {"start": v(420.01, 27.5) * mm, "end": v(424.34, 20) * mm});
            skLineSegment(sketch, "E12.1.0.86", {"start": v(411.35, 32.5) * mm, "end": v(407.02, 40) * mm});
            skLineSegment(sketch, "E12.1.0.88", {"start": v(407.02, 60) * mm, "end": v(411.35, 67.5) * mm});
            skLineSegment(sketch, "E12.1.0.90", {"start": v(424.34, 40) * mm, "end": v(420.01, 32.5) * mm});
            skLineSegment(sketch, "E12.1.0.91", {"start": v(424.34, 70) * mm, "end": v(428.67, 77.5) * mm});
            skLineSegment(sketch, "E12.1.0.92", {"start": v(428.67, 42.5) * mm, "end": v(424.34, 50) * mm});
            skLineSegment(sketch, "E12.1.0.93", {"start": v(437.33, 97.5) * mm, "end": v(441.66, 90) * mm});
            skLineSegment(sketch, "E12.1.0.94", {"start": v(407.02, 80) * mm, "end": v(411.35, 87.5) * mm});
            skLineSegment(sketch, "E12.1.0.95", {"start": v(428.67, 22.5) * mm, "end": v(424.34, 30) * mm});
            skLineSegment(sketch, "E12.1.0.96", {"start": v(411.35, 72.5) * mm, "end": v(407.02, 80) * mm});
            skLineSegment(sketch, "E12.1.0.97", {"start": v(424.34, -10) * mm, "end": v(428.67, -2.5) * mm});
            skLineSegment(sketch, "E12.1.0.98", {"start": v(437.33, 17.5) * mm, "end": v(441.66, 10) * mm});
            skLineSegment(sketch, "E12.1.0.99", {"start": v(437.33, -2.5) * mm, "end": v(441.66, -10) * mm});
            skLineSegment(sketch, "E12.1.0.100", {"start": v(441.66, 30) * mm, "end": v(437.33, 22.5) * mm});
            skLineSegment(sketch, "E12.1.0.101", {"start": v(424.34, 10) * mm, "end": v(428.67, 17.5) * mm});
            skLineSegment(sketch, "E12.1.0.102", {"start": v(424.34, 80) * mm, "end": v(420.01, 72.5) * mm});
            skLineSegment(sketch, "E12.1.0.103", {"start": v(441.66, 50) * mm, "end": v(437.33, 42.5) * mm});
            skLineSegment(sketch, "E12.1.0.104", {"start": v(428.67, 82.5) * mm, "end": v(424.34, 90) * mm});
            skLineSegment(sketch, "E12.1.0.105", {"start": v(411.35, -7.5) * mm, "end": v(407.02, 0) * mm});
            skLineSegment(sketch, "E12.1.0.106", {"start": v(424.34, 20) * mm, "end": v(420.01, 12.5) * mm});
            skLineSegment(sketch, "E12.1.0.107", {"start": v(424.34, 110) * mm, "end": v(428.67, 117.5) * mm});
            skLineSegment(sketch, "E12.1.0.108", {"start": v(420.01, 127.5) * mm, "end": v(424.34, 120) * mm});
            skLineSegment(sketch, "E12.1.0.109", {"start": v(437.33, 77.5) * mm, "end": v(441.66, 70) * mm});
            skLineSegment(sketch, "E12.1.0.111", {"start": v(407.02, 120) * mm, "end": v(411.35, 127.5) * mm});
            skLineSegment(sketch, "E12.1.0.112", {"start": v(441.66, 130) * mm, "end": v(437.33, 122.5) * mm});
            skLineSegment(sketch, "E12.1.0.114", {"start": v(420.01, 67.5) * mm, "end": v(424.34, 60) * mm});
            skLineSegment(sketch, "E12.1.0.115", {"start": v(411.35, 12.5) * mm, "end": v(407.02, 20) * mm});
            skLineSegment(sketch, "E12.1.0.116", {"start": v(420.01, 87.5) * mm, "end": v(424.34, 80) * mm});
            skLineSegment(sketch, "E12.1.0.119", {"start": v(411.35, 92.5) * mm, "end": v(407.02, 100) * mm});
            skLineSegment(sketch, "E12.1.0.120", {"start": v(411.35, 112.5) * mm, "end": v(407.02, 120) * mm});
            skLineSegment(sketch, "E12.1.0.121", {"start": v(424.34, 120) * mm, "end": v(420.01, 112.5) * mm});
            skLineSegment(sketch, "E12.1.0.122", {"start": v(437.33, 117.5) * mm, "end": v(441.66, 110) * mm});
            skLineSegment(sketch, "E12.2.0.6", {"start": v(450.32, 112.5) * mm, "end": v(445.99, 112.5) * mm});
            skLineSegment(sketch, "E12.2.0.8", {"start": v(446, 52.5) * mm, "end": v(441.66, 60) * mm});
            skLineSegment(sketch, "E12.2.0.9", {"start": v(441.66, 100) * mm, "end": v(446, 107.5) * mm});
            skLineSegment(sketch, "E12.2.0.12", {"start": v(446, 107.5) * mm, "end": v(450.32, 107.5) * mm});
            skLineSegment(sketch, "E12.2.0.18", {"start": v(450.32, 72.5) * mm, "end": v(445.99, 72.5) * mm});
            skLineSegment(sketch, "E12.2.0.21", {"start": v(450.32, 92.5) * mm, "end": v(446, 92.5) * mm});
            skLineSegment(sketch, "E12.2.0.24", {"start": v(450.32, -7.5) * mm, "end": v(445.99, -7.5) * mm});
            skPoint(sketch, "E12.2.0.34", {"position": v(450.32, 87.5) * mm});
            skLineSegment(sketch, "E12.2.0.35", {"start": v(450.32, 12.5) * mm, "end": v(446, 12.5) * mm});
            skLineSegment(sketch, "E12.2.0.40", {"start": v(446, 27.5) * mm, "end": v(450.32, 27.5) * mm});
            skLineSegment(sketch, "E12.2.0.41", {"start": v(450.32, 52.5) * mm, "end": v(446, 52.5) * mm});
            skPoint(sketch, "E12.2.0.43", {"position": v(450.32, 47.5) * mm});
            skPoint(sketch, "E12.2.0.44", {"position": v(450.32, 7.5) * mm});
            skLineSegment(sketch, "E12.2.0.46", {"start": v(446, 67.5) * mm, "end": v(450.32, 67.5) * mm});
            skLineSegment(sketch, "E12.2.0.55", {"start": v(445.99, 47.5) * mm, "end": v(450.32, 47.5) * mm});
            skLineSegment(sketch, "E12.2.0.62", {"start": v(441.66, 0) * mm, "end": v(445.99, 7.5) * mm});
            skLineSegment(sketch, "E12.2.0.63", {"start": v(445.99, 7.5) * mm, "end": v(450.32, 7.5) * mm});
            skLineSegment(sketch, "E12.2.0.69", {"start": v(445.99, 87.5) * mm, "end": v(450.32, 87.5) * mm});
            skLineSegment(sketch, "E12.2.0.71", {"start": v(445.99, 127.5) * mm, "end": v(450.32, 127.5) * mm});
            skLineSegment(sketch, "E12.2.0.72", {"start": v(441.66, 40) * mm, "end": v(445.99, 47.5) * mm});
            skLineSegment(sketch, "E12.2.0.83", {"start": v(441.66, 20) * mm, "end": v(446, 27.5) * mm});
            skLineSegment(sketch, "E12.2.0.86", {"start": v(445.99, 32.5) * mm, "end": v(441.66, 40) * mm});
            skLineSegment(sketch, "E12.2.0.88", {"start": v(441.66, 60) * mm, "end": v(446, 67.5) * mm});
            skLineSegment(sketch, "E12.2.0.94", {"start": v(441.66, 80) * mm, "end": v(445.99, 87.5) * mm});
            skLineSegment(sketch, "E12.2.0.96", {"start": v(445.99, 72.5) * mm, "end": v(441.66, 80) * mm});
            skLineSegment(sketch, "E12.2.0.105", {"start": v(445.99, -7.5) * mm, "end": v(441.66, 0) * mm});
            skLineSegment(sketch, "E12.2.0.111", {"start": v(441.66, 120) * mm, "end": v(445.99, 127.5) * mm});
            skLineSegment(sketch, "E12.2.0.115", {"start": v(446, 12.5) * mm, "end": v(441.66, 20) * mm});
            skLineSegment(sketch, "E12.2.0.119", {"start": v(446, 92.5) * mm, "end": v(441.66, 100) * mm});
            skLineSegment(sketch, "E12.2.0.120", {"start": v(445.99, 112.5) * mm, "end": v(441.66, 120) * mm});
            skLineSegment(sketch, "E12.direction1", {"start": v(376.7, -7.5) * mm, "end": v(411.35, -7.5) * mm, "construction": true});
            skLineSegment(sketch, "E13", {"start": v(450.32, 129.98) * mm, "end": v(450.32, 127.5) * mm});
            skLineSegment(sketch, "E14.trimOffspring", {"start": v(16.84, 102.52) * mm, "end": v(16.84, 97.48) * mm});
            skLineSegment(sketch, "E15.trimOffspring", {"start": v(16.84, 62.52) * mm, "end": v(16.84, 57.5) * mm});
            skLineSegment(sketch, "E16.trimOffspring", {"start": v(16.84, 82.52) * mm, "end": v(16.84, 77.48) * mm});
            skLineSegment(sketch, "E17.trimOffspring", {"start": v(16.84, 42.52) * mm, "end": v(16.84, 37.48) * mm});
            skLineSegment(sketch, "E18.trimOffspring", {"start": v(16.84, 22.52) * mm, "end": v(16.84, 17.48) * mm});
            skPoint(sketch, "E19.orphan", {"position": v(13, 17.5) * mm});
            skLineSegment(sketch, "E20.trimOffspring", {"start": v(16.84, 2.52) * mm, "end": v(16.84, -2.5) * mm});
            skLineSegment(sketch, "E21", {"start": v(25.98, -10) * mm, "end": v(43.3, -10) * mm});
            skLineSegment(sketch, "E22", {"start": v(60.62, -10) * mm, "end": v(77.94, -10) * mm});
            skLineSegment(sketch, "E23", {"start": v(95.26, -10) * mm, "end": v(112.58, -10) * mm});
            skLineSegment(sketch, "E24", {"start": v(129.9, -10) * mm, "end": v(147.22, -10) * mm});
            skLineSegment(sketch, "E25", {"start": v(164.54, -10) * mm, "end": v(181.86, -10) * mm});
            skLineSegment(sketch, "E26", {"start": v(199.18, -10) * mm, "end": v(216.5, -10) * mm});
            skLineSegment(sketch, "E27", {"start": v(233.82, -10) * mm, "end": v(251.14, -10) * mm});
            skLineSegment(sketch, "E28", {"start": v(268.46, -10) * mm, "end": v(285.78, -10) * mm});
            skLineSegment(sketch, "E29", {"start": v(303.1, -10) * mm, "end": v(320.42, -10) * mm});
            skLineSegment(sketch, "E30", {"start": v(337.74, -10) * mm, "end": v(355.06, -10) * mm});
            skLineSegment(sketch, "E31", {"start": v(372.38, -10) * mm, "end": v(389.7, -10) * mm});
            skLineSegment(sketch, "E32", {"start": v(407.02, -10) * mm, "end": v(424.34, -10) * mm});
            skLineSegment(sketch, "E33", {"start": v(441.66, -10) * mm, "end": v(450.32, -10.02) * mm});
            skLineSegment(sketch, "E34.trimOffspring", {"start": v(450.32, -7.5) * mm, "end": v(450.32, -10.02) * mm});
            skPoint(sketch, "E35.orphan", {"position": v(454.65, -7.5) * mm});
            skPoint(sketch, "E36.orphan", {"position": v(454.65, 7.5) * mm});
            skPoint(sketch, "E37.orphan", {"position": v(454.65, 12.5) * mm});
            skLineSegment(sketch, "E38.trimOffspring", {"start": v(450.32, 12.5) * mm, "end": v(450.32, 7.5) * mm});
            skPoint(sketch, "E39.orphan", {"position": v(454.65, 27.5) * mm});
            skPoint(sketch, "E40.orphan", {"position": v(454.65, 32.5) * mm});
            skPoint(sketch, "E41.orphan", {"position": v(454.65, 47.5) * mm});
            skPoint(sketch, "E42.orphan", {"position": v(454.65, 52.5) * mm});
            skLineSegment(sketch, "E43.trimOffspring", {"start": v(450.32, 52.5) * mm, "end": v(450.32, 47.5) * mm});
            skPoint(sketch, "E44.orphan", {"position": v(454.65, 67.5) * mm});
            skPoint(sketch, "E45.orphan", {"position": v(454.65, 72.5) * mm});
            skLineSegment(sketch, "E46.trimOffspring", {"start": v(450.32, 72.5) * mm, "end": v(450.32, 67.5) * mm});
            skLineSegment(sketch, "E47", {"start": v(450.36, 27.75) * mm, "end": v(450.26, 32.5) * mm});
            skLineSegment(sketch, "E48", {"start": v(445.99, 32.5) * mm, "end": v(450.26, 32.5) * mm});
            skPoint(sketch, "E49.orphan", {"position": v(454.65, 87.5) * mm});
            skPoint(sketch, "E50.orphan", {"position": v(454.65, 92.5) * mm});
            skLineSegment(sketch, "E51.trimOffspring", {"start": v(450.32, 92.5) * mm, "end": v(450.32, 87.5) * mm});
            skPoint(sketch, "E52.orphan", {"position": v(454.65, 107.5) * mm});
            skPoint(sketch, "E53.orphan", {"position": v(454.65, 112.5) * mm});
            skLineSegment(sketch, "E54.trimOffspring", {"start": v(450.32, 112.5) * mm, "end": v(450.32, 107.5) * mm});
            skPoint(sketch, "E55.orphan", {"position": v(454.65, 127.5) * mm});
            skLineSegment(sketch, "E56.trimOffspring", {"start": v(441.65, 129.98) * mm, "end": v(450.32, 129.98) * mm});
            skLineSegment(sketch, "E57.trimOffspring", {"start": v(407.01, 129.98) * mm, "end": v(424.35, 129.98) * mm});
            skLineSegment(sketch, "E58.trimOffspring", {"start": v(372.37, 129.98) * mm, "end": v(389.71, 129.98) * mm});
            skLineSegment(sketch, "E59.trimOffspring", {"start": v(336.58, 129.98) * mm, "end": v(355.07, 129.98) * mm});
            skLineSegment(sketch, "E60.trimOffspring", {"start": v(303.1, 129.98) * mm, "end": v(320.43, 129.98) * mm});
            skLineSegment(sketch, "E61.trimOffspring", {"start": v(60.61, 129.98) * mm, "end": v(77.95, 129.98) * mm});
            skLineSegment(sketch, "E62", {"start": v(43.3, 130) * mm, "end": v(25.98, 130) * mm});
            skLineSegment(sketch, "E63.trimOffspring", {"start": v(199.17, 129.98) * mm, "end": v(216.51, 129.98) * mm});
            skLineSegment(sketch, "E64.trimOffspring", {"start": v(94.1, 129.98) * mm, "end": v(112.6, 129.98) * mm});
            skLineSegment(sketch, "E65.trimOffspring", {"start": v(129.9, 129.98) * mm, "end": v(147.23, 129.98) * mm});
            skLineSegment(sketch, "E66.trimOffspring", {"start": v(233.81, 129.98) * mm, "end": v(251.15, 129.98) * mm});
            skLineSegment(sketch, "E67", {"start": v(164.54, 130) * mm, "end": v(181.86, 130) * mm});
            skLineSegment(sketch, "E68.trimOffspring", {"start": v(268.45, 129.98) * mm, "end": v(285.8, 129.98) * mm});
            skLineSegment(sketch, "E69", {"start": v(21.65, 42.5) * mm, "end": v(16.84, 42.52) * mm});
            skLineSegment(sketch, "E70.bottom", {"start": v(8.34, 132.5) * mm, "end": v(469.72, 132.5) * mm});
            skLineSegment(sketch, "E70.top", {"start": v(8.34, -12.5) * mm, "end": v(469.72, -12.5) * mm});
            skLineSegment(sketch, "E70.left", {"start": v(8.34, 132.5) * mm, "end": v(8.34, -12.5) * mm});
            skLineSegment(sketch, "E70.right", {"start": v(469.72, 132.5) * mm, "end": v(469.72, -12.5) * mm});
            skSolve(sketch);
        }
        {
            var Q0;
            Q0 = qSketchRegion(id + "F0", true);
            extrude(context, id + "F1", {"entities" : qUnion([Q0]), "depth" : 25 * mm, "offsetDistance" : 25 * mm});
        }
        {
            var Q0;
            Q0=makeQuery(id+"F1.opExtrude","CAP_FACE",FACE,{"disambiguationData":[OSD([sQuery(id+"F0.wireOp",EDGE,"E2.1.0.1"),sQuery(id+"F0.wireOp",EDGE,"E2.1.0.2"),sQuery(id+"F0.wireOp",EDGE,"E2.1.0.4"),sQuery(id+"F0.wireOp",EDGE,"E2.1.0.5"),sQuery(id+"F0.wireOp",EDGE,"E2.1.0.6"),sQuery(id+"F0.wireOp",EDGE,"E2.1.0.7"),sQuery(id+"F0.wireOp",EDGE,"E2.1.0.8"),sQuery(id+"F0.wireOp",EDGE,"E2.1.0.14"),sQuery(id+"F0.wireOp",EDGE,"E2.1.0.18"),sQuery(id+"F0.wireOp",EDGE,"E2.1.0.21"),sQuery(id+"F0.wireOp",EDGE,"E2.1.0.22"),sQuery(id+"F0.wireOp",EDGE,"E2.1.0.23"),sQuery(id+"F0.wireOp",EDGE,"E2.1.1.0"),sQuery(id+"F0.wireOp",EDGE,"E2.1.1.1"),sQuery(id+"F0.wireOp",EDGE,"E2.1.1.2"),sQuery(id+"F0.wireOp",EDGE,"E2.1.1.4"),sQuery(id+"F0.wireOp",EDGE,"E2.1.1.5"),sQuery(id+"F0.wireOp",EDGE,"E2.1.1.6"),sQuery(id+"F0.wireOp",EDGE,"E2.1.1.7"),sQuery(id+"F0.wireOp",EDGE,"E2.1.1.8"),sQuery(id+"F0.wireOp",EDGE,"E2.1.1.10"),sQuery(id+"F0.wireOp",EDGE,"E2.1.1.11"),sQuery(id+"F0.wireOp",EDGE,"E2.1.1.12"),sQuery(id+"F0.wireOp",EDGE,"E2.1.1.14"),sQuery(id+"F0.wireOp",EDGE,"E2.1.1.18"),sQuery(id+"F0.wireOp",EDGE,"E2.1.1.20"),sQuery(id+"F0.wireOp",EDGE,"E2.1.1.21"),sQuery(id+"F0.wireOp",EDGE,"E2.1.1.22"),sQuery(id+"F0.wireOp",EDGE,"E2.1.1.23"),sQuery(id+"F0.wireOp",EDGE,"E2.1.1.24"),sQuery(id+"F0.wireOp",EDGE,"E2.1.2.0"),sQuery(id+"F0.wireOp",EDGE,"E2.1.2.1"),sQuery(id+"F0.wireOp",EDGE,"E2.1.2.2"),sQuery(id+"F0.wireOp",EDGE,"E2.1.2.4"),sQuery(id+"F0.wireOp",EDGE,"E2.1.2.5"),sQuery(id+"F0.wireOp",EDGE,"E2.1.2.6"),sQuery(id+"F0.wireOp",EDGE,"E2.1.2.7"),sQuery(id+"F0.wireOp",EDGE,"E2.1.2.8"),sQuery(id+"F0.wireOp",EDGE,"E2.1.2.10"),sQuery(id+"F0.wireOp",EDGE,"E2.1.2.11"),sQuery(id+"F0.wireOp",EDGE,"E2.1.2.12"),sQuery(id+"F0.wireOp",EDGE,"E2.1.2.14"),sQuery(id+"F0.wireOp",EDGE,"E2.1.2.18"),sQuery(id+"F0.wireOp",EDGE,"E2.1.2.20"),sQuery(id+"F0.wireOp",EDGE,"E2.1.2.21"),sQuery(id+"F0.wireOp",EDGE,"E2.1.2.22"),sQuery(id+"F0.wireOp",EDGE,"E2.1.2.23"),sQuery(id+"F0.wireOp",EDGE,"E2.1.2.24"),sQuery(id+"F0.wireOp",EDGE,"E2.1.3.0"),sQuery(id+"F0.wireOp",EDGE,"E2.1.3.2"),sQuery(id+"F0.wireOp",EDGE,"E2.1.3.4"),sQuery(id+"F0.wireOp",EDGE,"E2.1.3.5"),sQuery(id+"F0.wireOp",EDGE,"E2.1.3.7"),sQuery(id+"F0.wireOp",EDGE,"E2.1.3.10"),sQuery(id+"F0.wireOp",EDGE,"E2.1.3.11"),sQuery(id+"F0.wireOp",EDGE,"E2.1.3.12"),sQuery(id+"F0.wireOp",EDGE,"E2.1.3.18"),sQuery(id+"F0.wireOp",EDGE,"E2.1.3.20"),sQuery(id+"F0.wireOp",EDGE,"E2.1.3.22"),sQuery(id+"F0.wireOp",EDGE,"E2.1.3.24"),sQuery(id+"F0.wireOp",EDGE,"E2.2.0.1"),sQuery(id+"F0.wireOp",EDGE,"E2.2.0.2"),sQuery(id+"F0.wireOp",EDGE,"E2.2.0.4"),sQuery(id+"F0.wireOp",EDGE,"E2.2.0.5"),sQuery(id+"F0.wireOp",EDGE,"E2.2.0.6"),sQuery(id+"F0.wireOp",EDGE,"E2.2.0.7"),sQuery(id+"F0.wireOp",EDGE,"E2.2.0.8"),sQuery(id+"F0.wireOp",EDGE,"E2.2.0.14"),sQuery(id+"F0.wireOp",EDGE,"E2.2.0.18"),sQuery(id+"F0.wireOp",EDGE,"E2.2.0.21"),sQuery(id+"F0.wireOp",EDGE,"E2.2.0.22"),sQuery(id+"F0.wireOp",EDGE,"E2.2.0.23"),sQuery(id+"F0.wireOp",EDGE,"E2.2.1.0"),sQuery(id+"F0.wireOp",EDGE,"E2.2.1.1"),sQuery(id+"F0.wireOp",EDGE,"E2.2.1.2"),sQuery(id+"F0.wireOp",EDGE,"E2.2.1.4"),sQuery(id+"F0.wireOp",EDGE,"E2.2.1.5"),sQuery(id+"F0.wireOp",EDGE,"E2.2.1.6"),sQuery(id+"F0.wireOp",EDGE,"E2.2.1.7"),sQuery(id+"F0.wireOp",EDGE,"E2.2.1.8"),sQuery(id+"F0.wireOp",EDGE,"E2.2.1.10"),sQuery(id+"F0.wireOp",EDGE,"E2.2.1.11"),sQuery(id+"F0.wireOp",EDGE,"E2.2.1.12"),sQuery(id+"F0.wireOp",EDGE,"E2.2.1.14"),sQuery(id+"F0.wireOp",EDGE,"E2.2.1.18"),sQuery(id+"F0.wireOp",EDGE,"E2.2.1.20"),sQuery(id+"F0.wireOp",EDGE,"E2.2.1.21"),sQuery(id+"F0.wireOp",EDGE,"E2.2.1.22"),sQuery(id+"F0.wireOp",EDGE,"E2.2.1.23"),sQuery(id+"F0.wireOp",EDGE,"E2.2.1.24"),sQuery(id+"F0.wireOp",EDGE,"E2.2.2.0"),sQuery(id+"F0.wireOp",EDGE,"E2.2.2.1"),sQuery(id+"F0.wireOp",EDGE,"E2.2.2.2"),sQuery(id+"F0.wireOp",EDGE,"E2.2.2.4"),sQuery(id+"F0.wireOp",EDGE,"E2.2.2.5"),sQuery(id+"F0.wireOp",EDGE,"E2.2.2.6"),sQuery(id+"F0.wireOp",EDGE,"E2.2.2.7"),sQuery(id+"F0.wireOp",EDGE,"E2.2.2.8"),sQuery(id+"F0.wireOp",EDGE,"E2.2.2.10"),sQuery(id+"F0.wireOp",EDGE,"E2.2.2.11"),sQuery(id+"F0.wireOp",EDGE,"E2.2.2.12"),sQuery(id+"F0.wireOp",EDGE,"E2.2.2.14"),sQuery(id+"F0.wireOp",EDGE,"E2.2.2.18"),sQuery(id+"F0.wireOp",EDGE,"E2.2.2.20"),sQuery(id+"F0.wireOp",EDGE,"E2.2.2.21"),sQuery(id+"F0.wireOp",EDGE,"E2.2.2.22"),sQuery(id+"F0.wireOp",EDGE,"E2.2.2.23"),sQuery(id+"F0.wireOp",EDGE,"E2.2.2.24"),sQuery(id+"F0.wireOp",EDGE,"E2.2.3.0"),sQuery(id+"F0.wireOp",EDGE,"E2.2.3.2"),sQuery(id+"F0.wireOp",EDGE,"E2.2.3.4"),sQuery(id+"F0.wireOp",EDGE,"E2.2.3.5"),sQuery(id+"F0.wireOp",EDGE,"E2.2.3.7"),sQuery(id+"F0.wireOp",EDGE,"E2.2.3.10"),sQuery(id+"F0.wireOp",EDGE,"E2.2.3.11"),sQuery(id+"F0.wireOp",EDGE,"E2.2.3.12"),sQuery(id+"F0.wireOp",EDGE,"E2.2.3.18"),sQuery(id+"F0.wireOp",EDGE,"E2.2.3.20"),sQuery(id+"F0.wireOp",EDGE,"E2.2.3.22"),sQuery(id+"F0.wireOp",EDGE,"E2.2.3.24"),sQuery(id+"F0.wireOp",EDGE,"E2.3.0.1"),sQuery(id+"F0.wireOp",EDGE,"E2.3.0.2"),sQuery(id+"F0.wireOp",EDGE,"E2.3.0.4"),sQuery(id+"F0.wireOp",EDGE,"E2.3.0.5"),sQuery(id+"F0.wireOp",EDGE,"E2.3.0.6"),sQuery(id+"F0.wireOp",EDGE,"E2.3.0.7"),sQuery(id+"F0.wireOp",EDGE,"E2.3.0.8"),sQuery(id+"F0.wireOp",EDGE,"E2.3.0.14"),sQuery(id+"F0.wireOp",EDGE,"E2.3.0.18"),sQuery(id+"F0.wireOp",EDGE,"E2.3.0.21"),sQuery(id+"F0.wireOp",EDGE,"E2.3.0.22"),sQuery(id+"F0.wireOp",EDGE,"E2.3.0.23"),sQuery(id+"F0.wireOp",EDGE,"E2.3.1.0"),sQuery(id+"F0.wireOp",EDGE,"E2.3.1.1"),sQuery(id+"F0.wireOp",EDGE,"E2.3.1.2"),sQuery(id+"F0.wireOp",EDGE,"E2.3.1.4"),sQuery(id+"F0.wireOp",EDGE,"E2.3.1.5"),sQuery(id+"F0.wireOp",EDGE,"E2.3.1.6"),sQuery(id+"F0.wireOp",EDGE,"E2.3.1.7"),sQuery(id+"F0.wireOp",EDGE,"E2.3.1.8"),sQuery(id+"F0.wireOp",EDGE,"E2.3.1.10"),sQuery(id+"F0.wireOp",EDGE,"E2.3.1.11"),sQuery(id+"F0.wireOp",EDGE,"E2.3.1.12"),sQuery(id+"F0.wireOp",EDGE,"E2.3.1.14"),sQuery(id+"F0.wireOp",EDGE,"E2.3.1.18"),sQuery(id+"F0.wireOp",EDGE,"E2.3.1.20"),sQuery(id+"F0.wireOp",EDGE,"E2.3.1.21"),sQuery(id+"F0.wireOp",EDGE,"E2.3.1.22"),sQuery(id+"F0.wireOp",EDGE,"E2.3.1.23"),sQuery(id+"F0.wireOp",EDGE,"E2.3.1.24"),sQuery(id+"F0.wireOp",EDGE,"E2.3.2.0"),sQuery(id+"F0.wireOp",EDGE,"E2.3.2.1"),sQuery(id+"F0.wireOp",EDGE,"E2.3.2.2"),sQuery(id+"F0.wireOp",EDGE,"E2.3.2.4"),sQuery(id+"F0.wireOp",EDGE,"E2.3.2.5"),sQuery(id+"F0.wireOp",EDGE,"E2.3.2.6"),sQuery(id+"F0.wireOp",EDGE,"E2.3.2.7"),sQuery(id+"F0.wireOp",EDGE,"E2.3.2.8"),sQuery(id+"F0.wireOp",EDGE,"E2.3.2.10"),sQuery(id+"F0.wireOp",EDGE,"E2.3.2.11"),sQuery(id+"F0.wireOp",EDGE,"E2.3.2.12"),sQuery(id+"F0.wireOp",EDGE,"E2.3.2.14"),sQuery(id+"F0.wireOp",EDGE,"E2.3.2.18"),sQuery(id+"F0.wireOp",EDGE,"E2.3.2.20"),sQuery(id+"F0.wireOp",EDGE,"E2.3.2.21"),sQuery(id+"F0.wireOp",EDGE,"E2.3.2.22"),sQuery(id+"F0.wireOp",EDGE,"E2.3.2.23"),sQuery(id+"F0.wireOp",EDGE,"E2.3.2.24"),sQuery(id+"F0.wireOp",EDGE,"E2.3.3.0"),sQuery(id+"F0.wireOp",EDGE,"E2.3.3.2"),sQuery(id+"F0.wireOp",EDGE,"E2.3.3.4"),sQuery(id+"F0.wireOp",EDGE,"E2.3.3.5"),sQuery(id+"F0.wireOp",EDGE,"E2.3.3.7"),sQuery(id+"F0.wireOp",EDGE,"E2.3.3.10"),sQuery(id+"F0.wireOp",EDGE,"E2.3.3.11"),sQuery(id+"F0.wireOp",EDGE,"E2.3.3.12"),sQuery(id+"F0.wireOp",EDGE,"E2.3.3.18"),sQuery(id+"F0.wireOp",EDGE,"E2.3.3.20"),sQuery(id+"F0.wireOp",EDGE,"E2.3.3.22"),sQuery(id+"F0.wireOp",EDGE,"E2.3.3.24"),sQuery(id+"F0.wireOp",EDGE,"E2.4.0.1"),sQuery(id+"F0.wireOp",EDGE,"E2.4.0.2"),sQuery(id+"F0.wireOp",EDGE,"E2.4.0.4"),sQuery(id+"F0.wireOp",EDGE,"E2.4.0.5"),sQuery(id+"F0.wireOp",EDGE,"E2.4.0.6"),sQuery(id+"F0.wireOp",EDGE,"E2.4.0.7"),sQuery(id+"F0.wireOp",EDGE,"E2.4.0.8"),sQuery(id+"F0.wireOp",EDGE,"E2.4.0.14"),sQuery(id+"F0.wireOp",EDGE,"E2.4.0.18"),sQuery(id+"F0.wireOp",EDGE,"E2.4.0.21"),sQuery(id+"F0.wireOp",EDGE,"E2.4.0.22"),sQuery(id+"F0.wireOp",EDGE,"E2.4.0.23"),sQuery(id+"F0.wireOp",EDGE,"E2.4.1.0"),sQuery(id+"F0.wireOp",EDGE,"E2.4.1.1"),sQuery(id+"F0.wireOp",EDGE,"E2.4.1.2"),sQuery(id+"F0.wireOp",EDGE,"E2.4.1.4"),sQuery(id+"F0.wireOp",EDGE,"E2.4.1.5"),sQuery(id+"F0.wireOp",EDGE,"E2.4.1.6"),sQuery(id+"F0.wireOp",EDGE,"E2.4.1.7"),sQuery(id+"F0.wireOp",EDGE,"E2.4.1.8"),sQuery(id+"F0.wireOp",EDGE,"E2.4.1.10"),sQuery(id+"F0.wireOp",EDGE,"E2.4.1.11"),sQuery(id+"F0.wireOp",EDGE,"E2.4.1.12"),sQuery(id+"F0.wireOp",EDGE,"E2.4.1.14"),sQuery(id+"F0.wireOp",EDGE,"E2.4.1.18"),sQuery(id+"F0.wireOp",EDGE,"E2.4.1.20"),sQuery(id+"F0.wireOp",EDGE,"E2.4.1.21"),sQuery(id+"F0.wireOp",EDGE,"E2.4.1.22"),sQuery(id+"F0.wireOp",EDGE,"E2.4.1.23"),sQuery(id+"F0.wireOp",EDGE,"E2.4.1.24"),sQuery(id+"F0.wireOp",EDGE,"E2.4.2.0"),sQuery(id+"F0.wireOp",EDGE,"E2.4.2.1"),sQuery(id+"F0.wireOp",EDGE,"E2.4.2.2"),sQuery(id+"F0.wireOp",EDGE,"E2.4.2.4"),sQuery(id+"F0.wireOp",EDGE,"E2.4.2.5"),sQuery(id+"F0.wireOp",EDGE,"E2.4.2.6"),sQuery(id+"F0.wireOp",EDGE,"E2.4.2.7"),sQuery(id+"F0.wireOp",EDGE,"E2.4.2.8"),sQuery(id+"F0.wireOp",EDGE,"E2.4.2.10"),sQuery(id+"F0.wireOp",EDGE,"E2.4.2.11"),sQuery(id+"F0.wireOp",EDGE,"E2.4.2.12"),sQuery(id+"F0.wireOp",EDGE,"E2.4.2.14"),sQuery(id+"F0.wireOp",EDGE,"E2.4.2.18"),sQuery(id+"F0.wireOp",EDGE,"E2.4.2.20"),sQuery(id+"F0.wireOp",EDGE,"E2.4.2.21"),sQuery(id+"F0.wireOp",EDGE,"E2.4.2.22"),sQuery(id+"F0.wireOp",EDGE,"E2.4.2.23"),sQuery(id+"F0.wireOp",EDGE,"E2.4.2.24"),sQuery(id+"F0.wireOp",EDGE,"E2.4.3.0"),sQuery(id+"F0.wireOp",EDGE,"E2.4.3.2"),sQuery(id+"F0.wireOp",EDGE,"E2.4.3.4"),sQuery(id+"F0.wireOp",EDGE,"E2.4.3.5"),sQuery(id+"F0.wireOp",EDGE,"E2.4.3.7"),sQuery(id+"F0.wireOp",EDGE,"E2.4.3.10"),sQuery(id+"F0.wireOp",EDGE,"E2.4.3.11"),sQuery(id+"F0.wireOp",EDGE,"E2.4.3.12"),sQuery(id+"F0.wireOp",EDGE,"E2.4.3.18"),sQuery(id+"F0.wireOp",EDGE,"E2.4.3.20"),sQuery(id+"F0.wireOp",EDGE,"E2.4.3.22"),sQuery(id+"F0.wireOp",EDGE,"E2.4.3.24"),sQuery(id+"F0.wireOp",EDGE,"E2.5.0.1"),sQuery(id+"F0.wireOp",EDGE,"E2.5.0.2"),sQuery(id+"F0.wireOp",EDGE,"E2.5.0.4"),sQuery(id+"F0.wireOp",EDGE,"E2.5.0.5"),sQuery(id+"F0.wireOp",EDGE,"E2.5.0.6"),sQuery(id+"F0.wireOp",EDGE,"E2.5.0.7"),sQuery(id+"F0.wireOp",EDGE,"E2.5.0.8"),sQuery(id+"F0.wireOp",EDGE,"E2.5.0.14"),sQuery(id+"F0.wireOp",EDGE,"E2.5.0.18"),sQuery(id+"F0.wireOp",EDGE,"E2.5.0.21"),sQuery(id+"F0.wireOp",EDGE,"E2.5.0.22"),sQuery(id+"F0.wireOp",EDGE,"E2.5.0.23"),sQuery(id+"F0.wireOp",EDGE,"E2.5.1.0"),sQuery(id+"F0.wireOp",EDGE,"E2.5.1.1"),sQuery(id+"F0.wireOp",EDGE,"E2.5.1.2"),sQuery(id+"F0.wireOp",EDGE,"E2.5.1.4"),sQuery(id+"F0.wireOp",EDGE,"E2.5.1.5"),sQuery(id+"F0.wireOp",EDGE,"E2.5.1.6"),sQuery(id+"F0.wireOp",EDGE,"E2.5.1.7"),sQuery(id+"F0.wireOp",EDGE,"E2.5.1.8"),sQuery(id+"F0.wireOp",EDGE,"E2.5.1.10"),sQuery(id+"F0.wireOp",EDGE,"E2.5.1.11"),sQuery(id+"F0.wireOp",EDGE,"E2.5.1.12"),sQuery(id+"F0.wireOp",EDGE,"E2.5.1.14"),sQuery(id+"F0.wireOp",EDGE,"E2.5.1.18"),sQuery(id+"F0.wireOp",EDGE,"E2.5.1.20"),sQuery(id+"F0.wireOp",EDGE,"E2.5.1.21"),sQuery(id+"F0.wireOp",EDGE,"E2.5.1.22"),sQuery(id+"F0.wireOp",EDGE,"E2.5.1.23"),sQuery(id+"F0.wireOp",EDGE,"E2.5.1.24"),sQuery(id+"F0.wireOp",EDGE,"E2.5.2.0"),sQuery(id+"F0.wireOp",EDGE,"E2.5.2.1"),sQuery(id+"F0.wireOp",EDGE,"E2.5.2.2"),sQuery(id+"F0.wireOp",EDGE,"E2.5.2.4"),sQuery(id+"F0.wireOp",EDGE,"E2.5.2.5"),sQuery(id+"F0.wireOp",EDGE,"E2.5.2.6"),sQuery(id+"F0.wireOp",EDGE,"E2.5.2.7"),sQuery(id+"F0.wireOp",EDGE,"E2.5.2.8"),sQuery(id+"F0.wireOp",EDGE,"E2.5.2.10"),sQuery(id+"F0.wireOp",EDGE,"E2.5.2.11"),sQuery(id+"F0.wireOp",EDGE,"E2.5.2.12"),sQuery(id+"F0.wireOp",EDGE,"E2.5.2.14"),sQuery(id+"F0.wireOp",EDGE,"E2.5.2.18"),sQuery(id+"F0.wireOp",EDGE,"E2.5.2.20"),sQuery(id+"F0.wireOp",EDGE,"E2.5.2.21"),sQuery(id+"F0.wireOp",EDGE,"E2.5.2.22"),sQuery(id+"F0.wireOp",EDGE,"E2.5.2.23"),sQuery(id+"F0.wireOp",EDGE,"E2.5.2.24"),sQuery(id+"F0.wireOp",EDGE,"E2.5.3.0"),sQuery(id+"F0.wireOp",EDGE,"E2.5.3.2"),sQuery(id+"F0.wireOp",EDGE,"E2.5.3.4"),sQuery(id+"F0.wireOp",EDGE,"E2.5.3.5"),sQuery(id+"F0.wireOp",EDGE,"E2.5.3.7"),sQuery(id+"F0.wireOp",EDGE,"E2.5.3.10"),sQuery(id+"F0.wireOp",EDGE,"E2.5.3.11"),sQuery(id+"F0.wireOp",EDGE,"E2.5.3.12"),sQuery(id+"F0.wireOp",EDGE,"E2.5.3.18"),sQuery(id+"F0.wireOp",EDGE,"E2.5.3.20"),sQuery(id+"F0.wireOp",EDGE,"E2.5.3.22"),sQuery(id+"F0.wireOp",EDGE,"E2.5.3.24"),sQuery(id+"F0.wireOp",EDGE,"E2.6.0.1"),sQuery(id+"F0.wireOp",EDGE,"E2.6.0.2"),sQuery(id+"F0.wireOp",EDGE,"E2.6.0.4"),sQuery(id+"F0.wireOp",EDGE,"E2.6.0.5"),sQuery(id+"F0.wireOp",EDGE,"E2.6.0.6"),sQuery(id+"F0.wireOp",EDGE,"E2.6.0.7"),sQuery(id+"F0.wireOp",EDGE,"E2.6.0.8"),sQuery(id+"F0.wireOp",EDGE,"E2.6.0.14"),sQuery(id+"F0.wireOp",EDGE,"E2.6.0.18"),sQuery(id+"F0.wireOp",EDGE,"E2.6.0.21"),sQuery(id+"F0.wireOp",EDGE,"E2.6.0.22"),sQuery(id+"F0.wireOp",EDGE,"E2.6.0.23"),sQuery(id+"F0.wireOp",EDGE,"E2.6.1.0"),sQuery(id+"F0.wireOp",EDGE,"E2.6.1.1"),sQuery(id+"F0.wireOp",EDGE,"E2.6.1.2"),sQuery(id+"F0.wireOp",EDGE,"E2.6.1.4"),sQuery(id+"F0.wireOp",EDGE,"E2.6.1.5"),sQuery(id+"F0.wireOp",EDGE,"E2.6.1.6"),sQuery(id+"F0.wireOp",EDGE,"E2.6.1.7"),sQuery(id+"F0.wireOp",EDGE,"E2.6.1.8"),sQuery(id+"F0.wireOp",EDGE,"E2.6.1.10"),sQuery(id+"F0.wireOp",EDGE,"E2.6.1.11"),sQuery(id+"F0.wireOp",EDGE,"E2.6.1.12"),sQuery(id+"F0.wireOp",EDGE,"E2.6.1.14"),sQuery(id+"F0.wireOp",EDGE,"E2.6.1.18"),sQuery(id+"F0.wireOp",EDGE,"E2.6.1.20"),sQuery(id+"F0.wireOp",EDGE,"E2.6.1.21"),sQuery(id+"F0.wireOp",EDGE,"E2.6.1.22"),sQuery(id+"F0.wireOp",EDGE,"E2.6.1.23"),sQuery(id+"F0.wireOp",EDGE,"E2.6.1.24"),sQuery(id+"F0.wireOp",EDGE,"E2.6.2.0"),sQuery(id+"F0.wireOp",EDGE,"E2.6.2.1"),sQuery(id+"F0.wireOp",EDGE,"E2.6.2.2"),sQuery(id+"F0.wireOp",EDGE,"E2.6.2.4"),sQuery(id+"F0.wireOp",EDGE,"E2.6.2.5"),sQuery(id+"F0.wireOp",EDGE,"E2.6.2.6"),sQuery(id+"F0.wireOp",EDGE,"E2.6.2.7"),sQuery(id+"F0.wireOp",EDGE,"E2.6.2.8"),sQuery(id+"F0.wireOp",EDGE,"E2.6.2.10"),sQuery(id+"F0.wireOp",EDGE,"E2.6.2.11"),sQuery(id+"F0.wireOp",EDGE,"E2.6.2.12"),sQuery(id+"F0.wireOp",EDGE,"E2.6.2.14"),sQuery(id+"F0.wireOp",EDGE,"E2.6.2.18"),sQuery(id+"F0.wireOp",EDGE,"E2.6.2.20"),sQuery(id+"F0.wireOp",EDGE,"E2.6.2.21"),sQuery(id+"F0.wireOp",EDGE,"E2.6.2.22"),sQuery(id+"F0.wireOp",EDGE,"E2.6.2.23"),sQuery(id+"F0.wireOp",EDGE,"E2.6.2.24"),sQuery(id+"F0.wireOp",EDGE,"E2.6.3.0"),sQuery(id+"F0.wireOp",EDGE,"E2.6.3.2"),sQuery(id+"F0.wireOp",EDGE,"E2.6.3.4"),sQuery(id+"F0.wireOp",EDGE,"E2.6.3.5"),sQuery(id+"F0.wireOp",EDGE,"E2.6.3.7"),sQuery(id+"F0.wireOp",EDGE,"E2.6.3.10"),sQuery(id+"F0.wireOp",EDGE,"E2.6.3.11"),sQuery(id+"F0.wireOp",EDGE,"E2.6.3.12"),sQuery(id+"F0.wireOp",EDGE,"E2.6.3.18"),sQuery(id+"F0.wireOp",EDGE,"E2.6.3.20"),sQuery(id+"F0.wireOp",EDGE,"E2.6.3.22"),sQuery(id+"F0.wireOp",EDGE,"E2.6.3.24"),sQuery(id+"F0.wireOp",EDGE,"E2.7.0.1"),sQuery(id+"F0.wireOp",EDGE,"E2.7.0.2"),sQuery(id+"F0.wireOp",EDGE,"E2.7.0.4"),sQuery(id+"F0.wireOp",EDGE,"E2.7.0.5"),sQuery(id+"F0.wireOp",EDGE,"E2.7.0.6"),sQuery(id+"F0.wireOp",EDGE,"E2.7.0.7"),sQuery(id+"F0.wireOp",EDGE,"E2.7.0.8"),sQuery(id+"F0.wireOp",EDGE,"E2.7.0.14"),sQuery(id+"F0.wireOp",EDGE,"E2.7.0.18"),sQuery(id+"F0.wireOp",EDGE,"E2.7.0.21"),sQuery(id+"F0.wireOp",EDGE,"E2.7.0.22"),sQuery(id+"F0.wireOp",EDGE,"E2.7.0.23"),sQuery(id+"F0.wireOp",EDGE,"E2.7.1.0"),sQuery(id+"F0.wireOp",EDGE,"E2.7.1.1"),sQuery(id+"F0.wireOp",EDGE,"E2.7.1.2"),sQuery(id+"F0.wireOp",EDGE,"E2.7.1.4"),sQuery(id+"F0.wireOp",EDGE,"E2.7.1.5"),sQuery(id+"F0.wireOp",EDGE,"E2.7.1.6"),sQuery(id+"F0.wireOp",EDGE,"E2.7.1.7"),sQuery(id+"F0.wireOp",EDGE,"E2.7.1.8"),sQuery(id+"F0.wireOp",EDGE,"E2.7.1.10"),sQuery(id+"F0.wireOp",EDGE,"E2.7.1.11"),sQuery(id+"F0.wireOp",EDGE,"E2.7.1.12"),sQuery(id+"F0.wireOp",EDGE,"E2.7.1.14"),sQuery(id+"F0.wireOp",EDGE,"E2.7.1.18"),sQuery(id+"F0.wireOp",EDGE,"E2.7.1.20"),sQuery(id+"F0.wireOp",EDGE,"E2.7.1.21"),sQuery(id+"F0.wireOp",EDGE,"E2.7.1.22"),sQuery(id+"F0.wireOp",EDGE,"E2.7.1.23"),sQuery(id+"F0.wireOp",EDGE,"E2.7.1.24"),sQuery(id+"F0.wireOp",EDGE,"E2.7.2.0"),sQuery(id+"F0.wireOp",EDGE,"E2.7.2.1"),sQuery(id+"F0.wireOp",EDGE,"E2.7.2.2"),sQuery(id+"F0.wireOp",EDGE,"E2.7.2.4"),sQuery(id+"F0.wireOp",EDGE,"E2.7.2.5"),sQuery(id+"F0.wireOp",EDGE,"E2.7.2.6"),sQuery(id+"F0.wireOp",EDGE,"E2.7.2.7"),sQuery(id+"F0.wireOp",EDGE,"E2.7.2.8"),sQuery(id+"F0.wireOp",EDGE,"E2.7.2.10"),sQuery(id+"F0.wireOp",EDGE,"E2.7.2.11"),sQuery(id+"F0.wireOp",EDGE,"E2.7.2.12"),sQuery(id+"F0.wireOp",EDGE,"E2.7.2.14"),sQuery(id+"F0.wireOp",EDGE,"E2.7.2.18"),sQuery(id+"F0.wireOp",EDGE,"E2.7.2.20"),sQuery(id+"F0.wireOp",EDGE,"E2.7.2.21"),sQuery(id+"F0.wireOp",EDGE,"E2.7.2.22"),sQuery(id+"F0.wireOp",EDGE,"E2.7.2.23"),sQuery(id+"F0.wireOp",EDGE,"E2.7.2.24"),sQuery(id+"F0.wireOp",EDGE,"E2.7.3.0"),sQuery(id+"F0.wireOp",EDGE,"E2.7.3.2"),sQuery(id+"F0.wireOp",EDGE,"E2.7.3.4"),sQuery(id+"F0.wireOp",EDGE,"E2.7.3.5"),sQuery(id+"F0.wireOp",EDGE,"E2.7.3.7"),sQuery(id+"F0.wireOp",EDGE,"E2.7.3.10"),sQuery(id+"F0.wireOp",EDGE,"E2.7.3.11"),sQuery(id+"F0.wireOp",EDGE,"E2.7.3.12"),sQuery(id+"F0.wireOp",EDGE,"E2.7.3.18"),sQuery(id+"F0.wireOp",EDGE,"E2.7.3.20"),sQuery(id+"F0.wireOp",EDGE,"E2.7.3.22"),sQuery(id+"F0.wireOp",EDGE,"E2.7.3.24"),sQuery(id+"F0.wireOp",EDGE,"E2.8.0.1"),sQuery(id+"F0.wireOp",EDGE,"E2.8.0.2"),sQuery(id+"F0.wireOp",EDGE,"E2.8.0.4"),sQuery(id+"F0.wireOp",EDGE,"E2.8.0.5"),sQuery(id+"F0.wireOp",EDGE,"E2.8.0.6"),sQuery(id+"F0.wireOp",EDGE,"E2.8.0.7"),sQuery(id+"F0.wireOp",EDGE,"E2.8.0.8"),sQuery(id+"F0.wireOp",EDGE,"E2.8.0.14"),sQuery(id+"F0.wireOp",EDGE,"E2.8.0.18"),sQuery(id+"F0.wireOp",EDGE,"E2.8.0.21"),sQuery(id+"F0.wireOp",EDGE,"E2.8.0.22"),sQuery(id+"F0.wireOp",EDGE,"E2.8.0.23"),sQuery(id+"F0.wireOp",EDGE,"E2.8.1.0"),sQuery(id+"F0.wireOp",EDGE,"E2.8.1.1"),sQuery(id+"F0.wireOp",EDGE,"E2.8.1.2"),sQuery(id+"F0.wireOp",EDGE,"E2.8.1.4"),sQuery(id+"F0.wireOp",EDGE,"E2.8.1.5"),sQuery(id+"F0.wireOp",EDGE,"E2.8.1.6"),sQuery(id+"F0.wireOp",EDGE,"E2.8.1.7"),sQuery(id+"F0.wireOp",EDGE,"E2.8.1.8"),sQuery(id+"F0.wireOp",EDGE,"E2.8.1.10"),sQuery(id+"F0.wireOp",EDGE,"E2.8.1.11"),sQuery(id+"F0.wireOp",EDGE,"E2.8.1.12"),sQuery(id+"F0.wireOp",EDGE,"E2.8.1.14"),sQuery(id+"F0.wireOp",EDGE,"E2.8.1.18"),sQuery(id+"F0.wireOp",EDGE,"E2.8.1.20"),sQuery(id+"F0.wireOp",EDGE,"E2.8.1.21"),sQuery(id+"F0.wireOp",EDGE,"E2.8.1.22"),sQuery(id+"F0.wireOp",EDGE,"E2.8.1.23"),sQuery(id+"F0.wireOp",EDGE,"E2.8.1.24"),sQuery(id+"F0.wireOp",EDGE,"E2.8.2.0"),sQuery(id+"F0.wireOp",EDGE,"E2.8.2.1"),sQuery(id+"F0.wireOp",EDGE,"E2.8.2.2"),sQuery(id+"F0.wireOp",EDGE,"E2.8.2.4"),sQuery(id+"F0.wireOp",EDGE,"E2.8.2.5"),sQuery(id+"F0.wireOp",EDGE,"E2.8.2.6"),sQuery(id+"F0.wireOp",EDGE,"E2.8.2.7"),sQuery(id+"F0.wireOp",EDGE,"E2.8.2.8"),sQuery(id+"F0.wireOp",EDGE,"E2.8.2.10"),sQuery(id+"F0.wireOp",EDGE,"E2.8.2.11"),sQuery(id+"F0.wireOp",EDGE,"E2.8.2.12"),sQuery(id+"F0.wireOp",EDGE,"E2.8.2.14"),sQuery(id+"F0.wireOp",EDGE,"E2.8.2.18"),sQuery(id+"F0.wireOp",EDGE,"E2.8.2.20"),sQuery(id+"F0.wireOp",EDGE,"E2.8.2.21"),sQuery(id+"F0.wireOp",EDGE,"E2.8.2.22"),sQuery(id+"F0.wireOp",EDGE,"E2.8.2.23"),sQuery(id+"F0.wireOp",EDGE,"E2.8.2.24"),sQuery(id+"F0.wireOp",EDGE,"E2.8.3.0"),sQuery(id+"F0.wireOp",EDGE,"E2.8.3.2"),sQuery(id+"F0.wireOp",EDGE,"E2.8.3.4"),sQuery(id+"F0.wireOp",EDGE,"E2.8.3.5"),sQuery(id+"F0.wireOp",EDGE,"E2.8.3.7"),sQuery(id+"F0.wireOp",EDGE,"E2.8.3.10"),sQuery(id+"F0.wireOp",EDGE,"E2.8.3.11"),sQuery(id+"F0.wireOp",EDGE,"E2.8.3.12"),sQuery(id+"F0.wireOp",EDGE,"E2.8.3.18"),sQuery(id+"F0.wireOp",EDGE,"E2.8.3.20"),sQuery(id+"F0.wireOp",EDGE,"E2.8.3.22"),sQuery(id+"F0.wireOp",EDGE,"E2.8.3.24"),sQuery(id+"F0.wireOp",EDGE,"E2.9.0.1"),sQuery(id+"F0.wireOp",EDGE,"E2.9.0.2"),sQuery(id+"F0.wireOp",EDGE,"E2.9.0.4"),sQuery(id+"F0.wireOp",EDGE,"E2.9.0.5"),sQuery(id+"F0.wireOp",EDGE,"E2.9.0.6"),sQuery(id+"F0.wireOp",EDGE,"E2.9.0.7"),sQuery(id+"F0.wireOp",EDGE,"E2.9.0.8"),sQuery(id+"F0.wireOp",EDGE,"E2.9.0.14"),sQuery(id+"F0.wireOp",EDGE,"E2.9.0.18"),sQuery(id+"F0.wireOp",EDGE,"E2.9.0.21"),sQuery(id+"F0.wireOp",EDGE,"E2.9.0.22"),sQuery(id+"F0.wireOp",EDGE,"E2.9.0.23"),sQuery(id+"F0.wireOp",EDGE,"E2.9.1.0"),sQuery(id+"F0.wireOp",EDGE,"E2.9.1.1"),sQuery(id+"F0.wireOp",EDGE,"E2.9.1.2"),sQuery(id+"F0.wireOp",EDGE,"E2.9.1.4"),sQuery(id+"F0.wireOp",EDGE,"E2.9.1.5"),sQuery(id+"F0.wireOp",EDGE,"E2.9.1.6"),sQuery(id+"F0.wireOp",EDGE,"E2.9.1.7"),sQuery(id+"F0.wireOp",EDGE,"E2.9.1.8"),sQuery(id+"F0.wireOp",EDGE,"E2.9.1.10"),sQuery(id+"F0.wireOp",EDGE,"E2.9.1.11"),sQuery(id+"F0.wireOp",EDGE,"E2.9.1.12"),sQuery(id+"F0.wireOp",EDGE,"E2.9.1.14"),sQuery(id+"F0.wireOp",EDGE,"E2.9.1.18"),sQuery(id+"F0.wireOp",EDGE,"E2.9.1.20"),sQuery(id+"F0.wireOp",EDGE,"E2.9.1.21"),sQuery(id+"F0.wireOp",EDGE,"E2.9.1.22"),sQuery(id+"F0.wireOp",EDGE,"E2.9.1.23"),sQuery(id+"F0.wireOp",EDGE,"E2.9.1.24"),sQuery(id+"F0.wireOp",EDGE,"E2.9.2.0"),sQuery(id+"F0.wireOp",EDGE,"E2.9.2.1"),sQuery(id+"F0.wireOp",EDGE,"E2.9.2.2"),sQuery(id+"F0.wireOp",EDGE,"E2.9.2.4"),sQuery(id+"F0.wireOp",EDGE,"E2.9.2.5"),sQuery(id+"F0.wireOp",EDGE,"E2.9.2.6"),sQuery(id+"F0.wireOp",EDGE,"E2.9.2.7"),sQuery(id+"F0.wireOp",EDGE,"E2.9.2.8"),sQuery(id+"F0.wireOp",EDGE,"E2.9.2.10"),sQuery(id+"F0.wireOp",EDGE,"E2.9.2.11"),sQuery(id+"F0.wireOp",EDGE,"E2.9.2.12"),sQuery(id+"F0.wireOp",EDGE,"E2.9.2.14"),sQuery(id+"F0.wireOp",EDGE,"E2.9.2.18"),sQuery(id+"F0.wireOp",EDGE,"E2.9.2.20"),sQuery(id+"F0.wireOp",EDGE,"E2.9.2.21"),sQuery(id+"F0.wireOp",EDGE,"E2.9.2.22"),sQuery(id+"F0.wireOp",EDGE,"E2.9.2.23"),sQuery(id+"F0.wireOp",EDGE,"E2.9.2.24"),sQuery(id+"F0.wireOp",EDGE,"E2.9.3.0"),sQuery(id+"F0.wireOp",EDGE,"E2.9.3.2"),sQuery(id+"F0.wireOp",EDGE,"E2.9.3.4"),sQuery(id+"F0.wireOp",EDGE,"E2.9.3.5"),sQuery(id+"F0.wireOp",EDGE,"E2.9.3.7"),sQuery(id+"F0.wireOp",EDGE,"E2.9.3.10"),sQuery(id+"F0.wireOp",EDGE,"E2.9.3.11"),sQuery(id+"F0.wireOp",EDGE,"E2.9.3.12"),sQuery(id+"F0.wireOp",EDGE,"E2.9.3.18"),sQuery(id+"F0.wireOp",EDGE,"E2.9.3.20"),sQuery(id+"F0.wireOp",EDGE,"E2.9.3.22"),sQuery(id+"F0.wireOp",EDGE,"E2.9.3.24"),sQuery(id+"F0.wireOp",EDGE,"E2.10.0.1"),sQuery(id+"F0.wireOp",EDGE,"E2.10.0.2"),sQuery(id+"F0.wireOp",EDGE,"E2.10.0.4"),sQuery(id+"F0.wireOp",EDGE,"E2.10.0.5"),sQuery(id+"F0.wireOp",EDGE,"E2.10.0.6"),sQuery(id+"F0.wireOp",EDGE,"E2.10.0.7"),sQuery(id+"F0.wireOp",EDGE,"E2.10.0.8"),sQuery(id+"F0.wireOp",EDGE,"E2.10.0.14"),sQuery(id+"F0.wireOp",EDGE,"E2.10.0.18"),sQuery(id+"F0.wireOp",EDGE,"E2.10.0.21"),sQuery(id+"F0.wireOp",EDGE,"E2.10.0.22"),sQuery(id+"F0.wireOp",EDGE,"E2.10.0.23"),sQuery(id+"F0.wireOp",EDGE,"E2.10.1.0"),sQuery(id+"F0.wireOp",EDGE,"E2.10.1.1"),sQuery(id+"F0.wireOp",EDGE,"E2.10.1.2"),sQuery(id+"F0.wireOp",EDGE,"E2.10.1.4"),sQuery(id+"F0.wireOp",EDGE,"E2.10.1.5"),sQuery(id+"F0.wireOp",EDGE,"E2.10.1.6"),sQuery(id+"F0.wireOp",EDGE,"E2.10.1.7"),sQuery(id+"F0.wireOp",EDGE,"E2.10.1.8"),sQuery(id+"F0.wireOp",EDGE,"E2.10.1.10"),sQuery(id+"F0.wireOp",EDGE,"E2.10.1.11"),sQuery(id+"F0.wireOp",EDGE,"E2.10.1.12"),sQuery(id+"F0.wireOp",EDGE,"E2.10.1.14"),sQuery(id+"F0.wireOp",EDGE,"E2.10.1.18"),sQuery(id+"F0.wireOp",EDGE,"E2.10.1.20"),sQuery(id+"F0.wireOp",EDGE,"E2.10.1.21"),sQuery(id+"F0.wireOp",EDGE,"E2.10.1.22"),sQuery(id+"F0.wireOp",EDGE,"E2.10.1.23"),sQuery(id+"F0.wireOp",EDGE,"E2.10.1.24"),sQuery(id+"F0.wireOp",EDGE,"E2.10.2.0"),sQuery(id+"F0.wireOp",EDGE,"E2.10.2.1"),sQuery(id+"F0.wireOp",EDGE,"E2.10.2.2"),sQuery(id+"F0.wireOp",EDGE,"E2.10.2.4"),sQuery(id+"F0.wireOp",EDGE,"E2.10.2.5"),sQuery(id+"F0.wireOp",EDGE,"E2.10.2.6"),sQuery(id+"F0.wireOp",EDGE,"E2.10.2.7"),sQuery(id+"F0.wireOp",EDGE,"E2.10.2.8"),sQuery(id+"F0.wireOp",EDGE,"E2.10.2.10"),sQuery(id+"F0.wireOp",EDGE,"E2.10.2.11"),sQuery(id+"F0.wireOp",EDGE,"E2.10.2.12"),sQuery(id+"F0.wireOp",EDGE,"E2.10.2.14"),sQuery(id+"F0.wireOp",EDGE,"E2.10.2.18"),sQuery(id+"F0.wireOp",EDGE,"E2.10.2.20"),sQuery(id+"F0.wireOp",EDGE,"E2.10.2.21"),sQuery(id+"F0.wireOp",EDGE,"E2.10.2.22"),sQuery(id+"F0.wireOp",EDGE,"E2.10.2.23"),sQuery(id+"F0.wireOp",EDGE,"E2.10.2.24"),sQuery(id+"F0.wireOp",EDGE,"E2.10.3.0"),sQuery(id+"F0.wireOp",EDGE,"E2.10.3.2"),sQuery(id+"F0.wireOp",EDGE,"E2.10.3.4"),sQuery(id+"F0.wireOp",EDGE,"E2.10.3.5"),sQuery(id+"F0.wireOp",EDGE,"E2.10.3.7"),sQuery(id+"F0.wireOp",EDGE,"E2.10.3.10"),sQuery(id+"F0.wireOp",EDGE,"E2.10.3.11"),sQuery(id+"F0.wireOp",EDGE,"E2.10.3.12"),sQuery(id+"F0.wireOp",EDGE,"E2.10.3.18"),sQuery(id+"F0.wireOp",EDGE,"E2.10.3.20"),sQuery(id+"F0.wireOp",EDGE,"E2.10.3.22"),sQuery(id+"F0.wireOp",EDGE,"E2.10.3.24"),sQuery(id+"F0.wireOp",EDGE,"E2.11.0.1"),sQuery(id+"F0.wireOp",EDGE,"E2.11.0.2"),sQuery(id+"F0.wireOp",EDGE,"E2.11.0.4"),sQuery(id+"F0.wireOp",EDGE,"E2.11.0.5"),sQuery(id+"F0.wireOp",EDGE,"E2.11.0.6"),sQuery(id+"F0.wireOp",EDGE,"E2.11.0.7"),sQuery(id+"F0.wireOp",EDGE,"E2.11.0.8"),sQuery(id+"F0.wireOp",EDGE,"E2.11.0.14"),sQuery(id+"F0.wireOp",EDGE,"E2.11.0.18"),sQuery(id+"F0.wireOp",EDGE,"E2.11.0.21"),sQuery(id+"F0.wireOp",EDGE,"E2.11.0.22"),sQuery(id+"F0.wireOp",EDGE,"E2.11.0.23"),sQuery(id+"F0.wireOp",EDGE,"E2.11.1.0"),sQuery(id+"F0.wireOp",EDGE,"E2.11.1.1"),sQuery(id+"F0.wireOp",EDGE,"E2.11.1.2"),sQuery(id+"F0.wireOp",EDGE,"E2.11.1.4"),sQuery(id+"F0.wireOp",EDGE,"E2.11.1.5"),sQuery(id+"F0.wireOp",EDGE,"E2.11.1.6"),sQuery(id+"F0.wireOp",EDGE,"E2.11.1.7"),sQuery(id+"F0.wireOp",EDGE,"E2.11.1.8"),sQuery(id+"F0.wireOp",EDGE,"E2.11.1.10"),sQuery(id+"F0.wireOp",EDGE,"E2.11.1.11"),sQuery(id+"F0.wireOp",EDGE,"E2.11.1.12"),sQuery(id+"F0.wireOp",EDGE,"E2.11.1.14"),sQuery(id+"F0.wireOp",EDGE,"E2.11.1.18"),sQuery(id+"F0.wireOp",EDGE,"E2.11.1.20"),sQuery(id+"F0.wireOp",EDGE,"E2.11.1.21"),sQuery(id+"F0.wireOp",EDGE,"E2.11.1.22"),sQuery(id+"F0.wireOp",EDGE,"E2.11.1.23"),sQuery(id+"F0.wireOp",EDGE,"E2.11.1.24"),sQuery(id+"F0.wireOp",EDGE,"E2.11.2.0"),sQuery(id+"F0.wireOp",EDGE,"E2.11.2.1"),sQuery(id+"F0.wireOp",EDGE,"E2.11.2.2"),sQuery(id+"F0.wireOp",EDGE,"E2.11.2.4"),sQuery(id+"F0.wireOp",EDGE,"E2.11.2.5"),sQuery(id+"F0.wireOp",EDGE,"E2.11.2.6"),sQuery(id+"F0.wireOp",EDGE,"E2.11.2.7"),sQuery(id+"F0.wireOp",EDGE,"E2.11.2.8"),sQuery(id+"F0.wireOp",EDGE,"E2.11.2.10"),sQuery(id+"F0.wireOp",EDGE,"E2.11.2.11"),sQuery(id+"F0.wireOp",EDGE,"E2.11.2.12"),sQuery(id+"F0.wireOp",EDGE,"E2.11.2.14"),sQuery(id+"F0.wireOp",EDGE,"E2.11.2.18"),sQuery(id+"F0.wireOp",EDGE,"E2.11.2.20"),sQuery(id+"F0.wireOp",EDGE,"E2.11.2.21"),sQuery(id+"F0.wireOp",EDGE,"E2.11.2.22"),sQuery(id+"F0.wireOp",EDGE,"E2.11.2.23"),sQuery(id+"F0.wireOp",EDGE,"E2.11.2.24"),sQuery(id+"F0.wireOp",EDGE,"E2.11.3.0"),sQuery(id+"F0.wireOp",EDGE,"E2.11.3.2"),sQuery(id+"F0.wireOp",EDGE,"E2.11.3.4"),sQuery(id+"F0.wireOp",EDGE,"E2.11.3.5"),sQuery(id+"F0.wireOp",EDGE,"E2.11.3.7"),sQuery(id+"F0.wireOp",EDGE,"E2.11.3.10"),sQuery(id+"F0.wireOp",EDGE,"E2.11.3.11"),sQuery(id+"F0.wireOp",EDGE,"E2.11.3.12"),sQuery(id+"F0.wireOp",EDGE,"E2.11.3.18"),sQuery(id+"F0.wireOp",EDGE,"E2.11.3.20"),sQuery(id+"F0.wireOp",EDGE,"E2.11.3.22"),sQuery(id+"F0.wireOp",EDGE,"E2.11.3.24"),sQuery(id+"F0.wireOp",EDGE,"E6.0"),sQuery(id+"F0.wireOp",EDGE,"E6.1"),sQuery(id+"F0.wireOp",EDGE,"E6.2"),sQuery(id+"F0.wireOp",EDGE,"E6.3"),sQuery(id+"F0.wireOp",EDGE,"E6.4"),sQuery(id+"F0.wireOp",EDGE,"E6.5"),sQuery(id+"F0.wireOp",EDGE,"E10.0.1.0"),sQuery(id+"F0.wireOp",EDGE,"E10.0.1.1"),sQuery(id+"F0.wireOp",EDGE,"E10.0.1.2"),sQuery(id+"F0.wireOp",EDGE,"E10.0.1.3"),sQuery(id+"F0.wireOp",EDGE,"E10.0.1.4"),sQuery(id+"F0.wireOp",EDGE,"E10.0.1.5"),sQuery(id+"F0.wireOp",EDGE,"E10.0.2.0"),sQuery(id+"F0.wireOp",EDGE,"E10.0.2.1"),sQuery(id+"F0.wireOp",EDGE,"E10.0.2.2"),sQuery(id+"F0.wireOp",EDGE,"E10.0.2.3"),sQuery(id+"F0.wireOp",EDGE,"E10.0.2.4"),sQuery(id+"F0.wireOp",EDGE,"E10.0.2.5"),sQuery(id+"F0.wireOp",EDGE,"E10.1.0.0"),sQuery(id+"F0.wireOp",EDGE,"E10.1.0.1"),sQuery(id+"F0.wireOp",EDGE,"E10.1.0.2"),sQuery(id+"F0.wireOp",EDGE,"E10.1.0.3"),sQuery(id+"F0.wireOp",EDGE,"E10.1.0.4"),sQuery(id+"F0.wireOp",EDGE,"E10.1.0.5"),sQuery(id+"F0.wireOp",EDGE,"E10.1.1.0"),sQuery(id+"F0.wireOp",EDGE,"E10.1.1.1"),sQuery(id+"F0.wireOp",EDGE,"E10.1.1.2"),sQuery(id+"F0.wireOp",EDGE,"E10.1.1.3"),sQuery(id+"F0.wireOp",EDGE,"E10.1.1.4"),sQuery(id+"F0.wireOp",EDGE,"E10.1.1.5"),sQuery(id+"F0.wireOp",EDGE,"E10.1.2.0"),sQuery(id+"F0.wireOp",EDGE,"E10.1.2.1"),sQuery(id+"F0.wireOp",EDGE,"E10.1.2.2"),sQuery(id+"F0.wireOp",EDGE,"E10.1.2.3"),sQuery(id+"F0.wireOp",EDGE,"E10.1.2.4"),sQuery(id+"F0.wireOp",EDGE,"E10.1.2.5"),sQuery(id+"F0.wireOp",EDGE,"E10.2.0.0"),sQuery(id+"F0.wireOp",EDGE,"E10.2.0.1"),sQuery(id+"F0.wireOp",EDGE,"E10.2.0.2"),sQuery(id+"F0.wireOp",EDGE,"E10.2.0.3"),sQuery(id+"F0.wireOp",EDGE,"E10.2.0.4"),sQuery(id+"F0.wireOp",EDGE,"E10.2.0.5"),sQuery(id+"F0.wireOp",EDGE,"E10.2.1.0"),sQuery(id+"F0.wireOp",EDGE,"E10.2.1.1"),sQuery(id+"F0.wireOp",EDGE,"E10.2.1.2"),sQuery(id+"F0.wireOp",EDGE,"E10.2.1.3"),sQuery(id+"F0.wireOp",EDGE,"E10.2.1.4"),sQuery(id+"F0.wireOp",EDGE,"E10.2.1.5"),sQuery(id+"F0.wireOp",EDGE,"E10.2.2.0"),sQuery(id+"F0.wireOp",EDGE,"E10.2.2.1"),sQuery(id+"F0.wireOp",EDGE,"E10.2.2.2"),sQuery(id+"F0.wireOp",EDGE,"E10.2.2.3"),sQuery(id+"F0.wireOp",EDGE,"E10.2.2.4"),sQuery(id+"F0.wireOp",EDGE,"E10.2.2.5"),sQuery(id+"F0.wireOp",EDGE,"E10.3.0.0"),sQuery(id+"F0.wireOp",EDGE,"E10.3.0.1"),sQuery(id+"F0.wireOp",EDGE,"E10.3.0.2"),sQuery(id+"F0.wireOp",EDGE,"E10.3.0.3"),sQuery(id+"F0.wireOp",EDGE,"E10.3.0.4"),sQuery(id+"F0.wireOp",EDGE,"E10.3.0.5"),sQuery(id+"F0.wireOp",EDGE,"E10.3.1.0"),sQuery(id+"F0.wireOp",EDGE,"E10.3.1.1"),sQuery(id+"F0.wireOp",EDGE,"E10.3.1.2"),sQuery(id+"F0.wireOp",EDGE,"E10.3.1.3"),sQuery(id+"F0.wireOp",EDGE,"E10.3.1.4"),sQuery(id+"F0.wireOp",EDGE,"E10.3.1.5"),sQuery(id+"F0.wireOp",EDGE,"E10.3.2.0"),sQuery(id+"F0.wireOp",EDGE,"E10.3.2.1"),sQuery(id+"F0.wireOp",EDGE,"E10.3.2.2"),sQuery(id+"F0.wireOp",EDGE,"E10.3.2.3"),sQuery(id+"F0.wireOp",EDGE,"E10.3.2.4"),sQuery(id+"F0.wireOp",EDGE,"E10.3.2.5"),sQuery(id+"F0.wireOp",EDGE,"E10.4.0.0"),sQuery(id+"F0.wireOp",EDGE,"E10.4.0.1"),sQuery(id+"F0.wireOp",EDGE,"E10.4.0.2"),sQuery(id+"F0.wireOp",EDGE,"E10.4.0.3"),sQuery(id+"F0.wireOp",EDGE,"E10.4.0.4"),sQuery(id+"F0.wireOp",EDGE,"E10.4.0.5"),sQuery(id+"F0.wireOp",EDGE,"E10.4.1.0"),sQuery(id+"F0.wireOp",EDGE,"E10.4.1.1"),sQuery(id+"F0.wireOp",EDGE,"E10.4.1.2"),sQuery(id+"F0.wireOp",EDGE,"E10.4.1.3"),sQuery(id+"F0.wireOp",EDGE,"E10.4.1.4"),sQuery(id+"F0.wireOp",EDGE,"E10.4.1.5"),sQuery(id+"F0.wireOp",EDGE,"E10.4.2.0"),sQuery(id+"F0.wireOp",EDGE,"E10.4.2.1"),sQuery(id+"F0.wireOp",EDGE,"E10.4.2.2"),sQuery(id+"F0.wireOp",EDGE,"E10.4.2.3"),sQuery(id+"F0.wireOp",EDGE,"E10.4.2.4"),sQuery(id+"F0.wireOp",EDGE,"E10.4.2.5"),sQuery(id+"F0.wireOp",EDGE,"E10.5.0.0"),sQuery(id+"F0.wireOp",EDGE,"E10.5.0.1"),sQuery(id+"F0.wireOp",EDGE,"E10.5.0.2"),sQuery(id+"F0.wireOp",EDGE,"E10.5.0.3"),sQuery(id+"F0.wireOp",EDGE,"E10.5.0.4"),sQuery(id+"F0.wireOp",EDGE,"E10.5.0.5"),sQuery(id+"F0.wireOp",EDGE,"E10.5.1.0"),sQuery(id+"F0.wireOp",EDGE,"E10.5.1.1"),sQuery(id+"F0.wireOp",EDGE,"E10.5.1.2"),sQuery(id+"F0.wireOp",EDGE,"E10.5.1.3"),sQuery(id+"F0.wireOp",EDGE,"E10.5.1.4"),sQuery(id+"F0.wireOp",EDGE,"E10.5.1.5"),sQuery(id+"F0.wireOp",EDGE,"E10.5.2.0"),sQuery(id+"F0.wireOp",EDGE,"E10.5.2.1"),sQuery(id+"F0.wireOp",EDGE,"E10.5.2.2"),sQuery(id+"F0.wireOp",EDGE,"E10.5.2.3"),sQuery(id+"F0.wireOp",EDGE,"E10.5.2.4"),sQuery(id+"F0.wireOp",EDGE,"E10.5.2.5"),sQuery(id+"F0.wireOp",EDGE,"E10.6.0.0"),sQuery(id+"F0.wireOp",EDGE,"E10.6.0.1"),sQuery(id+"F0.wireOp",EDGE,"E10.6.0.2"),sQuery(id+"F0.wireOp",EDGE,"E10.6.0.3"),sQuery(id+"F0.wireOp",EDGE,"E10.6.0.4"),sQuery(id+"F0.wireOp",EDGE,"E10.6.0.5"),sQuery(id+"F0.wireOp",EDGE,"E10.6.1.0"),sQuery(id+"F0.wireOp",EDGE,"E10.6.1.1"),sQuery(id+"F0.wireOp",EDGE,"E10.6.1.2"),sQuery(id+"F0.wireOp",EDGE,"E10.6.1.3"),sQuery(id+"F0.wireOp",EDGE,"E10.6.1.4"),sQuery(id+"F0.wireOp",EDGE,"E10.6.1.5"),sQuery(id+"F0.wireOp",EDGE,"E10.6.2.0"),sQuery(id+"F0.wireOp",EDGE,"E10.6.2.1"),sQuery(id+"F0.wireOp",EDGE,"E10.6.2.2"),sQuery(id+"F0.wireOp",EDGE,"E10.6.2.3"),sQuery(id+"F0.wireOp",EDGE,"E10.6.2.4"),sQuery(id+"F0.wireOp",EDGE,"E10.6.2.5"),sQuery(id+"F0.wireOp",EDGE,"E10.7.0.0"),sQuery(id+"F0.wireOp",EDGE,"E10.7.0.1"),sQuery(id+"F0.wireOp",EDGE,"E10.7.0.2"),sQuery(id+"F0.wireOp",EDGE,"E10.7.0.3"),sQuery(id+"F0.wireOp",EDGE,"E10.7.0.4"),sQuery(id+"F0.wireOp",EDGE,"E10.7.0.5"),sQuery(id+"F0.wireOp",EDGE,"E10.7.1.0"),sQuery(id+"F0.wireOp",EDGE,"E10.7.1.1"),sQuery(id+"F0.wireOp",EDGE,"E10.7.1.2"),sQuery(id+"F0.wireOp",EDGE,"E10.7.1.3"),sQuery(id+"F0.wireOp",EDGE,"E10.7.1.4"),sQuery(id+"F0.wireOp",EDGE,"E10.7.1.5"),sQuery(id+"F0.wireOp",EDGE,"E10.7.2.0"),sQuery(id+"F0.wireOp",EDGE,"E10.7.2.1"),sQuery(id+"F0.wireOp",EDGE,"E10.7.2.2"),sQuery(id+"F0.wireOp",EDGE,"E10.7.2.3"),sQuery(id+"F0.wireOp",EDGE,"E10.7.2.4"),sQuery(id+"F0.wireOp",EDGE,"E10.7.2.5"),sQuery(id+"F0.wireOp",EDGE,"E10.8.0.0"),sQuery(id+"F0.wireOp",EDGE,"E10.8.0.1"),sQuery(id+"F0.wireOp",EDGE,"E10.8.0.2"),sQuery(id+"F0.wireOp",EDGE,"E10.8.0.3"),sQuery(id+"F0.wireOp",EDGE,"E10.8.0.4"),sQuery(id+"F0.wireOp",EDGE,"E10.8.0.5"),sQuery(id+"F0.wireOp",EDGE,"E10.8.1.0"),sQuery(id+"F0.wireOp",EDGE,"E10.8.1.1"),sQuery(id+"F0.wireOp",EDGE,"E10.8.1.2"),sQuery(id+"F0.wireOp",EDGE,"E10.8.1.3"),sQuery(id+"F0.wireOp",EDGE,"E10.8.1.4"),sQuery(id+"F0.wireOp",EDGE,"E10.8.1.5"),sQuery(id+"F0.wireOp",EDGE,"E10.8.2.0"),sQuery(id+"F0.wireOp",EDGE,"E10.8.2.1"),sQuery(id+"F0.wireOp",EDGE,"E10.8.2.2"),sQuery(id+"F0.wireOp",EDGE,"E10.8.2.3"),sQuery(id+"F0.wireOp",EDGE,"E10.8.2.4"),sQuery(id+"F0.wireOp",EDGE,"E10.8.2.5"),sQuery(id+"F0.wireOp",EDGE,"E10.9.0.0"),sQuery(id+"F0.wireOp",EDGE,"E10.9.0.1"),sQuery(id+"F0.wireOp",EDGE,"E10.9.0.2"),sQuery(id+"F0.wireOp",EDGE,"E10.9.0.3"),sQuery(id+"F0.wireOp",EDGE,"E10.9.0.4"),sQuery(id+"F0.wireOp",EDGE,"E10.9.0.5"),sQuery(id+"F0.wireOp",EDGE,"E10.9.1.0"),sQuery(id+"F0.wireOp",EDGE,"E10.9.1.1"),sQuery(id+"F0.wireOp",EDGE,"E10.9.1.2"),sQuery(id+"F0.wireOp",EDGE,"E10.9.1.3"),sQuery(id+"F0.wireOp",EDGE,"E10.9.1.4"),sQuery(id+"F0.wireOp",EDGE,"E10.9.1.5"),sQuery(id+"F0.wireOp",EDGE,"E10.9.2.0"),sQuery(id+"F0.wireOp",EDGE,"E10.9.2.1"),sQuery(id+"F0.wireOp",EDGE,"E10.9.2.2"),sQuery(id+"F0.wireOp",EDGE,"E10.9.2.3"),sQuery(id+"F0.wireOp",EDGE,"E10.9.2.4"),sQuery(id+"F0.wireOp",EDGE,"E10.9.2.5"),sQuery(id+"F0.wireOp",EDGE,"E10.10.0.0"),sQuery(id+"F0.wireOp",EDGE,"E10.10.0.1"),sQuery(id+"F0.wireOp",EDGE,"E10.10.0.2"),sQuery(id+"F0.wireOp",EDGE,"E10.10.0.3"),sQuery(id+"F0.wireOp",EDGE,"E10.10.0.4"),sQuery(id+"F0.wireOp",EDGE,"E10.10.0.5"),sQuery(id+"F0.wireOp",EDGE,"E10.10.1.0"),sQuery(id+"F0.wireOp",EDGE,"E10.10.1.1"),sQuery(id+"F0.wireOp",EDGE,"E10.10.1.2"),sQuery(id+"F0.wireOp",EDGE,"E10.10.1.3"),sQuery(id+"F0.wireOp",EDGE,"E10.10.1.4"),sQuery(id+"F0.wireOp",EDGE,"E10.10.1.5"),sQuery(id+"F0.wireOp",EDGE,"E10.10.2.0"),sQuery(id+"F0.wireOp",EDGE,"E10.10.2.1"),sQuery(id+"F0.wireOp",EDGE,"E10.10.2.2"),sQuery(id+"F0.wireOp",EDGE,"E10.10.2.3"),sQuery(id+"F0.wireOp",EDGE,"E10.10.2.4"),sQuery(id+"F0.wireOp",EDGE,"E10.10.2.5"),sQuery(id+"F0.wireOp",EDGE,"E12.1.0.1"),sQuery(id+"F0.wireOp",EDGE,"E12.1.0.2"),sQuery(id+"F0.wireOp",EDGE,"E12.1.0.6"),sQuery(id+"F0.wireOp",EDGE,"E12.1.0.8"),sQuery(id+"F0.wireOp",EDGE,"E12.1.0.9"),sQuery(id+"F0.wireOp",EDGE,"E12.1.0.10"),sQuery(id+"F0.wireOp",EDGE,"E12.1.0.11"),sQuery(id+"F0.wireOp",EDGE,"E12.1.0.12"),sQuery(id+"F0.wireOp",EDGE,"E12.1.0.15"),sQuery(id+"F0.wireOp",EDGE,"E12.1.0.18"),sQuery(id+"F0.wireOp",EDGE,"E12.1.0.19"),sQuery(id+"F0.wireOp",EDGE,"E12.1.0.20"),sQuery(id+"F0.wireOp",EDGE,"E12.1.0.21"),sQuery(id+"F0.wireOp",EDGE,"E12.1.0.24"),sQuery(id+"F0.wireOp",EDGE,"E12.1.0.35"),sQuery(id+"F0.wireOp",EDGE,"E12.1.0.37"),sQuery(id+"F0.wireOp",EDGE,"E12.1.0.40"),sQuery(id+"F0.wireOp",EDGE,"E12.1.0.41"),sQuery(id+"F0.wireOp",EDGE,"E12.1.0.46"),sQuery(id+"F0.wireOp",EDGE,"E12.1.0.47"),sQuery(id+"F0.wireOp",EDGE,"E12.1.0.48"),sQuery(id+"F0.wireOp",EDGE,"E12.1.0.49"),sQuery(id+"F0.wireOp",EDGE,"E12.1.0.50"),sQuery(id+"F0.wireOp",EDGE,"E12.1.0.54"),sQuery(id+"F0.wireOp",EDGE,"E12.1.0.55"),sQuery(id+"F0.wireOp",EDGE,"E12.1.0.56"),sQuery(id+"F0.wireOp",EDGE,"E12.1.0.58"),sQuery(id+"F0.wireOp",EDGE,"E12.1.0.59"),sQuery(id+"F0.wireOp",EDGE,"E12.1.0.61"),sQuery(id+"F0.wireOp",EDGE,"E12.1.0.62"),sQuery(id+"F0.wireOp",EDGE,"E12.1.0.63"),sQuery(id+"F0.wireOp",EDGE,"E12.1.0.65"),sQuery(id+"F0.wireOp",EDGE,"E12.1.0.66"),sQuery(id+"F0.wireOp",EDGE,"E12.1.0.67"),sQuery(id+"F0.wireOp",EDGE,"E12.1.0.68"),sQuery(id+"F0.wireOp",EDGE,"E12.1.0.69"),sQuery(id+"F0.wireOp",EDGE,"E12.1.0.70"),sQuery(id+"F0.wireOp",EDGE,"E12.1.0.71"),sQuery(id+"F0.wireOp",EDGE,"E12.1.0.72"),sQuery(id+"F0.wireOp",EDGE,"E12.1.0.73"),sQuery(id+"F0.wireOp",EDGE,"E12.1.0.74"),sQuery(id+"F0.wireOp",EDGE,"E12.1.0.75"),sQuery(id+"F0.wireOp",EDGE,"E12.1.0.76"),sQuery(id+"F0.wireOp",EDGE,"E12.1.0.77"),sQuery(id+"F0.wireOp",EDGE,"E12.1.0.78"),sQuery(id+"F0.wireOp",EDGE,"E12.1.0.79"),sQuery(id+"F0.wireOp",EDGE,"E12.1.0.80"),sQuery(id+"F0.wireOp",EDGE,"E12.1.0.82"),sQuery(id+"F0.wireOp",EDGE,"E12.1.0.83"),sQuery(id+"F0.wireOp",EDGE,"E12.1.0.84"),sQuery(id+"F0.wireOp",EDGE,"E12.1.0.86"),sQuery(id+"F0.wireOp",EDGE,"E12.1.0.88"),sQuery(id+"F0.wireOp",EDGE,"E12.1.0.90"),sQuery(id+"F0.wireOp",EDGE,"E12.1.0.91"),sQuery(id+"F0.wireOp",EDGE,"E12.1.0.92"),sQuery(id+"F0.wireOp",EDGE,"E12.1.0.93"),sQuery(id+"F0.wireOp",EDGE,"E12.1.0.94"),sQuery(id+"F0.wireOp",EDGE,"E12.1.0.95"),sQuery(id+"F0.wireOp",EDGE,"E12.1.0.96"),sQuery(id+"F0.wireOp",EDGE,"E12.1.0.98"),sQuery(id+"F0.wireOp",EDGE,"E12.1.0.100"),sQuery(id+"F0.wireOp",EDGE,"E12.1.0.101"),sQuery(id+"F0.wireOp",EDGE,"E12.1.0.102"),sQuery(id+"F0.wireOp",EDGE,"E12.1.0.103"),sQuery(id+"F0.wireOp",EDGE,"E12.1.0.104"),sQuery(id+"F0.wireOp",EDGE,"E12.1.0.105"),sQuery(id+"F0.wireOp",EDGE,"E12.1.0.106"),sQuery(id+"F0.wireOp",EDGE,"E12.1.0.107"),sQuery(id+"F0.wireOp",EDGE,"E12.1.0.108"),sQuery(id+"F0.wireOp",EDGE,"E12.1.0.109"),sQuery(id+"F0.wireOp",EDGE,"E12.1.0.111"),sQuery(id+"F0.wireOp",EDGE,"E12.1.0.114"),sQuery(id+"F0.wireOp",EDGE,"E12.1.0.115"),sQuery(id+"F0.wireOp",EDGE,"E12.1.0.116"),sQuery(id+"F0.wireOp",EDGE,"E12.1.0.119"),sQuery(id+"F0.wireOp",EDGE,"E12.1.0.120"),sQuery(id+"F0.wireOp",EDGE,"E12.1.0.121"),sQuery(id+"F0.wireOp",EDGE,"E12.1.0.122"),sQuery(id+"F0.wireOp",EDGE,"E70.bottom"),sQuery(id+"F0.wireOp",EDGE,"E70.top"),sQuery(id+"F0.wireOp",EDGE,"E70.left"),sQuery(id+"F0.wireOp",EDGE,"E70.right")])],"isStart":false});
            var sketch = newSketch(context, id + "F2", { "sketchPlane" : qUnion([Q0])});
            skLineSegment(sketch, "E71.0", {"start": v(428.67, 117.5) * mm, "end": v(437.33, 117.5) * mm, "construction": true});
            skLineSegment(sketch, "E72", {"start": v(433, 117.5) * mm, "end": v(433, 120) * mm});
            skLineSegment(sketch, "E73", {"start": v(473.41, 132.5) * mm, "end": v(473.41, -15.17) * mm});
            skLineSegment(sketch, "E74", {"start": v(473.41, -15.17) * mm, "end": v(433, -15.17) * mm});
            skPoint(sketch, "E74.endSnap0", {"position": v(433, 2.5) * mm});
            skLineSegment(sketch, "E75", {"start": v(433, 0) * mm, "end": v(433, 117.5) * mm});
            skLineSegment(sketch, "E76.0", {"start": v(38.97, -7.5) * mm, "end": v(30.3, -7.5) * mm, "construction": true});
            skLineSegment(sketch, "E77", {"start": v(34.64, -16.71) * mm, "end": v(4.53, -16.71) * mm});
            skLineSegment(sketch, "E78", {"start": v(4.53, -16.71) * mm, "end": v(4.53, 136.82) * mm});
            skLineSegment(sketch, "E79", {"start": v(4.53, 136.82) * mm, "end": v(34.64, 136.82) * mm});
            skPoint(sketch, "E79.endSnap0", {"position": v(34.64, 112.5) * mm});
            skLineSegment(sketch, "E80", {"start": v(34.64, 120) * mm, "end": v(34.64, 0) * mm});
            skLineSegment(sketch, "E81.0", {"start": v(47.63, 117.5) * mm, "end": v(56.3, 117.5) * mm, "construction": true});
            skLineSegment(sketch, "E82.0", {"start": v(56.3, 2.5) * mm, "end": v(47.63, 2.5) * mm, "construction": true});
            skLineSegment(sketch, "E83", {"start": v(34.64, -16.71) * mm, "end": v(433, -15.17) * mm});
            skPoint(sketch, "E84.orphan", {"position": v(34.64, -7.5) * mm});
            skLineSegment(sketch, "E85.trimOffspring", {"start": v(34.64, 0) * mm, "end": v(433, 0) * mm});
            skLineSegment(sketch, "E86.0", {"start": v(25.98, 120) * mm, "end": v(30.3, 127.5) * mm, "construction": true});
            skLineSegment(sketch, "E87.0", {"start": v(30.3, 112.5) * mm, "end": v(25.98, 120) * mm, "construction": true});
            skLineSegment(sketch, "E88", {"start": v(34.64, 120) * mm, "end": v(433, 120) * mm});
            skLineSegment(sketch, "E89", {"start": v(34.64, 136.82) * mm, "end": v(473.41, 136.82) * mm});
            skLineSegment(sketch, "E90", {"start": v(473.41, 136.82) * mm, "end": v(473.41, 132.5) * mm});
            skSolve(sketch);
        }
        {
            var Q0;
            Q0 = qSketchRegion(id + "F2", true);
            extrude(context, id + "F3", {"entities" : qUnion([Q0]), "operationType" : NewBodyOperationType.REMOVE, "oppositeDirection" : true, "depth" : 25 * mm, "offsetDistance" : 25 * mm});
        }
    });
